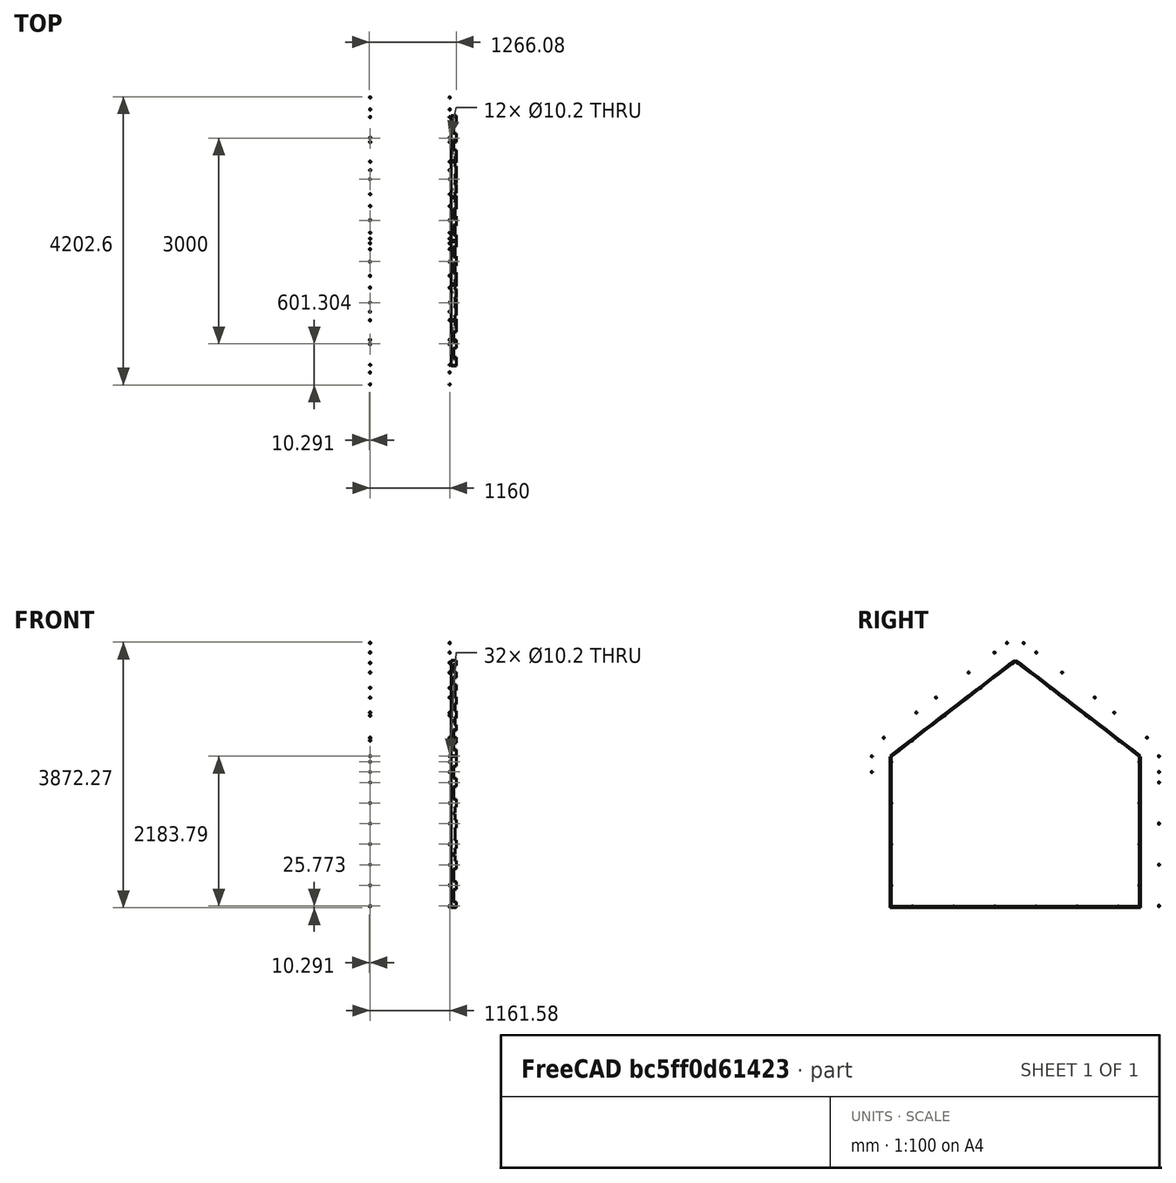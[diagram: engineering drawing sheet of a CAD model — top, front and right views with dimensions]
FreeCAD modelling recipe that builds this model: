
FCSTD DOCUMENT  (FreeCAD 0.17R11918 (Git))
Label: Unnamed1
License: CreativeCommons Attribution
LicenseURL: http://creativecommons.org/licenses/by/4.0/
objects: Part::FeaturePython×501, Part::Feature×150, Part::Part2DObjectPython×43, Part::Compound×19, Part::Cut×14, App::DocumentObjectGroupPython×13, App::DocumentObjectGroup×9, App::FeaturePython×1
note: 728 computed .brp shape members not serialized (recipe doc carries the construction recipe); baked Part::Feature solids carry a one-line shape summary decoded from their .brp

FEATURE [Part::Feature] Shape028  label="Bottom panel profile S"
  shape: bbox 1050 x 250 x 2e-07 mm, 0 faces, 0 solids (baked)
FEATURE [Part::Feature] Shape029  label="Bottom panel profile M"
  shape: bbox 1050 x 582 x 2e-07 mm, 0 faces, 0 solids (baked)
FEATURE [Part::Feature] Shape030  label="Bottom panel profile L"
  shape: bbox 1050 x 882 x 2e-07 mm, 0 faces, 0 solids (baked)
FEATURE [Part::Feature] Wire
  shape: bbox 250 x 1909 x 2e-07 mm, 0 faces, 0 solids (baked)
FEATURE [Part::Feature] Wire001
  shape: bbox 46 x 180 x 2e-07 mm, 0 faces, 0 solids (baked)
FEATURE [Part::Feature] Wire002
  shape: bbox 46 x 180 x 2e-07 mm, 0 faces, 0 solids (baked)
FEATURE [Part::Feature] Wire005
  shape: bbox 28 x 180 x 2e-07 mm, 0 faces, 0 solids (baked)
FEATURE [Part::Feature] Wire006
  shape: bbox 28 x 180 x 2e-07 mm, 0 faces, 0 solids (baked)
FEATURE [Part::Feature] Wire007
  shape: bbox 54 x 180 x 2e-07 mm, 0 faces, 0 solids (baked)
FEATURE [Part::Feature] Wire008
  shape: bbox 54 x 180 x 2e-07 mm, 0 faces, 0 solids (baked)
FEATURE [Part::Feature] Wire009 .. Wire012  x4 (patterned run collapsed; names and placements below)
  shape: bbox 28 x 180 x 2e-07 mm, 0 faces, 0 solids (baked)
FEATURE [Part::Feature] Wire021
  shape: bbox 2e-07 x 1341 x 707.1 mm, 0 faces, 0 solids (baked)
FEATURE [Part::Feature] Wire025
  shape: bbox 2e-07 x 28 x 72 mm, 0 faces, 0 solids (baked)
FEATURE [Part::Feature] Wire042
  shape: bbox 2e-07 x 813.7 x 1306 mm, 0 faces, 0 solids (baked)
FEATURE [Part::Feature] Wire043 .. Wire046  x4 (patterned run collapsed; names and placements below)
  shape: bbox 46 x 2e-07 x 180 mm, 0 faces, 0 solids (baked)
FEATURE [Part::Feature] Wire047
  shape: bbox 44 x 2e-07 x 180 mm, 0 faces, 0 solids (baked)
FEATURE [Part::Feature] Wire049
  shape: bbox 28 x 2e-07 x 180 mm, 0 faces, 0 solids (baked)
FEATURE [Part::Feature] Wire050
  shape: bbox 28 x 2e-07 x 180 mm, 0 faces, 0 solids (baked)
FEATURE [Part::Feature] Wire051
  shape: bbox 54 x 2e-07 x 180 mm, 0 faces, 0 solids (baked)
FEATURE [Part::Feature] Wire052
  shape: bbox 54 x 2e-07 x 180 mm, 0 faces, 0 solids (baked)
FEATURE [Part::Feature] Wire053 .. Wire056  x4 (patterned run collapsed; names and placements below)
  shape: bbox 46 x 2e-07 x 180 mm, 0 faces, 0 solids (baked)
FEATURE [Part::Feature] Wire057
  shape: bbox 1200 x 2e-07 x 2187 mm, 0 faces, 0 solids (baked)
FEATURE [Part::Feature] Wire058
  shape: bbox 54 x 180 x 2e-07 mm, 0 faces, 0 solids (baked)
FEATURE [Part::Feature] Wire059
  shape: bbox 54 x 180 x 2e-07 mm, 0 faces, 0 solids (baked)
FEATURE [Part::Feature] Wire060
  shape: bbox 54 x 180 x 2e-07 mm, 0 faces, 0 solids (baked)
FEATURE [Part::Feature] Wire061
  shape: bbox 90 x 23 x 2e-07 mm, 0 faces, 0 solids (baked)
FEATURE [Part::Feature] Wire062
  shape: bbox 54 x 180 x 2e-07 mm, 0 faces, 0 solids (baked)
FEATURE [Part::Feature] Wire063
  shape: bbox 46 x 180 x 2e-07 mm, 0 faces, 0 solids (baked)
FEATURE [Part::Feature] Wire064
  shape: bbox 46 x 180 x 2e-07 mm, 0 faces, 0 solids (baked)
FEATURE [Part::Feature] Wire065
  shape: bbox 71 x 180 x 2e-07 mm, 0 faces, 0 solids (baked)
FEATURE [Part::Feature] Wire066
  shape: bbox 90 x 23 x 2e-07 mm, 0 faces, 0 solids (baked)
FEATURE [Part::Feature] Wire067
  shape: bbox 71 x 180 x 2e-07 mm, 0 faces, 0 solids (baked)
FEATURE [Part::Feature] Wire068
  shape: bbox 1200 x 1384 x 2e-07 mm, 0 faces, 0 solids (baked)
FEATURE [Part::Compound] Compound005  label="floor panel profile small"
  Links = -> [Wire058,Wire059,Wire060,Wire068,Wire062,Wire061,Wire063,Wire064,Wire065,Wire066,Wire067]
FEATURE [Part::Feature] Wire069
  shape: bbox 71 x 180 x 2e-07 mm, 0 faces, 0 solids (baked)
FEATURE [Part::Feature] Wire070
  shape: bbox 90 x 23 x 2e-07 mm, 0 faces, 0 solids (baked)
FEATURE [Part::Feature] Wire071
  shape: bbox 71 x 180 x 2e-07 mm, 0 faces, 0 solids (baked)
FEATURE [Part::Feature] Wire072
  shape: bbox 46 x 180 x 2e-07 mm, 0 faces, 0 solids (baked)
FEATURE [Part::Feature] Wire073
  shape: bbox 46 x 180 x 2e-07 mm, 0 faces, 0 solids (baked)
FEATURE [Part::Feature] Wire074
  shape: bbox 54 x 180 x 2e-07 mm, 0 faces, 0 solids (baked)
FEATURE [Part::Feature] Wire075
  shape: bbox 90 x 23 x 2e-07 mm, 0 faces, 0 solids (baked)
FEATURE [Part::Feature] Wire076 .. Wire079  x4 (patterned run collapsed; names and placements below)
  shape: bbox 54 x 180 x 2e-07 mm, 0 faces, 0 solids (baked)
FEATURE [Part::Feature] Wire080
  shape: bbox 90 x 23 x 2e-07 mm, 0 faces, 0 solids (baked)
FEATURE [Part::Feature] Wire081
  shape: bbox 54 x 180 x 2e-07 mm, 0 faces, 0 solids (baked)
FEATURE [Part::Feature] Wire082 .. Wire085  x4 (patterned run collapsed; names and placements below)
  shape: bbox 28 x 180 x 2e-07 mm, 0 faces, 0 solids (baked)
FEATURE [Part::Feature] Wire086
  shape: bbox 1200 x 2284 x 2e-07 mm, 0 faces, 0 solids (baked)
FEATURE [Part::Compound] Compound006  label="floor panel profile large"
  Links = -> [Wire069,Wire084,Wire076,Wire077,Wire071,Wire080,Wire078,Wire075,Wire079,Wire081,Wire082,Wire083,Wire073,Wire072,Wire086,Wire074,Wire085,Wire070]
FEATURE [Part::FeaturePython] Panel028  label="Floor panel small 001"  # WARN: FeaturePython — macro-defined, semantics opaque (R4)
  Area = 1.59758e+06
  Base = -> Compound005
  Description = Floor panel
  FaceMaker = 0
  HorizontalArea = 0
  Length = 0
  MoveWithHost = false
  Normal = (0,0,-1)
  PerimeterLength = 0
  Role = 0
  Sheets = 1
  Tag = L61
  Thickness = 18
  VerticalArea = 0
  WaveDirection = 0
  WaveHeight = 0
  WaveLength = 0
  WaveType = 0
  Width = 0
FEATURE [Part::FeaturePython] Panel029  label="Floor panel large 001"  # WARN: FeaturePython — macro-defined, semantics opaque (R4)
  Area = 2.65298e+06
  Base = -> Compound006
  Description = Floor panel
  FaceMaker = 0
  HorizontalArea = 0
  Length = 0
  MoveWithHost = false
  Normal = (0,0,-1)
  PerimeterLength = 0
  Role = 0
  Sheets = 1
  Tag = L62
  Thickness = 18
  VerticalArea = 0
  WaveDirection = 0
  WaveHeight = 0
  WaveLength = 0
  WaveType = 0
  Width = 0
FEATURE [Part::Feature] Shape035
  shape: bbox 54 x 2e-07 x 180 mm, 0 faces, 0 solids (baked)
FEATURE [Part::Feature] Shape034017
  shape: bbox 28 x 180 x 2e-07 mm, 0 faces, 0 solids (baked)
FEATURE [Part::Feature] Shape034018
  shape: bbox 54 x 180 x 2e-07 mm, 0 faces, 0 solids (baked)
FEATURE [Part::Feature] Shape034019
  shape: bbox 46 x 180 x 2e-07 mm, 0 faces, 0 solids (baked)
FEATURE [Part::Feature] Shape034020
  shape: bbox 46 x 180 x 2e-07 mm, 0 faces, 0 solids (baked)
FEATURE [Part::Feature] Shape034021
  shape: bbox 54 x 180 x 2e-07 mm, 0 faces, 0 solids (baked)
FEATURE [Part::Feature] Shape034022
  shape: bbox 54 x 180 x 2e-07 mm, 0 faces, 0 solids (baked)
FEATURE [Part::Feature] Shape034023
  shape: bbox 54 x 180 x 2e-07 mm, 0 faces, 0 solids (baked)
FEATURE [Part::Feature] Shape034024 .. Shape034027  x4 (patterned run collapsed; names and placements below)
  shape: bbox 46 x 180 x 2e-07 mm, 0 faces, 0 solids (baked)
FEATURE [Part::Feature] Shape034028
  shape: bbox 28 x 180 x 2e-07 mm, 0 faces, 0 solids (baked)
FEATURE [Part::Feature] Shape034029
  shape: bbox 46 x 180 x 2e-07 mm, 0 faces, 0 solids (baked)
FEATURE [Part::Feature] Shape034030
  shape: bbox 46 x 180 x 2e-07 mm, 0 faces, 0 solids (baked)
FEATURE [Part::Feature] Shape034031
  shape: bbox 1200 x 2280 x 2e-07 mm, 0 faces, 0 solids (baked)
FEATURE [Part::Feature] Shape034032
  shape: bbox 39 x 28 x 2e-07 mm, 0 faces, 0 solids (baked)
FEATURE [Part::Feature] Shape034033
  shape: bbox 1200 x 268 x 2e-07 mm, 0 faces, 0 solids (baked)
FEATURE [Part::Feature] Shape034034
  shape: bbox 39 x 28 x 2e-07 mm, 0 faces, 0 solids (baked)
FEATURE [Part::Compound] Compound011  label="Spacer profile large"
  Links = -> [Shape034032,Shape034033,Shape034034]
FEATURE [Part::FeaturePython] Panel034  label="Spacer 001"  # WARN: FeaturePython — macro-defined, semantics opaque (R4)
  Area = 273615
  Base = -> Compound011
  Description = Spacer
  FaceMaker = 0
  HorizontalArea = 0
  Length = 0
  MoveWithHost = false
  Normal = (0,0,1)
  PerimeterLength = 0
  Placement = pos=(0,0,134) rot=(0,0,1;0rad)
  Role = 0
  Sheets = 1
  Tag = SPACER/F
  Thickness = 18
  VerticalArea = 0
  WaveDirection = 0
  WaveHeight = 0
  WaveLength = 0
  WaveType = 0
  Width = 0
FEATURE [Part::FeaturePython] Panel035  label="Spacer 002"  # WARN: FeaturePython — macro-defined, semantics opaque (R4)
  Area = 273615
  CloneOf = -> Panel034
  Description = Spacer
  FaceMaker = 0
  HorizontalArea = 0
  Length = 0
  MoveWithHost = false
  Normal = (0,0,0)
  PerimeterLength = 0
  Placement = pos=(0,-1659,-1807) rot=(-1,0,0;1.5708rad)
  Role = 0
  Sheets = 1
  Tag = SPACER/F
  Thickness = 18
  VerticalArea = 0
  WaveDirection = 0
  WaveHeight = 0
  WaveLength = 0
  WaveType = 0
  Width = 0
FEATURE [Part::FeaturePython] Panel036  label="Spacer 003"  # WARN: FeaturePython — macro-defined, semantics opaque (R4)
  Area = 273615
  CloneOf = -> Panel034
  Description = Spacer
  FaceMaker = 0
  HorizontalArea = 0
  Length = 0
  MoveWithHost = false
  Normal = (0,0,0)
  PerimeterLength = 0
  Placement = pos=(0,-1059,-1807) rot=(-1,0,0;1.5708rad)
  Role = 0
  Sheets = 1
  Tag = SPACER/F
  Thickness = 18
  VerticalArea = 0
  WaveDirection = 0
  WaveHeight = 0
  WaveLength = 0
  WaveType = 0
  Width = 0
FEATURE [Part::FeaturePython] Panel037  label="Spacer 004"  # WARN: FeaturePython — macro-defined, semantics opaque (R4)
  Area = 273615
  CloneOf = -> Panel034
  Description = Spacer
  FaceMaker = 0
  HorizontalArea = 0
  Length = 0
  MoveWithHost = false
  Normal = (0,0,0)
  PerimeterLength = 0
  Placement = pos=(0,-458.997,-1807) rot=(-1,0,0;1.5708rad)
  Role = 0
  Sheets = 1
  Tag = SPACER/F
  Thickness = 18
  VerticalArea = 0
  WaveDirection = 0
  WaveHeight = 0
  WaveLength = 0
  WaveType = 0
  Width = 0
FEATURE [Part::FeaturePython] Panel038  label="Spacer 005"  # WARN: FeaturePython — macro-defined, semantics opaque (R4)
  Area = 273615
  CloneOf = -> Panel034
  Description = Spacer
  FaceMaker = 0
  HorizontalArea = 0
  Length = 0
  MoveWithHost = false
  Normal = (0,0,0)
  PerimeterLength = 0
  Placement = pos=(0,440.996,-1807) rot=(-1,0,0;1.5708rad)
  Role = 0
  Sheets = 1
  Tag = SPACER/F
  Thickness = 18
  VerticalArea = 0
  WaveDirection = 0
  WaveHeight = 0
  WaveLength = 0
  WaveType = 0
  Width = 0
FEATURE [Part::FeaturePython] Panel039  label="Spacer 006"  # WARN: FeaturePython — macro-defined, semantics opaque (R4)
  Area = 273615
  CloneOf = -> Panel034
  Description = Spacer
  FaceMaker = 0
  HorizontalArea = 0
  Length = 0
  MoveWithHost = false
  Normal = (0,0,0)
  PerimeterLength = 0
  Placement = pos=(0,1041,-1807) rot=(-1,0,0;1.5708rad)
  Role = 0
  Sheets = 1
  Tag = SPACER/F
  Thickness = 18
  VerticalArea = 0
  WaveDirection = 0
  WaveHeight = 0
  WaveLength = 0
  WaveType = 0
  Width = 0
FEATURE [Part::FeaturePython] Panel040  label="Spacer 007"  # WARN: FeaturePython — macro-defined, semantics opaque (R4)
  Area = 273615
  CloneOf = -> Panel034
  Description = Spacer
  FaceMaker = 0
  HorizontalArea = 0
  Length = 0
  MoveWithHost = false
  Normal = (0,0,0)
  PerimeterLength = 0
  Placement = pos=(0,1641,-1807) rot=(-1,0,0;1.5708rad)
  Role = 0
  Sheets = 1
  Tag = SPACER/F
  Thickness = 18
  VerticalArea = 0
  WaveDirection = 0
  WaveHeight = 0
  WaveLength = 0
  WaveType = 0
  Width = 0
FEATURE [Part::FeaturePython] Panel041  label="Spacer 008"  # WARN: FeaturePython — macro-defined, semantics opaque (R4)
  Area = 273615
  CloneOf = -> Panel034
  Description = Spacer
  FaceMaker = 0
  HorizontalArea = 0
  Length = 0
  MoveWithHost = false
  Normal = (0,0,0)
  PerimeterLength = 0
  Placement = pos=(0,-2.785e-09,152) rot=(1,0,0;3.14159rad)
  Role = 0
  Sheets = 1
  Tag = SPACER/F
  Thickness = 18
  VerticalArea = 0
  WaveDirection = 0
  WaveHeight = 0
  WaveLength = 0
  WaveType = 0
  Width = 0
FEATURE [Part::Feature] Shape034035  label="Spacer profile small"
  shape: bbox 1200 x 268 x 2e-07 mm, 0 faces, 0 solids (baked)
FEATURE [Part::FeaturePython] Panel042  label="Spacer 009"  # WARN: FeaturePython — macro-defined, semantics opaque (R4)
  Area = 275459
  Base = -> Shape034035
  Description = Spacer
  FaceMaker = 0
  HorizontalArea = 0
  Length = 0
  MoveWithHost = false
  Normal = (0,0,1)
  PerimeterLength = 0
  Placement = pos=(0,0,2463.44) rot=(0,0,1;0rad)
  Role = 0
  Sheets = 1
  Tag = SPACER/R
  Thickness = 18
  VerticalArea = 0
  WaveDirection = 0
  WaveHeight = 0
  WaveLength = 0
  WaveType = 0
  Width = 0
FEATURE [Part::FeaturePython] Panel043  label="Spacer 010"  # WARN: FeaturePython — macro-defined, semantics opaque (R4)
  Area = 275459
  CloneOf = -> Panel042
  Description = Spacer
  FaceMaker = 0
  HorizontalArea = 0
  Length = 0
  MoveWithHost = false
  Normal = (0,0,0)
  PerimeterLength = 0
  Placement = pos=(-0.000976562,9.00024,6018.77) rot=(1,0,0;1.5708rad)
  Role = 0
  Sheets = 1
  Tag = SPACER/R
  Thickness = 18
  VerticalArea = 0
  WaveDirection = 0
  WaveHeight = 0
  WaveLength = 0
  WaveType = 0
  Width = 0
FEATURE [Part::FeaturePython] Panel044  label="Spacer 011"  # WARN: FeaturePython — macro-defined, semantics opaque (R4)
  Area = 275459
  CloneOf = -> Panel042
  Description = Spacer
  FaceMaker = 0
  HorizontalArea = 0
  Length = 0
  MoveWithHost = false
  Normal = (0,0,0)
  PerimeterLength = 0
  Placement = pos=(0,0,2481.44) rot=(1,0,0;3.14159rad)
  Role = 0
  Sheets = 1
  Tag = SPACER/R
  Thickness = 18
  VerticalArea = 0
  WaveDirection = 0
  WaveHeight = 0
  WaveLength = 0
  WaveType = 0
  Width = 0
FEATURE [Part::Feature] Wire091  label="Lock"
  shape: bbox 230 x 2e-07 x 120.4 mm, 0 faces, 0 solids (baked)
FEATURE [Part::FeaturePython] Panel045  label="Lock 001"  # WARN: FeaturePython — macro-defined, semantics opaque (R4)
  Area = 14950.6
  Base = -> Wire091
  Description = Lock
  FaceMaker = 0
  HorizontalArea = 0
  Length = 0
  MoveWithHost = false
  Normal = (0,-1,0)
  PerimeterLength = 0
  Role = 0
  Sheets = 1
  Tag = L43
  Thickness = 18
  VerticalArea = 0
  WaveDirection = 0
  WaveHeight = 0
  WaveLength = 0
  WaveType = 0
  Width = 0
FEATURE [Part::FeaturePython] Panel046  label="Lock 002"  # WARN: FeaturePython — macro-defined, semantics opaque (R4)
  Area = 14950.6
  CloneOf = -> Panel045
  Description = Lock
  FaceMaker = 0
  HorizontalArea = 0
  Length = 0
  MoveWithHost = false
  Normal = (0,0,0)
  PerimeterLength = 0
  Placement = pos=(1198.67,0,0) rot=(0,0,1;0rad)
  Role = 0
  Sheets = 1
  Tag = L43
  Thickness = 18
  VerticalArea = 0
  WaveDirection = 0
  WaveHeight = 0
  WaveLength = 0
  WaveType = 0
  Width = 0
FEATURE [Part::FeaturePython] Panel047  label="Lock 003"  # WARN: FeaturePython — macro-defined, semantics opaque (R4)
  Area = 14950.6
  CloneOf = -> Panel045
  Description = Lock
  FaceMaker = 0
  HorizontalArea = 0
  Length = 0
  MoveWithHost = false
  Normal = (0,0,0)
  PerimeterLength = 0
  Placement = pos=(1198.67,3899.99,0) rot=(0,0,1;0rad)
  Role = 0
  Sheets = 1
  Tag = L43
  Thickness = 18
  VerticalArea = 0
  WaveDirection = 0
  WaveHeight = 0
  WaveLength = 0
  WaveType = 0
  Width = 0
FEATURE [Part::FeaturePython] Panel048  label="Lock 004"  # WARN: FeaturePython — macro-defined, semantics opaque (R4)
  Area = 14950.6
  CloneOf = -> Panel045
  Description = Lock
  FaceMaker = 0
  HorizontalArea = 0
  Length = 0
  MoveWithHost = false
  Normal = (0,0,0)
  PerimeterLength = 0
  Placement = pos=(0,3899.99,0) rot=(0,0,1;0rad)
  Role = 0
  Sheets = 1
  Tag = L43
  Thickness = 18
  VerticalArea = 0
  WaveDirection = 0
  WaveHeight = 0
  WaveLength = 0
  WaveType = 0
  Width = 0
FEATURE [App::DocumentObjectGroupPython] VisGroup003  label="level4 spacers (3 originals)"  # scripted group (container) (typed FeaturePython)
  Group = -> [Panel034,Panel035,Panel036,Panel037,Panel038,Panel039,Panel040,Panel041,Panel042,Panel043,Panel044,Panel045,Panel046,Panel047,Panel048]
FEATURE [Part::Feature] Shape034040
  shape: bbox 2e-07 x 1409 x 733.2 mm, 0 faces, 0 solids (baked)
FEATURE [Part::Feature] Shape034046
  shape: bbox 2e-07 x 28 x 72 mm, 0 faces, 0 solids (baked)
FEATURE [Part::Feature] Shape034064
  shape: bbox 2e-07 x 72 x 28 mm, 0 faces, 0 solids (baked)
FEATURE [Part::Feature] Shape034067
  shape: bbox 2e-07 x 1573 x 1916 mm, 0 faces, 0 solids (baked)
FEATURE [Part::Feature] Shape034087
  shape: bbox 2e-07 x 28 x 72 mm, 0 faces, 0 solids (baked)
FEATURE [Part::Feature] Shape034095
  shape: bbox 2e-07 x 2415 x 286 mm, 0 faces, 0 solids (baked)
FEATURE [Part::Feature] Shape034102
  shape: bbox 2e-07 x 28 x 72 mm, 0 faces, 0 solids (baked)
FEATURE [Part::Feature] Shape034103
  shape: bbox 2e-07 x 28 x 72 mm, 0 faces, 0 solids (baked)
FEATURE [Part::Feature] Shape034104
  shape: bbox 2e-07 x 28 x 72 mm, 0 faces, 0 solids (baked)
FEATURE [Part::Feature] Shape034107
  shape: bbox 2e-07 x 28 x 72 mm, 0 faces, 0 solids (baked)
FEATURE [Part::Feature] Shape034120
  shape: bbox 2e-07 x 72 x 28 mm, 0 faces, 0 solids (baked)
FEATURE [Part::FeaturePython] Panel073  label="Bottom panel small 001"  # WARN: FeaturePython — macro-defined, semantics opaque (R4)
  Area = 262499
  Base = -> Shape028
  Description = Bottom panel
  FaceMaker = 0
  HorizontalArea = 0
  Length = 0
  MoveWithHost = false
  Normal = (0,0,1)
  PerimeterLength = 0
  Role = 0
  Sheets = 1
  Tag = L43
  Thickness = 18
  VerticalArea = 0
  WaveDirection = 0
  WaveHeight = 0
  WaveLength = 0
  WaveType = 0
  Width = 0
FEATURE [Part::FeaturePython] Panel074  label="Bottom panel medium 001"  # WARN: FeaturePython — macro-defined, semantics opaque (R4)
  Area = 611099
  Base = -> Shape029
  Description = Bottom panel
  FaceMaker = 0
  HorizontalArea = 0
  Length = 0
  MoveWithHost = false
  Normal = (0,0,1)
  PerimeterLength = 0
  Role = 0
  Sheets = 1
  Tag = FLOOR/M
  Thickness = 18
  VerticalArea = 0
  WaveDirection = 0
  WaveHeight = 0
  WaveLength = 0
  WaveType = 0
  Width = 0
FEATURE [Part::FeaturePython] Panel075  label="Bottom panel large 001"  # WARN: FeaturePython — macro-defined, semantics opaque (R4)
  Area = 926091
  Base = -> Shape030
  Description = Bottom panel
  FaceMaker = 0
  HorizontalArea = 0
  Length = 0
  MoveWithHost = false
  Normal = (0,0,1)
  PerimeterLength = 0
  Role = 0
  Sheets = 1
  Tag = L41
  Thickness = 18
  VerticalArea = 0
  WaveDirection = 0
  WaveHeight = 0
  WaveLength = 0
  WaveType = 0
  Width = 0
FEATURE [Part::Feature] Shape034126  label="Bottom lock profile"
  shape: bbox 1200 x 101 x 2e-07 mm, 0 faces, 0 solids (baked)
FEATURE [Part::FeaturePython] Panel076  label="Bottom lock 001"  # WARN: FeaturePython — macro-defined, semantics opaque (R4)
  Area = 118903
  Base = -> Shape034126
  Description = Bottom panel
  FaceMaker = 0
  HorizontalArea = 0
  Length = 0
  MoveWithHost = false
  Normal = (0,0,1)
  PerimeterLength = 0
  Role = 0
  Sheets = 1
  Tag = SKI/C
  Thickness = 18
  VerticalArea = 0
  WaveDirection = 0
  WaveHeight = 0
  WaveLength = 0
  WaveType = 0
  Width = 0
FEATURE [Part::Feature] Shape034127
  shape: bbox 46 x 2e-07 x 180 mm, 0 faces, 0 solids (baked)
FEATURE [Part::Feature] Shape034128
  shape: bbox 46 x 2e-07 x 180 mm, 0 faces, 0 solids (baked)
FEATURE [Part::Feature] Shape034129
  shape: bbox 54 x 2e-07 x 180 mm, 0 faces, 0 solids (baked)
FEATURE [Part::Feature] Shape034130
  shape: bbox 1200 x 2e-07 x 2107 mm, 0 faces, 0 solids (baked)
FEATURE [Part::Feature] Shape034131
  shape: bbox 54 x 2e-07 x 180 mm, 0 faces, 0 solids (baked)
FEATURE [Part::Feature] Shape034132
  shape: bbox 54 x 2e-07 x 180 mm, 0 faces, 0 solids (baked)
FEATURE [Part::Feature] Shape034133
  shape: bbox 46 x 2e-07 x 180 mm, 0 faces, 0 solids (baked)
FEATURE [Part::Feature] Shape034134
  shape: bbox 46 x 2e-07 x 180 mm, 0 faces, 0 solids (baked)
FEATURE [Part::Feature] Shape034135
  shape: bbox 71 x 2e-07 x 180 mm, 0 faces, 0 solids (baked)
FEATURE [Part::Feature] Shape034136
  shape: bbox 46 x 2e-07 x 180 mm, 0 faces, 0 solids (baked)
FEATURE [Part::Feature] Shape034137
  shape: bbox 28 x 2e-07 x 180 mm, 0 faces, 0 solids (baked)
FEATURE [Part::Feature] Shape034138
  shape: bbox 46 x 2e-07 x 180 mm, 0 faces, 0 solids (baked)
FEATURE [Part::Feature] Shape034139
  shape: bbox 54 x 2e-07 x 180 mm, 0 faces, 0 solids (baked)
FEATURE [Part::Feature] Shape034140
  shape: bbox 28 x 2e-07 x 180 mm, 0 faces, 0 solids (baked)
FEATURE [Part::Feature] Shape034141
  shape: bbox 71 x 2e-07 x 180 mm, 0 faces, 0 solids (baked)
FEATURE [Part::Feature] Shape034142
  shape: bbox 90 x 2e-07 x 23 mm, 0 faces, 0 solids (baked)
FEATURE [Part::Compound] Compound023  label="Outer side panel profile L"
  Links = -> [Shape034127,Shape034134,Shape034133,Shape034130,Shape034139,Shape034129,Shape034131,Shape034137,Shape034136,Shape034141,Shape034132,Shape034140,Shape034135,Shape034128,Shape034142,Shape034138]
FEATURE [Part::FeaturePython] Panel077  label="Outer side panel large 001"  # WARN: FeaturePython — macro-defined, semantics opaque (R4)
  Area = 2.40982e+06
  Base = -> Compound023
  Description = Outer side panel
  FaceMaker = 0
  HorizontalArea = 0
  Length = 0
  MoveWithHost = false
  Normal = (0,1,0)
  PerimeterLength = 0
  Placement = pos=(0,-2093,0) rot=(0,0,1;0rad)
  Role = 0
  Sheets = 1
  Tag = L45
  Thickness = 18
  VerticalArea = 0
  WaveDirection = 0
  WaveHeight = 0
  WaveLength = 0
  WaveType = 0
  Width = 0
FEATURE [Part::Feature] Shape034143
  shape: bbox 46 x 2e-07 x 180 mm, 0 faces, 0 solids (baked)
FEATURE [Part::Feature] Shape034144
  shape: bbox 90 x 2e-07 x 23 mm, 0 faces, 0 solids (baked)
FEATURE [Part::Feature] Shape034145
  shape: bbox 1200 x 2e-07 x 543.8 mm, 0 faces, 0 solids (baked)
FEATURE [Part::Feature] Shape034146
  shape: bbox 46 x 2e-07 x 180 mm, 0 faces, 0 solids (baked)
FEATURE [Part::Compound] Compound025  label="Outer side panel profile S"
  Links = -> [Shape034143,Shape034144,Shape034145,Shape034146]
FEATURE [Part::FeaturePython] Panel078  label="Outer side panel small 001"  # WARN: FeaturePython — macro-defined, semantics opaque (R4)
  Area = 598321
  Base = -> Compound025
  Description = Outer side panel
  FaceMaker = 0
  HorizontalArea = 0
  Length = 0
  MoveWithHost = false
  Normal = (0,1,0)
  PerimeterLength = 0
  Placement = pos=(0,-2093,0) rot=(0,0,1;0rad)
  Role = 0
  Sheets = 1
  Tag = L46
  Thickness = 18
  VerticalArea = 0
  WaveDirection = 0
  WaveHeight = 0
  WaveLength = 0
  WaveType = 0
  Width = 0
FEATURE [Part::Feature] Wire112
  shape: bbox 46 x 180 x 2e-07 mm, 0 faces, 0 solids (baked)
FEATURE [Part::Feature] Wire113
  shape: bbox 46 x 180 x 2e-07 mm, 0 faces, 0 solids (baked)
FEATURE [Part::Feature] Wire114
  shape: bbox 54 x 180 x 2e-07 mm, 0 faces, 0 solids (baked)
FEATURE [Part::Feature] Wire115
  shape: bbox 54 x 180 x 2e-07 mm, 0 faces, 0 solids (baked)
FEATURE [Part::Feature] Wire116
  shape: bbox 28 x 180 x 2e-07 mm, 0 faces, 0 solids (baked)
FEATURE [Part::Feature] Wire117
  shape: bbox 28 x 180 x 2e-07 mm, 0 faces, 0 solids (baked)
FEATURE [Part::Feature] Wire118
  shape: bbox 54 x 180 x 2e-07 mm, 0 faces, 0 solids (baked)
FEATURE [Part::Feature] Wire119
  shape: bbox 54 x 180 x 2e-07 mm, 0 faces, 0 solids (baked)
FEATURE [Part::Feature] Wire120 .. Wire123  x4 (patterned run collapsed; names and placements below)
  shape: bbox 46 x 180 x 2e-07 mm, 0 faces, 0 solids (baked)
FEATURE [Part::Feature] Wire124
  shape: bbox 1200 x 2104 x 2e-07 mm, 0 faces, 0 solids (baked)
FEATURE [Part::Compound] Compound026  label="Outer roof profile L"
  Links = -> [Wire112,Wire124,Wire119,Wire117,Wire113,Wire116,Wire118,Wire114,Wire121,Wire115,Wire120,Wire122,Wire123]
FEATURE [Part::FeaturePython] Panel079  label="Outer roof panel large 001"  # WARN: FeaturePython — macro-defined, semantics opaque (R4)
  Area = 2.42218e+06
  Base = -> Compound026
  Description = Roof panel
  FaceMaker = 0
  HorizontalArea = 0
  Length = 0
  MoveWithHost = false
  Normal = (0,0,1)
  PerimeterLength = 0
  Placement = pos=(1486.92,-421.605,3876.38) rot=(1,0,0;0.655696rad)
  Role = 0
  Sheets = 1
  Tag = L47
  Thickness = 18
  VerticalArea = 0
  WaveDirection = 0
  WaveHeight = 0
  WaveLength = 0
  WaveType = 0
  Width = 0
FEATURE [Part::Feature] Wire125
  shape: bbox 46 x 180 x 2e-07 mm, 0 faces, 0 solids (baked)
FEATURE [Part::Feature] Wire126
  shape: bbox 46 x 180 x 2e-07 mm, 0 faces, 0 solids (baked)
FEATURE [Part::Feature] Wire127
  shape: bbox 1200 x 578.4 x 2e-07 mm, 0 faces, 0 solids (baked)
FEATURE [Part::FeaturePython] Panel081  label="Bottom panel medium 002"  # WARN: FeaturePython — macro-defined, semantics opaque (R4)
  Area = 611099
  CloneOf = -> Panel074
  Description = Bottom panel
  FaceMaker = 0
  HorizontalArea = 0
  Length = 0
  MoveWithHost = false
  Normal = (0,0,0)
  PerimeterLength = 0
  Placement = pos=(0,600.001,0) rot=(0,0,1;0rad)
  Role = 0
  Sheets = 1
  Tag = FLOOR/M
  Thickness = 18
  VerticalArea = 0
  WaveDirection = 0
  WaveHeight = 0
  WaveLength = 0
  WaveType = 0
  Width = 0
FEATURE [Part::FeaturePython] Panel082  label="Bottom panel medium 003"  # WARN: FeaturePython — macro-defined, semantics opaque (R4)
  Area = 611099
  CloneOf = -> Panel074
  Description = Bottom panel
  FaceMaker = 0
  HorizontalArea = 0
  Length = 0
  MoveWithHost = false
  Normal = (0,0,0)
  PerimeterLength = 0
  Placement = pos=(0.00012207,2700,0) rot=(0,0,1;0rad)
  Role = 0
  Sheets = 1
  Tag = FLOOR/M
  Thickness = 18
  VerticalArea = 0
  WaveDirection = 0
  WaveHeight = 0
  WaveLength = 0
  WaveType = 0
  Width = 0
FEATURE [Part::FeaturePython] Panel083  label="Bottom panel medium 004"  # WARN: FeaturePython — macro-defined, semantics opaque (R4)
  Area = 611099
  CloneOf = -> Panel074
  Description = Bottom panel
  FaceMaker = 0
  HorizontalArea = 0
  Length = 0
  MoveWithHost = false
  Normal = (0,0,0)
  PerimeterLength = 0
  Placement = pos=(0.00012207,2100,0) rot=(0,0,1;0rad)
  Role = 0
  Sheets = 1
  Tag = FLOOR/M
  Thickness = 18
  VerticalArea = 0
  WaveDirection = 0
  WaveHeight = 0
  WaveLength = 0
  WaveType = 0
  Width = 0
FEATURE [Part::FeaturePython] Panel084  label="Bottom panel small 002"  # WARN: FeaturePython — macro-defined, semantics opaque (R4)
  Area = 262499
  CloneOf = -> Panel073
  Description = Bottom panel
  FaceMaker = 0
  HorizontalArea = 0
  Length = 0
  MoveWithHost = false
  Normal = (0,0,0)
  PerimeterLength = 0
  Placement = pos=(0,3567.99,0) rot=(0,0,1;0rad)
  Role = 0
  Sheets = 1
  Tag = L43
  Thickness = 18
  VerticalArea = 0
  WaveDirection = 0
  WaveHeight = 0
  WaveLength = 0
  WaveType = 0
  Width = 0
FEATURE [Part::FeaturePython] Panel085  label="Bottom lock 002"  # WARN: FeaturePython — macro-defined, semantics opaque (R4)
  Area = 118903
  CloneOf = -> Panel076
  Description = Bottom panel
  FaceMaker = 0
  HorizontalArea = 0
  Length = 0
  MoveWithHost = false
  Normal = (0,0,0)
  PerimeterLength = 0
  Placement = pos=(0,2.14578e-06,18.0002) rot=(1,0,0;3.14159rad)
  Role = 0
  Sheets = 1
  Tag = SKI/C
  Thickness = 18
  VerticalArea = 0
  WaveDirection = 0
  WaveHeight = 0
  WaveLength = 0
  WaveType = 0
  Width = 0
FEATURE [Part::FeaturePython] Panel086  label="Outer side panel small 002"  # WARN: FeaturePython — macro-defined, semantics opaque (R4)
  Area = 598321
  CloneOf = -> Panel078
  Description = Outer side panel
  FaceMaker = 0
  HorizontalArea = 0
  Length = 0
  MoveWithHost = false
  Normal = (0,0,0)
  PerimeterLength = 0
  Placement = pos=(0,2075,0) rot=(0,0,1;0rad)
  Role = 0
  Sheets = 1
  Tag = L46
  Thickness = 18
  VerticalArea = 0
  WaveDirection = 0
  WaveHeight = 0
  WaveLength = 0
  WaveType = 0
  Width = 0
FEATURE [Part::FeaturePython] Panel087  label="Outer side panel large 002"  # WARN: FeaturePython — macro-defined, semantics opaque (R4)
  Area = 2.40982e+06
  CloneOf = -> Panel077
  Description = Outer side panel
  FaceMaker = 0
  HorizontalArea = 0
  Length = 0
  MoveWithHost = false
  Normal = (0,0,0)
  PerimeterLength = 0
  Placement = pos=(0,2075,0) rot=(0,0,1;0rad)
  Role = 0
  Sheets = 1
  Tag = L45
  Thickness = 18
  VerticalArea = 0
  WaveDirection = 0
  WaveHeight = 0
  WaveLength = 0
  WaveType = 0
  Width = 0
FEATURE [Part::FeaturePython] Panel089  label="Outer roof panel large 002"  # WARN: FeaturePython — macro-defined, semantics opaque (R4)
  Area = 2.42218e+06
  CloneOf = -> Panel079
  Description = Roof panel
  FaceMaker = 0
  HorizontalArea = 0
  Length = 0
  MoveWithHost = false
  Normal = (0,0,0)
  PerimeterLength = 0
  Placement = pos=(1486.92,432.58,3890.65) rot=(1,0,0;2.4859rad)
  Role = 0
  Sheets = 1
  Tag = L47
  Thickness = 18
  VerticalArea = 0
  WaveDirection = 0
  WaveHeight = 0
  WaveLength = 0
  WaveType = 0
  Width = 0
FEATURE [Part::Feature] Shape034147
  shape: bbox 150 x 286 x 2e-07 mm, 0 faces, 0 solids (baked)
FEATURE [Part::FeaturePython] Panel090  label="Struct spacer 001"  # WARN: FeaturePython — macro-defined, semantics opaque (R4)
  Area = 30741.9
  Base = -> Shape034147
  FaceMaker = 0
  HorizontalArea = 0
  Length = 0
  MoveWithHost = false
  Normal = (0,0,1)
  PerimeterLength = 0
  Placement = pos=(0,0,1034) rot=(0,0,1;0rad)
  Role = 0
  Sheets = 1
  Tag = S/S
  Thickness = 18
  VerticalArea = 0
  WaveDirection = 0
  WaveHeight = 0
  WaveLength = 0
  WaveType = 0
  Width = 0
FEATURE [Part::FeaturePython] Panel091  label="Struct spacer 002"  # WARN: FeaturePython — macro-defined, semantics opaque (R4)
  Area = 30741.9
  CloneOf = -> Panel090
  Description = structure spacer
  FaceMaker = 0
  HorizontalArea = 0
  Length = 0
  MoveWithHost = false
  Normal = (0,0,0)
  PerimeterLength = 0
  Placement = pos=(0,-9.15552e-05,1634) rot=(0,0,1;0rad)
  Role = 0
  Sheets = 1
  Tag = S/S
  Thickness = 18
  VerticalArea = 0
  WaveDirection = 0
  WaveHeight = 0
  WaveLength = 0
  WaveType = 0
  Width = 0
FEATURE [Part::FeaturePython] Panel092  label="Struct spacer 003"  # WARN: FeaturePython — macro-defined, semantics opaque (R4)
  Area = 30741.9
  CloneOf = -> Panel090
  Description = structure spacer
  FaceMaker = 0
  HorizontalArea = 0
  Length = 0
  MoveWithHost = false
  Normal = (0,0,0)
  PerimeterLength = 0
  Placement = pos=(-2.969e-09,-3899.99,1634) rot=(0,0,1;0rad)
  Role = 0
  Sheets = 1
  Tag = S/S
  Thickness = 18
  VerticalArea = 0
  WaveDirection = 0
  WaveHeight = 0
  WaveLength = 0
  WaveType = 0
  Width = 0
FEATURE [Part::FeaturePython] Panel093  label="Struct spacer 004"  # WARN: FeaturePython — macro-defined, semantics opaque (R4)
  Area = 30741.9
  CloneOf = -> Panel090
  Description = structure spacer
  FaceMaker = 0
  HorizontalArea = 0
  Length = 0
  MoveWithHost = false
  Normal = (0,0,0)
  PerimeterLength = 0
  Placement = pos=(-2.969e-09,-3899.99,1034) rot=(0,0,1;0rad)
  Role = 0
  Sheets = 1
  Tag = S/S
  Thickness = 18
  VerticalArea = 0
  WaveDirection = 0
  WaveHeight = 0
  WaveLength = 0
  WaveType = 0
  Width = 0
FEATURE [Part::FeaturePython] Panel094  label="Struct spacer 005"  # WARN: FeaturePython — macro-defined, semantics opaque (R4)
  Area = 30741.9
  CloneOf = -> Panel090
  Description = structure spacer
  FaceMaker = 0
  HorizontalArea = 0
  Length = 0
  MoveWithHost = false
  Normal = (0,0,0)
  PerimeterLength = 0
  Placement = pos=(1200,0,1034) rot=(0,0,1;0rad)
  Role = 0
  Sheets = 1
  Tag = S/S
  Thickness = 18
  VerticalArea = 0
  WaveDirection = 0
  WaveHeight = 0
  WaveLength = 0
  WaveType = 0
  Width = 0
FEATURE [Part::FeaturePython] Panel095  label="Struct spacer 006"  # WARN: FeaturePython — macro-defined, semantics opaque (R4)
  Area = 30741.9
  CloneOf = -> Panel090
  Description = structure spacer
  FaceMaker = 0
  HorizontalArea = 0
  Length = 0
  MoveWithHost = false
  Normal = (0,0,0)
  PerimeterLength = 0
  Placement = pos=(1200,-9.15552e-05,1634) rot=(0,0,1;0rad)
  Role = 0
  Sheets = 1
  Tag = S/S
  Thickness = 18
  VerticalArea = 0
  WaveDirection = 0
  WaveHeight = 0
  WaveLength = 0
  WaveType = 0
  Width = 0
FEATURE [Part::FeaturePython] Panel096  label="Struct spacer 007"  # WARN: FeaturePython — macro-defined, semantics opaque (R4)
  Area = 30741.9
  CloneOf = -> Panel090
  Description = structure spacer
  FaceMaker = 0
  HorizontalArea = 0
  Length = 0
  MoveWithHost = false
  Normal = (0,0,0)
  PerimeterLength = 0
  Placement = pos=(1200,-3899.99,1634) rot=(0,0,1;0rad)
  Role = 0
  Sheets = 1
  Tag = S/S
  Thickness = 18
  VerticalArea = 0
  WaveDirection = 0
  WaveHeight = 0
  WaveLength = 0
  WaveType = 0
  Width = 0
FEATURE [Part::FeaturePython] Panel097  label="Struct spacer 008"  # WARN: FeaturePython — macro-defined, semantics opaque (R4)
  Area = 30741.9
  CloneOf = -> Panel090
  Description = structure spacer
  FaceMaker = 0
  HorizontalArea = 0
  Length = 0
  MoveWithHost = false
  Normal = (0,0,0)
  PerimeterLength = 0
  Placement = pos=(1200,-3899.99,1034) rot=(0,0,1;0rad)
  Role = 0
  Sheets = 1
  Tag = S/S
  Thickness = 18
  VerticalArea = 0
  WaveDirection = 0
  WaveHeight = 0
  WaveLength = 0
  WaveType = 0
  Width = 0
FEATURE [Part::FeaturePython] Panel098  label="Struct spacer 009"  # WARN: FeaturePython — macro-defined, semantics opaque (R4)
  Area = 30741.9
  CloneOf = -> Panel090
  Description = structure spacer
  FaceMaker = 0
  HorizontalArea = 0
  Length = 0
  MoveWithHost = false
  Normal = (0,0,0)
  PerimeterLength = 0
  Placement = pos=(-2.969e-09,758.998,-1807) rot=(1,0,0;1.5708rad)
  Role = 0
  Sheets = 1
  Tag = S/S
  Thickness = 18
  VerticalArea = 0
  WaveDirection = 0
  WaveHeight = 0
  WaveLength = 0
  WaveType = 0
  Width = 0
FEATURE [Part::FeaturePython] Panel099  label="Struct spacer 010"  # WARN: FeaturePython — macro-defined, semantics opaque (R4)
  Area = 30741.9
  CloneOf = -> Panel090
  Description = structure spacer
  FaceMaker = 0
  HorizontalArea = 0
  Length = 0
  MoveWithHost = false
  Normal = (0,0,0)
  PerimeterLength = 0
  Placement = pos=(-2.969e-09,-740.999,-1807) rot=(1,0,0;1.5708rad)
  Role = 0
  Sheets = 1
  Tag = S/S
  Thickness = 18
  VerticalArea = 0
  WaveDirection = 0
  WaveHeight = 0
  WaveLength = 0
  WaveType = 0
  Width = 0
FEATURE [Part::FeaturePython] Panel100  label="Struct spacer 011"  # WARN: FeaturePython — macro-defined, semantics opaque (R4)
  Area = 30741.9
  CloneOf = -> Panel090
  Description = structure spacer
  FaceMaker = 0
  HorizontalArea = 0
  Length = 0
  MoveWithHost = false
  Normal = (0,0,0)
  PerimeterLength = 0
  Placement = pos=(1200,-740.999,-1807) rot=(1,0,0;1.5708rad)
  Role = 0
  Sheets = 1
  Tag = S/S
  Thickness = 18
  VerticalArea = 0
  WaveDirection = 0
  WaveHeight = 0
  WaveLength = 0
  WaveType = 0
  Width = 0
FEATURE [Part::FeaturePython] Panel101  label="Struct spacer 012"  # WARN: FeaturePython — macro-defined, semantics opaque (R4)
  Area = 30741.9
  CloneOf = -> Panel090
  Description = structure spacer
  FaceMaker = 0
  HorizontalArea = 0
  Length = 0
  MoveWithHost = false
  Normal = (0,0,0)
  PerimeterLength = 0
  Placement = pos=(1200,758.998,-1807) rot=(1,0,0;1.5708rad)
  Role = 0
  Sheets = 1
  Tag = S/S
  Thickness = 18
  VerticalArea = 0
  WaveDirection = 0
  WaveHeight = 0
  WaveLength = 0
  WaveType = 0
  Width = 0
FEATURE [Part::FeaturePython] Panel102  label="Struct spacer 013"  # WARN: FeaturePython — macro-defined, semantics opaque (R4)
  Area = 30741.9
  CloneOf = -> Panel090
  Description = structure spacer
  FaceMaker = 0
  HorizontalArea = 0
  Length = 0
  MoveWithHost = false
  Normal = (0,0,0)
  PerimeterLength = 0
  Placement = pos=(-0.000122068,54.8344,1540.63) rot=(1,0,0;0.9151rad)
  Role = 0
  Sheets = 1
  Tag = S/S
  Thickness = 18
  VerticalArea = 0
  WaveDirection = 0
  WaveHeight = 0
  WaveLength = 0
  WaveType = 0
  Width = 0
FEATURE [Part::FeaturePython] Panel103  label="Struct spacer 014"  # WARN: FeaturePython — macro-defined, semantics opaque (R4)
  Area = 30741.9
  CloneOf = -> Panel090
  Description = structure spacer
  FaceMaker = 0
  HorizontalArea = 0
  Length = 0
  MoveWithHost = false
  Normal = (0,0,0)
  PerimeterLength = 0
  Placement = pos=(-6.10331e-05,-468.441,1943.15) rot=(1,0,0;0.9151rad)
  Role = 0
  Sheets = 1
  Tag = S/S
  Thickness = 18
  VerticalArea = 0
  WaveDirection = 0
  WaveHeight = 0
  WaveLength = 0
  WaveType = 0
  Width = 0
FEATURE [Part::FeaturePython] Panel104  label="Struct spacer 015"  # WARN: FeaturePython — macro-defined, semantics opaque (R4)
  Area = 30741.9
  CloneOf = -> Panel090
  Description = structure spacer
  FaceMaker = 0
  HorizontalArea = 0
  Length = 0
  MoveWithHost = false
  Normal = (0,0,0)
  PerimeterLength = 0
  Placement = pos=(1200,-468.441,1943.15) rot=(1,0,0;0.9151rad)
  Role = 0
  Sheets = 1
  Tag = S/S
  Thickness = 18
  VerticalArea = 0
  WaveDirection = 0
  WaveHeight = 0
  WaveLength = 0
  WaveType = 0
  Width = 0
FEATURE [Part::FeaturePython] Panel105  label="Struct spacer 016"  # WARN: FeaturePython — macro-defined, semantics opaque (R4)
  Area = 30741.9
  CloneOf = -> Panel090
  Description = structure spacer
  FaceMaker = 0
  HorizontalArea = 0
  Length = 0
  MoveWithHost = false
  Normal = (0,0,0)
  PerimeterLength = 0
  Placement = pos=(1200,54.8345,1540.63) rot=(1,0,0;0.9151rad)
  Role = 0
  Sheets = 1
  Tag = S/S
  Thickness = 18
  VerticalArea = 0
  WaveDirection = 0
  WaveHeight = 0
  WaveLength = 0
  WaveType = 0
  Width = 0
FEATURE [Part::FeaturePython] Panel106  label="Struct spacer 017"  # WARN: FeaturePython — macro-defined, semantics opaque (R4)
  Area = 30741.9
  CloneOf = -> Panel090
  Description = structure spacer
  FaceMaker = 0
  HorizontalArea = 0
  Length = 0
  MoveWithHost = false
  Normal = (0,0,0)
  PerimeterLength = 0
  Placement = pos=(-2.969e-09,482.706,1954.13) rot=(1,0,0;2.22649rad)
  Role = 0
  Sheets = 1
  Tag = S/S
  Thickness = 18
  VerticalArea = 0
  WaveDirection = 0
  WaveHeight = 0
  WaveLength = 0
  WaveType = 0
  Width = 0
FEATURE [Part::FeaturePython] Panel107  label="Struct spacer 018"  # WARN: FeaturePython — macro-defined, semantics opaque (R4)
  Area = 30741.9
  CloneOf = -> Panel090
  Description = structure spacer
  FaceMaker = 0
  HorizontalArea = 0
  Length = 0
  MoveWithHost = false
  Normal = (0,0,0)
  PerimeterLength = 0
  Placement = pos=(-2.969e-09,-40.5711,1551.61) rot=(1,0,0;2.22649rad)
  Role = 0
  Sheets = 1
  Tag = S/S
  Thickness = 18
  VerticalArea = 0
  WaveDirection = 0
  WaveHeight = 0
  WaveLength = 0
  WaveType = 0
  Width = 0
FEATURE [Part::FeaturePython] Panel108  label="Struct spacer 019"  # WARN: FeaturePython — macro-defined, semantics opaque (R4)
  Area = 30741.9
  CloneOf = -> Panel090
  Description = structure spacer
  FaceMaker = 0
  HorizontalArea = 0
  Length = 0
  MoveWithHost = false
  Normal = (0,0,0)
  PerimeterLength = 0
  Placement = pos=(1200,-40.5711,1551.61) rot=(1,0,0;2.22649rad)
  Role = 0
  Sheets = 1
  Tag = S/S
  Thickness = 18
  VerticalArea = 0
  WaveDirection = 0
  WaveHeight = 0
  WaveLength = 0
  WaveType = 0
  Width = 0
FEATURE [Part::FeaturePython] Panel109  label="Struct spacer 020"  # WARN: FeaturePython — macro-defined, semantics opaque (R4)
  Area = 30741.9
  CloneOf = -> Panel090
  Description = structure spacer
  FaceMaker = 0
  HorizontalArea = 0
  Length = 0
  MoveWithHost = false
  Normal = (0,0,0)
  PerimeterLength = 0
  Placement = pos=(1200,482.706,1954.13) rot=(1,0,0;2.22649rad)
  Role = 0
  Sheets = 1
  Tag = S/S
  Thickness = 18
  VerticalArea = 0
  WaveDirection = 0
  WaveHeight = 0
  WaveLength = 0
  WaveType = 0
  Width = 0
FEATURE [Part::Feature] Wire130
  shape: bbox 150 x 2e-07 x 638.6 mm, 0 faces, 0 solids (baked)
FEATURE [Part::FeaturePython] Panel111  label="Struct outer side small 001"  # WARN: FeaturePython — macro-defined, semantics opaque (R4)
  Area = 55305.8
  Base = -> Wire130
  Description = struct side
  FaceMaker = 0
  HorizontalArea = 0
  Length = 0
  MoveWithHost = false
  Normal = (0,1,0)
  PerimeterLength = 0
  Placement = pos=(0,-18,0) rot=(0,0,1;0rad)
  Role = 0
  Sheets = 1
  Tag = FRA-A/S4/EX
  Thickness = 18
  VerticalArea = 0
  WaveDirection = 0
  WaveHeight = 0
  WaveLength = 0
  WaveType = 0
  Width = 0
FEATURE [Part::Feature] Wire132
  shape: bbox 150 x 2e-07 x 519.9 mm, 0 faces, 0 solids (baked)
FEATURE [Part::FeaturePython] Panel113  label="Struct inner side small 001"  # WARN: FeaturePython — macro-defined, semantics opaque (R4)
  Area = 46044.4
  Base = -> Wire132
  Description = struct side
  FaceMaker = 0
  HorizontalArea = 0
  Length = 0
  MoveWithHost = false
  Normal = (0,1,0)
  PerimeterLength = 0
  Placement = pos=(0,-18,0) rot=(0,0,1;0rad)
  Role = 0
  Sheets = 1
  Tag = FRA-A/S4/IN
  Thickness = 18
  VerticalArea = 0
  WaveDirection = 0
  WaveHeight = 0
  WaveLength = 0
  WaveType = 0
  Width = 0
FEATURE [Part::Feature] Shape034150
  shape: bbox 150 x 668.7 x 2e-07 mm, 0 faces, 0 solids (baked)
FEATURE [Part::FeaturePython] Panel119  label="Struct outer roof small 001"  # WARN: FeaturePython — macro-defined, semantics opaque (R4)
  Area = 57654.4
  Base = -> Shape034150
  Description = struct roof
  FaceMaker = 0
  HorizontalArea = 0
  Length = 0
  MoveWithHost = false
  Normal = (0,0,1)
  PerimeterLength = 0
  Placement = pos=(0,112.069,4091.78) rot=(-1,0,0;0.655695rad)
  Role = 0
  Sheets = 1
  Tag = FRA-A/S6/EX
  Thickness = 18
  VerticalArea = 0
  WaveDirection = 0
  WaveHeight = 0
  WaveLength = 0
  WaveType = 0
  Width = 0
FEATURE [Part::FeaturePython] Panel122  label="Struct inner side small 002"  # WARN: FeaturePython — macro-defined, semantics opaque (R4)
  Area = 46044.4
  CloneOf = -> Panel113
  Description = struct side
  FaceMaker = 0
  HorizontalArea = 0
  Length = 0
  MoveWithHost = false
  Normal = (0,0,0)
  PerimeterLength = 0
  Placement = pos=(0,3649.99,0) rot=(0,0,1;0rad)
  Role = 0
  Sheets = 1
  Tag = FRA-A/S4/IN
  Thickness = 18
  VerticalArea = 0
  WaveDirection = 0
  WaveHeight = 0
  WaveLength = 0
  WaveType = 0
  Width = 0
FEATURE [Part::FeaturePython] Panel123  label="Struct inner side small 003"  # WARN: FeaturePython — macro-defined, semantics opaque (R4)
  Area = 46044.4
  CloneOf = -> Panel113
  Description = struct side
  FaceMaker = 0
  HorizontalArea = 0
  Length = 0
  MoveWithHost = false
  Normal = (0,0,0)
  PerimeterLength = 0
  Placement = pos=(-1200,-18,0) rot=(0,0,1;0rad)
  Role = 0
  Sheets = 1
  Tag = FRA-A/S4/IN
  Thickness = 18
  VerticalArea = 0
  WaveDirection = 0
  WaveHeight = 0
  WaveLength = 0
  WaveType = 0
  Width = 0
FEATURE [Part::FeaturePython] Panel125  label="Struct inner side small 004"  # WARN: FeaturePython — macro-defined, semantics opaque (R4)
  Area = 46044.4
  CloneOf = -> Panel113
  Description = struct side
  FaceMaker = 0
  HorizontalArea = 0
  Length = 0
  MoveWithHost = false
  Normal = (0,0,0)
  PerimeterLength = 0
  Placement = pos=(-1200,3649.99,0) rot=(0,0,1;0rad)
  Role = 0
  Sheets = 1
  Tag = FRA-A/S4/IN
  Thickness = 18
  VerticalArea = 0
  WaveDirection = 0
  WaveHeight = 0
  WaveLength = 0
  WaveType = 0
  Width = 0
FEATURE [Part::FeaturePython] Panel127  label="Struct outer side small 002"  # WARN: FeaturePython — macro-defined, semantics opaque (R4)
  Area = 55305.8
  CloneOf = -> Panel111
  Description = struct side
  FaceMaker = 0
  HorizontalArea = 0
  Length = 0
  MoveWithHost = false
  Normal = (0,0,0)
  PerimeterLength = 0
  Placement = pos=(0,4113.99,0) rot=(0,0,1;0rad)
  Role = 0
  Sheets = 1
  Tag = FRA-A/S4/EX
  Thickness = 18
  VerticalArea = 0
  WaveDirection = 0
  WaveHeight = 0
  WaveLength = 0
  WaveType = 0
  Width = 0
FEATURE [Part::FeaturePython] Panel129  label="Struct outer side small 003"  # WARN: FeaturePython — macro-defined, semantics opaque (R4)
  Area = 55305.8
  CloneOf = -> Panel111
  Description = struct side
  FaceMaker = 0
  HorizontalArea = 0
  Length = 0
  MoveWithHost = false
  Normal = (0,0,0)
  PerimeterLength = 0
  Placement = pos=(-1200,4113.99,0) rot=(0,0,1;0rad)
  Role = 0
  Sheets = 1
  Tag = FRA-A/S4/EX
  Thickness = 18
  VerticalArea = 0
  WaveDirection = 0
  WaveHeight = 0
  WaveLength = 0
  WaveType = 0
  Width = 0
FEATURE [Part::FeaturePython] Panel131  label="Struct outer side small 004"  # WARN: FeaturePython — macro-defined, semantics opaque (R4)
  Area = 55305.8
  CloneOf = -> Panel111
  Description = struct side
  FaceMaker = 0
  HorizontalArea = 0
  Length = 0
  MoveWithHost = false
  Normal = (0,0,0)
  PerimeterLength = 0
  Placement = pos=(-1200,-18,0) rot=(0,0,1;0rad)
  Role = 0
  Sheets = 1
  Tag = FRA-A/S4/EX
  Thickness = 18
  VerticalArea = 0
  WaveDirection = 0
  WaveHeight = 0
  WaveLength = 0
  WaveType = 0
  Width = 0
FEATURE [Part::FeaturePython] Panel139  label="Struct outer roof small 002"  # WARN: FeaturePython — macro-defined, semantics opaque (R4)
  Area = 57654.4
  CloneOf = -> Panel119
  Description = struct roof
  FaceMaker = 0
  HorizontalArea = 0
  Length = 0
  MoveWithHost = false
  Normal = (0,0,0)
  PerimeterLength = 0
  Placement = pos=(1200,-112.069,4091.78) rot=(0,-0.322006,0.946738;3.14159rad)
  Role = 0
  Sheets = 1
  Tag = FRA-A/S6/EX
  Thickness = 18
  VerticalArea = 0
  WaveDirection = 0
  WaveHeight = 0
  WaveLength = 0
  WaveType = 0
  Width = 0
FEATURE [Part::FeaturePython] Panel140  label="Struct outer roof small 003"  # WARN: FeaturePython — macro-defined, semantics opaque (R4)
  Area = 57654.4
  CloneOf = -> Panel119
  Description = struct roof
  FaceMaker = 0
  HorizontalArea = 0
  Length = 0
  MoveWithHost = false
  Normal = (0,0,0)
  PerimeterLength = 0
  Placement = pos=(4e-09,-112.069,4091.78) rot=(0,-0.322006,0.946738;3.14159rad)
  Role = 0
  Sheets = 1
  Tag = FRA-A/S6/EX
  Thickness = 18
  VerticalArea = 0
  WaveDirection = 0
  WaveHeight = 0
  WaveLength = 0
  WaveType = 0
  Width = 0
FEATURE [Part::FeaturePython] Panel141  label="Struct outer roof small 004"  # WARN: FeaturePython — macro-defined, semantics opaque (R4)
  Area = 57654.4
  CloneOf = -> Panel119
  Description = struct roof
  FaceMaker = 0
  HorizontalArea = 0
  Length = 0
  MoveWithHost = false
  Normal = (0,0,0)
  PerimeterLength = 0
  Placement = pos=(-1200,112.069,4091.78) rot=(-1,0,0;0.655695rad)
  Role = 0
  Sheets = 1
  Tag = FRA-A/S6/EX
  Thickness = 18
  VerticalArea = 0
  WaveDirection = 0
  WaveHeight = 0
  WaveLength = 0
  WaveType = 0
  Width = 0
FEATURE [Part::Feature] Wire142
  Placement = pos=(0,-299.999,0) rot=(0,0,1;0rad)
  shape: bbox 46 x 180 x 2e-07 mm, 0 faces, 0 solids (baked)
FEATURE [Part::Feature] Wire143
  Placement = pos=(0,-299.999,0) rot=(0,0,1;0rad)
  shape: bbox 46 x 180 x 2e-07 mm, 0 faces, 0 solids (baked)
FEATURE [Part::Compound] Compound  label="footing base"
  Links = -> [Wire,Wire008,Wire010,Wire002,Wire007,Wire011,Wire009,Wire006,Wire005,Wire012,Wire001,Wire142,Wire143]
FEATURE [Part::FeaturePython] Panel  label="Footing 001"  # WARN: FeaturePython — macro-defined, semantics opaque (R4)
  Area = 421692
  Base = -> Compound
  Description = Footing piece level7
  FaceMaker = 0
  HorizontalArea = 0
  Length = 0
  MoveWithHost = false
  Normal = (0,0,1)
  PerimeterLength = 0
  Role = 0
  Sheets = 1
  Tag = SKI/A
  Thickness = 18
  VerticalArea = 0
  WaveDirection = 0
  WaveHeight = 0
  WaveLength = 0
  WaveType = 0
  Width = 0
FEATURE [Part::FeaturePython] Panel001  label="Footing 002"  # WARN: FeaturePython — macro-defined, semantics opaque (R4)
  Area = 421692
  CloneOf = -> Panel
  Description = Footing piece level7
  FaceMaker = 0
  HorizontalArea = 0
  Length = 0
  MoveWithHost = false
  Normal = (0,0,0)
  PerimeterLength = 0
  Placement = pos=(1200,0,0) rot=(0,0,1;0rad)
  Role = 0
  Sheets = 1
  Tag = SKI/A
  Thickness = 18
  VerticalArea = 0
  WaveDirection = 0
  WaveHeight = 0
  WaveLength = 0
  WaveType = 0
  Width = 0
FEATURE [Part::FeaturePython] Panel002  label="Footing 003"  # WARN: FeaturePython — macro-defined, semantics opaque (R4)
  Area = 421692
  CloneOf = -> Panel
  Description = Footing piece level7
  FaceMaker = 0
  HorizontalArea = 0
  Length = 0
  MoveWithHost = false
  Normal = (0,0,0)
  PerimeterLength = 0
  Placement = pos=(-1200,0,0) rot=(0,0,1;3.14159rad)
  Role = 0
  Sheets = 1
  Tag = SKI/A
  Thickness = 18
  VerticalArea = 0
  WaveDirection = 0
  WaveHeight = 0
  WaveLength = 0
  WaveType = 0
  Width = 0
FEATURE [App::DocumentObjectGroupPython] VisGroup006  label="level7 footing (1 original)"  # scripted group (container) (typed FeaturePython)
  Group = -> [Panel,Panel002]
FEATURE [Part::FeaturePython] Panel003  label="Footing 004"  # WARN: FeaturePython — macro-defined, semantics opaque (R4)
  Area = 421692
  CloneOf = -> Panel
  Description = Footing piece level7
  FaceMaker = 0
  HorizontalArea = 0
  Length = 0
  MoveWithHost = false
  Normal = (0,0,0)
  PerimeterLength = 0
  Placement = pos=(0,0,0) rot=(0,0,1;3.14159rad)
  Role = 0
  Sheets = 1
  Tag = SKI/A
  Thickness = 18
  VerticalArea = 0
  WaveDirection = 0
  WaveHeight = 0
  WaveLength = 0
  WaveType = 0
  Width = 0
FEATURE [Part::Feature] Face002
  shape: bbox 90 x 2e-07 x 23 mm, 1 faces, 0 solids (baked)
FEATURE [Part::Feature] Face004
  shape: bbox 90 x 2e-07 x 23 mm, 1 faces, 0 solids (baked)
FEATURE [Part::Feature] Face005
  shape: bbox 71 x 2e-07 x 180 mm, 1 faces, 0 solids (baked)
FEATURE [Part::Part2DObjectPython] DWire001  # Draft 2D object (typed FeaturePython)
  ChamferSize = 0
  Closed = true
  End = (-573.005,-764,0)
  FilletRadius = 0
  Length = 516
  MakeFace = true
  Points = (20) [(-573.005,-736,0),(-563.005,-736,0),(-563.005,-741,0),(-543.005,-741,0),(-543.005,-670,0),(-548.005,-670,0),(-548.005,-660,0),(-520.005,-660,0),+12 more]
  Start = (-573.005,-736,0)
  Subdivisions = 0
FEATURE [Part::Part2DObjectPython] DWire002  # Draft 2D object (typed FeaturePython)
  ChamferSize = 0
  Closed = true
  End = (-561.005,-1270,0)
  FilletRadius = 0
  Length = 472.001
  MakeFace = true
  Points = (12) [(-566.005,-1270,0),(-566.005,-1260,0),(-520.005,-1260,0),(-520.005,-1270,0),(-525.005,-1270,0),(-525.005,-1430,0),(-520.005,-1430,0),+5 more]
  Start = (-566.005,-1270,0)
  Subdivisions = 0
FEATURE [Part::Part2DObjectPython] DWire003  # Draft 2D object (typed FeaturePython)
  ChamferSize = 0
  Closed = true
  End = (519.993,-1260,0)
  FilletRadius = 0
  Length = 471.997
  MakeFace = true
  Points = (12) [(565.992,-1260,0),(565.992,-1270,0),(560.993,-1270,0),(560.993,-1430,0),(565.992,-1430,0),(565.992,-1440,0),(519.993,-1440,0),(519.993,-1430,0),+4 more]
  Start = (565.992,-1260,0)
  Subdivisions = 0
FEATURE [Part::Part2DObjectPython] DWire004  # Draft 2D object (typed FeaturePython)
  ChamferSize = 0
  Closed = true
  End = (-30.0063,-1036,0)
  FilletRadius = 0
  Length = 235.998
  MakeFace = true
  Points = (12) [(-30.0063,-1041,0),(29.9937,-1041,0),(29.9937,-1036,0),(39.9937,-1036,0),(39.9937,-1049,0),(44.9932,-1049,0),(44.9932,-1059,0),(-45.0063,-1059,0),+4 more]
  Start = (-30.0063,-1041,0)
  Subdivisions = 0
FEATURE [Part::Part2DObjectPython] DWire005  # Draft 2D object (typed FeaturePython)
  ChamferSize = 0
  Closed = true
  End = (-561.005,-1730,0)
  FilletRadius = 0
  Length = 552.003
  MakeFace = true
  Points = (20) [(-561.005,-1570,0),(-566.005,-1570,0),(-566.005,-1560,0),(-520.005,-1560,0),(-520.005,-1570,0),(-525.005,-1570,0),(-525.005,-1641,0),+13 more]
  Start = (-561.005,-1570,0)
  Subdivisions = 0
FEATURE [Part::Part2DObjectPython] DWire006  # Draft 2D object (typed FeaturePython)
  ChamferSize = 0
  Closed = true
  End = (524.992,-1570,0)
  FilletRadius = 0
  Length = 551.998
  MakeFace = true
  Points = (20) [(519.993,-1570,0),(519.993,-1560,0),(565.992,-1560,0),(565.992,-1570,0),(560.993,-1570,0),(560.993,-1730,0),(565.992,-1730,0),(565.992,-1740,0),+12 more]
  Start = (519.993,-1570,0)
  Subdivisions = 0
FEATURE [Part::Part2DObjectPython] DWire007  # Draft 2D object (typed FeaturePython)
  ChamferSize = 0
  Closed = true
  End = (-40.0063,-1636,0)
  FilletRadius = 0
  Length = 235.998
  MakeFace = true
  Points = (12) [(-30.0063,-1636,0),(-30.0063,-1641,0),(29.9937,-1641,0),(29.9937,-1636,0),(39.9937,-1636,0),(39.9937,-1649,0),(44.9932,-1649,0),(44.9932,-1659,0),+4 more]
  Start = (-30.0063,-1636,0)
  Subdivisions = 0
FEATURE [Part::Part2DObjectPython] DWire008  # Draft 2D object (typed FeaturePython)
  ChamferSize = 0
  Closed = true
  End = (-520.005,-959.999,0)
  FilletRadius = 0
  Length = 516
  MakeFace = true
  Points = (20) [(-520.005,-969.999,0),(-525.005,-969.999,0),(-525.005,-1041,0),(-505.005,-1041,0),(-505.005,-1036,0),(-495.005,-1036,0),(-495.005,-1064,0),+13 more]
  Start = (-520.005,-969.999,0)
  Subdivisions = 0
FEATURE [Part::Part2DObjectPython] DWire009  # Draft 2D object (typed FeaturePython)
  ChamferSize = 0
  Closed = true
  End = (547.993,-959.999,0)
  FilletRadius = 0
  Length = 515.999
  MakeFace = true
  Points = (20) [(547.993,-969.999,0),(542.992,-969.999,0),(542.992,-1130,0),(547.993,-1130,0),(547.993,-1140,0),(519.993,-1140,0),(519.993,-1130,0),(524.992,-1130,0),+12 more]
  Start = (547.993,-969.999,0)
  Subdivisions = 0
FEATURE [Part::Part2DObjectPython] DWire010  # Draft 2D object (typed FeaturePython)
  ChamferSize = 0
  Closed = true
  End = (374.993,-2070,0)
  FilletRadius = 0
  Length = 6513.36
  MakeFace = true
  Points = (252) [(374.993,-2093,0),(524.992,-2093,0),(524.992,-1825,0),(599.993,-1825,0),(599.993,-441.25,0),(542.992,-441.25,0),(542.992,-530,0),(547.993,-530,0),+244 more]
  Start = (374.993,-2093,0)
  Subdivisions = 0
FEATURE [Part::Part2DObjectPython] DWire011  # Draft 2D object (typed FeaturePython)
  ChamferSize = 0
  Closed = true
  End = (519.993,-660,0)
  FilletRadius = 0
  Length = 516
  MakeFace = true
  Points = (20) [(547.993,-660,0),(547.993,-670,0),(542.992,-670,0),(542.992,-741,0),(562.992,-741,0),(562.992,-736,0),(572.992,-736,0),(572.992,-764,0),+12 more]
  Start = (547.993,-660,0)
  Subdivisions = 0
FEATURE [Part::Cut] Cut004
  Base = -> DWire010
  Tool = -> DWire001
FEATURE [Part::Cut] Cut005
  Base = -> Cut004
  Tool = -> DWire002
FEATURE [Part::Cut] Cut006
  Base = -> Cut005
  Tool = -> DWire003
FEATURE [Part::Cut] Cut007
  Base = -> Cut006
  Tool = -> DWire004
FEATURE [Part::Cut] Cut008
  Base = -> Cut007
  Tool = -> DWire005
FEATURE [Part::Cut] Cut009
  Base = -> Cut008
  Tool = -> DWire006
FEATURE [Part::Cut] Cut010
  Base = -> Cut009
  Tool = -> DWire007
FEATURE [Part::Cut] Cut011
  Base = -> Cut010
  Tool = -> DWire008
FEATURE [Part::Cut] Cut012
  Base = -> Cut011
  Tool = -> DWire009
FEATURE [Part::Cut] Cut013
  Base = -> Cut012
  Placement = pos=(0,0,285.999) rot=(0,0,1;0rad)
  Tool = -> DWire011
FEATURE [Part::FeaturePython] Panel147  label="Floor inner"  # WARN: FeaturePython — macro-defined, semantics opaque (R4)
  Area = 1.87065e+06
  Base = -> Cut013
  FaceMaker = 0
  HorizontalArea = 0
  Length = 0
  MoveWithHost = false
  Normal = (0,0,0)
  PerimeterLength = 0
  Placement = pos=(0,0,-18) rot=(0,0,1;0rad)
  Role = 0
  Sheets = 1
  Tag = W1
  Thickness = 18
  VerticalArea = 0
  WaveDirection = 0
  WaveHeight = 0
  WaveLength = 0
  WaveType = 0
  Width = 0
FEATURE [Part::FeaturePython] PanelView023  label="View of Struct spacer 005"  # WARN: FeaturePython — macro-defined, semantics opaque (R4)
  FontFile = <userpath>/.fonts/stick/1CamBam_Stick_2.ttf
  MakeFace = true
  Placement = pos=(900,0,0) rot=(0,0,1;0rad)
  Source = -> Panel094
  TagPosition = (0,0,0)
  TagRotation = 0
  TagSize = 10
  TagText = %tag%
FEATURE [Part::FeaturePython] PanelView024  label="View of Struct spacer 006"  # WARN: FeaturePython — macro-defined, semantics opaque (R4)
  FontFile = <userpath>/.fonts/stick/1CamBam_Stick_2.ttf
  MakeFace = true
  Placement = pos=(900,400,0) rot=(0,0,1;0rad)
  Source = -> Panel095
  TagPosition = (0,0,0)
  TagRotation = 0
  TagSize = 10
  TagText = %tag%
FEATURE [Part::FeaturePython] PanelView025  label="View of Struct spacer 007"  # WARN: FeaturePython — macro-defined, semantics opaque (R4)
  FontFile = <userpath>/.fonts/stick/1CamBam_Stick_2.ttf
  MakeFace = true
  Placement = pos=(900,800,0) rot=(0,0,1;0rad)
  Source = -> Panel096
  TagPosition = (0,0,0)
  TagRotation = 0
  TagSize = 10
  TagText = %tag%
FEATURE [Part::FeaturePython] PanelView026  label="View of Struct spacer 008"  # WARN: FeaturePython — macro-defined, semantics opaque (R4)
  FontFile = <userpath>/.fonts/stick/1CamBam_Stick_2.ttf
  MakeFace = true
  Placement = pos=(900,1200,0) rot=(0,0,1;0rad)
  Source = -> Panel097
  TagPosition = (0,0,0)
  TagRotation = 0
  TagSize = 10
  TagText = %tag%
FEATURE [Part::FeaturePython] PanelView027  label="View of Struct spacer 011"  # WARN: FeaturePython — macro-defined, semantics opaque (R4)
  FontFile = <userpath>/.fonts/stick/1CamBam_Stick_2.ttf
  MakeFace = true
  Placement = pos=(900,-400,0) rot=(0,0,1;0rad)
  Source = -> Panel100
  TagPosition = (0,0,0)
  TagRotation = 0
  TagSize = 10
  TagText = %tag%
FEATURE [Part::FeaturePython] PanelView028  label="View of Struct spacer 012"  # WARN: FeaturePython — macro-defined, semantics opaque (R4)
  FontFile = <userpath>/.fonts/stick/1CamBam_Stick_2.ttf
  MakeFace = true
  Placement = pos=(900,-800,0) rot=(0,0,1;0rad)
  Source = -> Panel101
  TagPosition = (0,0,0)
  TagRotation = 0
  TagSize = 10
  TagText = %tag%
FEATURE [Part::FeaturePython] PanelView029  label="View of Struct spacer 015"  # WARN: FeaturePython — macro-defined, semantics opaque (R4)
  FontFile = <userpath>/.fonts/stick/1CamBam_Stick_2.ttf
  MakeFace = true
  Placement = pos=(900,1600,0) rot=(0,0,1;0rad)
  Source = -> Panel104
  TagPosition = (0,0,0)
  TagRotation = 0
  TagSize = 10
  TagText = %tag%
FEATURE [Part::FeaturePython] PanelView030  label="View of Struct spacer 016"  # WARN: FeaturePython — macro-defined, semantics opaque (R4)
  FontFile = <userpath>/.fonts/stick/1CamBam_Stick_2.ttf
  MakeFace = true
  Placement = pos=(900,2000,0) rot=(0,0,1;0rad)
  Source = -> Panel105
  TagPosition = (0,0,0)
  TagRotation = 0
  TagSize = 10
  TagText = %tag%
FEATURE [Part::FeaturePython] PanelView031  label="View of Struct spacer 019"  # WARN: FeaturePython — macro-defined, semantics opaque (R4)
  FontFile = <userpath>/.fonts/stick/1CamBam_Stick_2.ttf
  MakeFace = true
  Placement = pos=(900,2400,0) rot=(0,0,1;0rad)
  Source = -> Panel108
  TagPosition = (0,0,0)
  TagRotation = 0
  TagSize = 10
  TagText = %tag%
FEATURE [Part::FeaturePython] PanelView032  label="View of Struct spacer 020"  # WARN: FeaturePython — macro-defined, semantics opaque (R4)
  FontFile = <userpath>/.fonts/stick/1CamBam_Stick_2.ttf
  MakeFace = true
  Placement = pos=(900,2800,0) rot=(0,0,1;0rad)
  Source = -> Panel109
  TagPosition = (0,0,0)
  TagRotation = 0
  TagSize = 10
  TagText = %tag%
FEATURE [Part::FeaturePython] PanelView034  label="View of Struct outer side small 001"  # WARN: FeaturePython — macro-defined, semantics opaque (R4)
  FontFile = <userpath>/.fonts/stick/1CamBam_Stick_2.ttf
  MakeFace = true
  Placement = pos=(3256.3,283.799,0) rot=(0,0,1;0rad)
  Source = -> Panel111
  TagPosition = (0,0,0)
  TagRotation = 90
  TagSize = 10
  TagText = %tag%
FEATURE [Part::FeaturePython] PanelView036  label="View of Struct inner side small 001"  # WARN: FeaturePython — macro-defined, semantics opaque (R4)
  FontFile = <userpath>/.fonts/stick/1CamBam_Stick_2.ttf
  MakeFace = true
  Placement = pos=(3260.36,1718.13,0) rot=(0,0,1;0rad)
  Source = -> Panel113
  TagPosition = (0,0,0)
  TagRotation = 90
  TagSize = 10
  TagText = %tag%
FEATURE [Part::FeaturePython] PanelView042  label="View of Struct outer roof small 001"  # WARN: FeaturePython — macro-defined, semantics opaque (R4)
  FontFile = <userpath>/.fonts/stick/1CamBam_Stick_2.ttf
  MakeFace = true
  Placement = pos=(-5000,200,0) rot=(0,0,1;0rad)
  Source = -> Panel119
  TagPosition = (0,0,0)
  TagRotation = 90
  TagSize = 10
  TagText = %tag%
FEATURE [Part::FeaturePython] PanelView045  label="View of Struct inner side small 002"  # WARN: FeaturePython — macro-defined, semantics opaque (R4)
  FontFile = <userpath>/.fonts/stick/1CamBam_Stick_2.ttf
  MakeFace = true
  Placement = pos=(3239.02,1096.79,0) rot=(0,0,1;0rad)
  Source = -> Panel122
  TagPosition = (0,0,0)
  TagRotation = 90
  TagSize = 10
  TagText = %tag%
FEATURE [Part::FeaturePython] PanelView046  label="View of Struct outer side small 002"  # WARN: FeaturePython — macro-defined, semantics opaque (R4)
  FontFile = <userpath>/.fonts/stick/1CamBam_Stick_2.ttf
  MakeFace = true
  Placement = pos=(0,800,0) rot=(0,0,1;0rad)
  Source = -> Panel127
  TagPosition = (0,0,0)
  TagRotation = 90
  TagSize = 10
  TagText = %tag%
FEATURE [Part::FeaturePython] PanelView049  label="View of Struct outer roof small 002"  # WARN: FeaturePython — macro-defined, semantics opaque (R4)
  FontFile = <userpath>/.fonts/stick/1CamBam_Stick_2.ttf
  MakeFace = true
  Source = -> Panel139
  TagPosition = (0,0,0)
  TagRotation = 90
  TagSize = 10
  TagText = %tag%
FEATURE [Part::FeaturePython] PanelView072  label="View of Struct spacer 002"  # WARN: FeaturePython — macro-defined, semantics opaque (R4)
  FontFile = <userpath>/.fonts/stick/1CamBam_Stick_2.ttf
  MakeFace = false
  Placement = pos=(0,399.837,11.4139) rot=(0,0,1;0rad)
  Source = -> Panel091
  TagPosition = (0,0,0)
  TagRotation = 0
  TagSize = 10
  TagText = %tag%
FEATURE [Part::FeaturePython] PanelView073  label="View of Struct spacer 001"  # WARN: FeaturePython — macro-defined, semantics opaque (R4)
  FontFile = <userpath>/.fonts/stick/1CamBam_Stick_2.ttf
  MakeFace = false
  Placement = pos=(0,799.674,22.8278) rot=(0,0,1;0rad)
  Source = -> Panel090
  TagPosition = (0,0,0)
  TagRotation = 0
  TagSize = 10
  TagText = %tag%
FEATURE [Part::FeaturePython] PanelView074  label="View of Struct spacer 003"  # WARN: FeaturePython — macro-defined, semantics opaque (R4)
  FontFile = <userpath>/.fonts/stick/1CamBam_Stick_2.ttf
  MakeFace = false
  Placement = pos=(0,-799.674,-22.8278) rot=(0,0,1;0rad)
  Source = -> Panel092
  TagPosition = (0,0,0)
  TagRotation = 0
  TagSize = 10
  TagText = %tag%
FEATURE [Part::FeaturePython] PanelView075  label="View of Struct spacer 004"  # WARN: FeaturePython — macro-defined, semantics opaque (R4)
  FontFile = <userpath>/.fonts/stick/1CamBam_Stick_2.ttf
  MakeFace = false
  Placement = pos=(0,-399.837,-11.4139) rot=(0,0,1;0rad)
  Source = -> Panel093
  TagPosition = (0,0,0)
  TagRotation = 0
  TagSize = 10
  TagText = %tag%
FEATURE [Part::FeaturePython] PanelView076  label="View of Struct spacer 009"  # WARN: FeaturePython — macro-defined, semantics opaque (R4)
  FontFile = <userpath>/.fonts/stick/1CamBam_Stick_2.ttf
  MakeFace = false
  Placement = pos=(-1000,-199.919,-5.70695) rot=(0,0,1;0rad)
  Source = -> Panel098
  TagPosition = (0,0,0)
  TagRotation = 0
  TagSize = 10
  TagText = %tag%
FEATURE [Part::FeaturePython] PanelView077  label="View of Struct spacer 010"  # WARN: FeaturePython — macro-defined, semantics opaque (R4)
  FontFile = <userpath>/.fonts/stick/1CamBam_Stick_2.ttf
  MakeFace = false
  Placement = pos=(-1000,-599.756,-17.1208) rot=(0,0,1;0rad)
  Source = -> Panel099
  TagPosition = (0,0,0)
  TagRotation = 0
  TagSize = 10
  TagText = %tag%
FEATURE [Part::FeaturePython] PanelView078  label="View of Struct spacer 013"  # WARN: FeaturePython — macro-defined, semantics opaque (R4)
  FontFile = <userpath>/.fonts/stick/1CamBam_Stick_2.ttf
  MakeFace = false
  Placement = pos=(-1000,-999.593,-28.5347) rot=(0,0,1;0rad)
  Source = -> Panel102
  TagPosition = (0,0,0)
  TagRotation = 0
  TagSize = 10
  TagText = %tag%
FEATURE [Part::FeaturePython] PanelView079  label="View of Struct spacer 014"  # WARN: FeaturePython — macro-defined, semantics opaque (R4)
  FontFile = <userpath>/.fonts/stick/1CamBam_Stick_2.ttf
  MakeFace = false
  Source = -> Panel103
  TagPosition = (0,0,0)
  TagRotation = 0
  TagSize = 10
  TagText = %tag%
FEATURE [Part::FeaturePython] PanelView080  label="View of Struct spacer 017"  # WARN: FeaturePython — macro-defined, semantics opaque (R4)
  FontFile = <userpath>/.fonts/stick/1CamBam_Stick_2.ttf
  MakeFace = false
  Placement = pos=(-1000,-1799.27,-51.3625) rot=(0,0,1;0rad)
  Source = -> Panel106
  TagPosition = (0,0,0)
  TagRotation = 0
  TagSize = 10
  TagText = %tag%
FEATURE [Part::FeaturePython] PanelView081  label="View of Struct spacer 018"  # WARN: FeaturePython — macro-defined, semantics opaque (R4)
  FontFile = <userpath>/.fonts/stick/1CamBam_Stick_2.ttf
  MakeFace = false
  Placement = pos=(-1000,-1399.43,-39.9486) rot=(0,0,1;0rad)
  Source = -> Panel107
  TagPosition = (0,0,0)
  TagRotation = 0
  TagSize = 10
  TagText = %tag%
FEATURE [Part::FeaturePython] PanelView082  label="View of Struct inner side small 003"  # WARN: FeaturePython — macro-defined, semantics opaque (R4)
  FontFile = <userpath>/.fonts/stick/1CamBam_Stick_2.ttf
  MakeFace = false
  Placement = pos=(-5100,-1099.55,-31.3971) rot=(0,0,1;0rad)
  Source = -> Panel123
  TagPosition = (0,0,0)
  TagRotation = 90
  TagSize = 10
  TagText = %tag%
FEATURE [Part::FeaturePython] PanelView084  label="View of Struct inner side small 004"  # WARN: FeaturePython — macro-defined, semantics opaque (R4)
  FontFile = <userpath>/.fonts/stick/1CamBam_Stick_2.ttf
  MakeFace = false
  Placement = pos=(-5300,-1299.47,-37.1057) rot=(0,0,1;0rad)
  Source = -> Panel125
  TagPosition = (0,0,0)
  TagRotation = 90
  TagSize = 10
  TagText = %tag%
FEATURE [Part::FeaturePython] PanelView086  label="View of Struct outer side small 003"  # WARN: FeaturePython — macro-defined, semantics opaque (R4)
  FontFile = <userpath>/.fonts/stick/1CamBam_Stick_2.ttf
  MakeFace = false
  Placement = pos=(-5600,-1499.39,-42.8142) rot=(0,0,1;0rad)
  Source = -> Panel129
  TagPosition = (0,0,0)
  TagRotation = 90
  TagSize = 10
  TagText = %tag%
FEATURE [Part::FeaturePython] PanelView088  label="View of Struct outer side small 004"  # WARN: FeaturePython — macro-defined, semantics opaque (R4)
  FontFile = <userpath>/.fonts/stick/1CamBam_Stick_2.ttf
  MakeFace = false
  Placement = pos=(-6000,-1399.43,-39.9599) rot=(0,0,1;0rad)
  Source = -> Panel131
  TagPosition = (0,0,0)
  TagRotation = 90
  TagSize = 10
  TagText = %tag%
FEATURE [Part::FeaturePython] PanelView094  label="View of Struct outer roof small 003"  # WARN: FeaturePython — macro-defined, semantics opaque (R4)
  FontFile = <userpath>/.fonts/stick/1CamBam_Stick_2.ttf
  MakeFace = false
  Placement = pos=(-6300,-1099.55,-31.3971) rot=(0,0,1;0rad)
  Source = -> Panel140
  TagPosition = (0,0,0)
  TagRotation = 90
  TagSize = 10
  TagText = %tag%
FEATURE [Part::FeaturePython] PanelView095  label="View of Struct outer roof small 004"  # WARN: FeaturePython — macro-defined, semantics opaque (R4)
  FontFile = <userpath>/.fonts/stick/1CamBam_Stick_2.ttf
  MakeFace = false
  Placement = pos=(-6700,-999.593,-28.5428) rot=(0,0,1;0rad)
  Source = -> Panel141
  TagPosition = (0,0,0)
  TagRotation = 90
  TagSize = 10
  TagText = %tag%
FEATURE [Part::FeaturePython] PanelView100  label="View of Spacer 001"  # WARN: FeaturePython — macro-defined, semantics opaque (R4)
  FontFile = <userpath>/.fonts/stick/1CamBam_Stick_2.ttf
  MakeFace = false
  Placement = pos=(-600,2998.78,85.6285) rot=(0,0,1;0rad)
  Source = -> Panel034
  TagPosition = (0,0,0)
  TagRotation = 0
  TagSize = 10
  TagText = %tag%
FEATURE [Part::FeaturePython] PanelView101  label="View of Spacer 002"  # WARN: FeaturePython — macro-defined, semantics opaque (R4)
  FontFile = <userpath>/.fonts/stick/1CamBam_Stick_2.ttf
  MakeFace = false
  Placement = pos=(2700,3398.61,97.0456) rot=(0,0,1;0rad)
  Source = -> Panel035
  TagPosition = (0,0,0)
  TagRotation = 0
  TagSize = 10
  TagText = %tag%
FEATURE [Part::FeaturePython] PanelView102  label="View of Spacer 003"  # WARN: FeaturePython — macro-defined, semantics opaque (R4)
  FontFile = <userpath>/.fonts/stick/1CamBam_Stick_2.ttf
  MakeFace = false
  Placement = pos=(-2000,3698.49,105.608) rot=(0,0,1;0rad)
  Source = -> Panel036
  TagPosition = (0,0,0)
  TagRotation = 0
  TagSize = 10
  TagText = %tag%
FEATURE [Part::FeaturePython] PanelView103  label="View of Spacer 004"  # WARN: FeaturePython — macro-defined, semantics opaque (R4)
  FontFile = <userpath>/.fonts/stick/1CamBam_Stick_2.ttf
  MakeFace = false
  Placement = pos=(6200,2998.78,85.6285) rot=(0,0,1;0rad)
  Source = -> Panel037
  TagPosition = (0,0,0)
  TagRotation = 0
  TagSize = 10
  TagText = %tag%
FEATURE [Part::FeaturePython] PanelView104  label="View of Spacer 005"  # WARN: FeaturePython — macro-defined, semantics opaque (R4)
  FontFile = <userpath>/.fonts/stick/1CamBam_Stick_2.ttf
  MakeFace = false
  Placement = pos=(6100,3498.57,99.8999) rot=(0,0,1;0rad)
  Source = -> Panel038
  TagPosition = (0,0,0)
  TagRotation = 0
  TagSize = 10
  TagText = %tag%
FEATURE [Part::FeaturePython] PanelView105  label="View of Spacer 006"  # WARN: FeaturePython — macro-defined, semantics opaque (R4)
  FontFile = <userpath>/.fonts/stick/1CamBam_Stick_2.ttf
  MakeFace = false
  Placement = pos=(4600,3698.49,105.608) rot=(0,0,1;0rad)
  Source = -> Panel039
  TagPosition = (0,0,0)
  TagRotation = 0
  TagSize = 10
  TagText = %tag%
FEATURE [Part::FeaturePython] PanelView106  label="View of Spacer 007"  # WARN: FeaturePython — macro-defined, semantics opaque (R4)
  FontFile = <userpath>/.fonts/stick/1CamBam_Stick_2.ttf
  MakeFace = false
  Placement = pos=(2800,3898.41,111.317) rot=(0,0,1;0rad)
  Source = -> Panel040
  TagPosition = (0,0,0)
  TagRotation = 0
  TagSize = 10
  TagText = %tag%
FEATURE [Part::FeaturePython] PanelView107  label="View of Spacer 008"  # WARN: FeaturePython — macro-defined, semantics opaque (R4)
  FontFile = <userpath>/.fonts/stick/1CamBam_Stick_2.ttf
  MakeFace = false
  Placement = pos=(1000,3998.37,114.171) rot=(0,0,1;0rad)
  Source = -> Panel041
  TagPosition = (0,0,0)
  TagRotation = 0
  TagSize = 10
  TagText = %tag%
FEATURE [Part::FeaturePython] PanelView108  label="View of Spacer 009"  # WARN: FeaturePython — macro-defined, semantics opaque (R4)
  FontFile = <userpath>/.fonts/stick/1CamBam_Stick_2.ttf
  MakeFace = false
  Placement = pos=(1100,3498.57,99.8999) rot=(0,0,1;0rad)
  Source = -> Panel042
  TagPosition = (0,0,0)
  TagRotation = 0
  TagSize = 10
  TagText = %tag%
FEATURE [Part::FeaturePython] PanelView109  label="View of Spacer 010"  # WARN: FeaturePython — macro-defined, semantics opaque (R4)
  FontFile = <userpath>/.fonts/stick/1CamBam_Stick_2.ttf
  MakeFace = false
  Placement = pos=(2700,2998.78,85.6285) rot=(0,0,1;0rad)
  Source = -> Panel043
  TagPosition = (0,0,0)
  TagRotation = 0
  TagSize = 10
  TagText = %tag%
FEATURE [Part::FeaturePython] PanelView110  label="View of Spacer 011"  # WARN: FeaturePython — macro-defined, semantics opaque (R4)
  FontFile = <userpath>/.fonts/stick/1CamBam_Stick_2.ttf
  MakeFace = false
  Placement = pos=(-500,3498.57,99.8999) rot=(0,0,1;0rad)
  Source = -> Panel044
  TagPosition = (0,0,0)
  TagRotation = 0
  TagSize = 10
  TagText = %tag%
FEATURE [Part::FeaturePython] PanelView111  label="View of Lock 001"  # WARN: FeaturePython — macro-defined, semantics opaque (R4)
  FontFile = <userpath>/.fonts/stick/1CamBam_Stick_2.ttf
  MakeFace = false
  Placement = pos=(0,1399.43,39.9486) rot=(0,0,1;0rad)
  Source = -> Panel045
  TagPosition = (-7.37363,35.333,1.00863)
  TagRotation = 0
  TagSize = 10
  TagText = %tag%
FEATURE [Part::FeaturePython] PanelView112  label="View of Lock 002"  # WARN: FeaturePython — macro-defined, semantics opaque (R4)
  FontFile = <userpath>/.fonts/stick/1CamBam_Stick_2.ttf
  MakeFace = false
  Placement = pos=(300,1399.43,39.9486) rot=(0,0,1;0rad)
  Source = -> Panel046
  TagPosition = (-12.8195,39.4302,1.12559)
  TagRotation = 0
  TagSize = 10
  TagText = %tag%
FEATURE [Part::FeaturePython] PanelView113  label="View of Lock 003"  # WARN: FeaturePython — macro-defined, semantics opaque (R4)
  FontFile = <userpath>/.fonts/stick/1CamBam_Stick_2.ttf
  MakeFace = false
  Placement = pos=(600,1399.43,39.9486) rot=(0,0,1;0rad)
  Source = -> Panel047
  TagPosition = (-16.6915,39.4434,1.12596)
  TagRotation = 0
  TagSize = 10
  TagText = %tag%
FEATURE [Part::FeaturePython] PanelView114  label="View of Lock 004"  # WARN: FeaturePython — macro-defined, semantics opaque (R4)
  FontFile = <userpath>/.fonts/stick/1CamBam_Stick_2.ttf
  MakeFace = false
  Placement = pos=(900,1399.43,39.9486) rot=(0,0,1;0rad)
  Source = -> Panel048
  TagPosition = (-14.4148,37.3303,1.06565)
  TagRotation = 0
  TagSize = 10
  TagText = %tag%
FEATURE [Part::FeaturePython] PanelView115  label="View of Bottom panel small 001"  # WARN: FeaturePython — macro-defined, semantics opaque (R4)
  FontFile = <userpath>/.fonts/stick/1CamBam_Stick_2.ttf
  MakeFace = false
  Placement = pos=(1100,2998.78,85.6285) rot=(0,0,1;0rad)
  Source = -> Panel073
  TagPosition = (0,0,0)
  TagRotation = 0
  TagSize = 10
  TagText = %tag%
FEATURE [Part::FeaturePython] PanelView116  label="View of Bottom lock 002"  # WARN: FeaturePython — macro-defined, semantics opaque (R4)
  FontFile = <userpath>/.fonts/stick/1CamBam_Stick_2.ttf
  MakeFace = false
  Placement = pos=(4500,2898.82,82.7742) rot=(0,0,1;0rad)
  Source = -> Panel085
  TagPosition = (0,0,0)
  TagRotation = 0
  TagSize = 10
  TagText = %tag%
FEATURE [Part::FeaturePython] PanelView117  label="View of Bottom panel small 002"  # WARN: FeaturePython — macro-defined, semantics opaque (R4)
  FontFile = <userpath>/.fonts/stick/1CamBam_Stick_2.ttf
  MakeFace = false
  Placement = pos=(-2100,3198.7,91.337) rot=(0,0,1;0rad)
  Source = -> Panel084
  TagPosition = (0,0,0)
  TagRotation = 0
  TagSize = 10
  TagText = %tag%
FEATURE [Part::FeaturePython] PanelView118  label="View of Bottom panel medium 001"  # WARN: FeaturePython — macro-defined, semantics opaque (R4)
  FontFile = <userpath>/.fonts/stick/1CamBam_Stick_2.ttf
  MakeFace = false
  Placement = pos=(1900,2199.1,62.7942) rot=(0,0,1;0rad)
  Source = -> Panel074
  TagPosition = (0,0,0)
  TagRotation = 0
  TagSize = 10
  TagText = %tag%
FEATURE [Part::FeaturePython] PanelView119  label="View of Bottom panel large 001"  # WARN: FeaturePython — macro-defined, semantics opaque (R4)
  FontFile = <userpath>/.fonts/stick/1CamBam_Stick_2.ttf
  MakeFace = false
  Placement = pos=(-2100,-2900,0) rot=(0,0,1;0rad)
  Source = -> Panel075
  TagPosition = (0,0,0)
  TagRotation = 0
  TagSize = 10
  TagText = %tag%
FEATURE [Part::FeaturePython] PanelView120  label="View of Bottom lock 001"  # WARN: FeaturePython — macro-defined, semantics opaque (R4)
  FontFile = <userpath>/.fonts/stick/1CamBam_Stick_2.ttf
  MakeFace = false
  Placement = pos=(4600,3298.66,94.1913) rot=(0,0,1;0rad)
  Source = -> Panel076
  TagPosition = (0,0,0)
  TagRotation = 0
  TagSize = 10
  TagText = %tag%
FEATURE [Part::FeaturePython] PanelView121  label="View of Outer roof panel large 001"  # WARN: FeaturePython — macro-defined, semantics opaque (R4)
  FontFile = <userpath>/.fonts/stick/1CamBam_Stick_2.ttf
  MakeFace = false
  Placement = pos=(6800,0,0) rot=(0,0,1;0rad)
  Source = -> Panel079
  TagPosition = (0,0,0)
  TagRotation = 0
  TagSize = 10
  TagText = %tag%
FEATURE [Part::FeaturePython] PanelView123  label="View of Bottom panel medium 002"  # WARN: FeaturePython — macro-defined, semantics opaque (R4)
  FontFile = <userpath>/.fonts/stick/1CamBam_Stick_2.ttf
  MakeFace = false
  Placement = pos=(3300,2299.06,65.6485) rot=(0,0,1;0rad)
  Source = -> Panel081
  TagPosition = (0,0,0)
  TagRotation = 0
  TagSize = 10
  TagText = %tag%
FEATURE [Part::FeaturePython] PanelView124  label="View of Bottom panel medium 003"  # WARN: FeaturePython — macro-defined, semantics opaque (R4)
  FontFile = <userpath>/.fonts/stick/1CamBam_Stick_2.ttf
  MakeFace = false
  Placement = pos=(-1000,2399.02,68.5028) rot=(0,0,1;0rad)
  Source = -> Panel082
  TagPosition = (0,0,0)
  TagRotation = 0
  TagSize = 10
  TagText = %tag%
FEATURE [Part::FeaturePython] PanelView125  label="View of Bottom panel medium 004"  # WARN: FeaturePython — macro-defined, semantics opaque (R4)
  FontFile = <userpath>/.fonts/stick/1CamBam_Stick_2.ttf
  MakeFace = false
  Placement = pos=(-2300,2498.98,71.357) rot=(0,0,1;0rad)
  Source = -> Panel083
  TagPosition = (0,0,0)
  TagRotation = 0
  TagSize = 10
  TagText = %tag%
FEATURE [Part::FeaturePython] PanelView126  label="View of Outer side panel small 002"  # WARN: FeaturePython — macro-defined, semantics opaque (R4)
  FontFile = <userpath>/.fonts/stick/1CamBam_Stick_2.ttf
  MakeFace = false
  Placement = pos=(6400,2299.06,65.6485) rot=(0,0,1;0rad)
  Source = -> Panel086
  TagPosition = (0,0,0)
  TagRotation = 0
  TagSize = 10
  TagText = %tag%
FEATURE [Part::FeaturePython] PanelView127  label="View of Outer side panel large 002"  # WARN: FeaturePython — macro-defined, semantics opaque (R4)
  FontFile = <userpath>/.fonts/stick/1CamBam_Stick_2.ttf
  MakeFace = false
  Placement = pos=(1600,-2400,0) rot=(0,0,1;0rad)
  Source = -> Panel087
  TagPosition = (0,0,0)
  TagRotation = 0
  TagSize = 10
  TagText = %tag%
FEATURE [Part::FeaturePython] PanelView129  label="View of Outer roof panel large 002"  # WARN: FeaturePython — macro-defined, semantics opaque (R4)
  FontFile = <userpath>/.fonts/stick/1CamBam_Stick_2.ttf
  MakeFace = false
  Placement = pos=(2900,-2400,0) rot=(0,0,1;0rad)
  Source = -> Panel089
  TagPosition = (0,0,0)
  TagRotation = 0
  TagSize = 10
  TagText = %tag%
FEATURE [Part::FeaturePython] PanelView130  label="View of Floor panel large 001"  # WARN: FeaturePython — macro-defined, semantics opaque (R4)
  FontFile = <userpath>/.fonts/stick/1CamBam_Stick_2.ttf
  MakeFace = false
  Placement = pos=(1600,0,0) rot=(0,0,1;0rad)
  Source = -> Panel029
  TagPosition = (0,0,0)
  TagRotation = 0
  TagSize = 10
  TagText = %tag%
FEATURE [Part::FeaturePython] PanelView134  label="View of Footing 001"  # WARN: FeaturePython — macro-defined, semantics opaque (R4)
  FontFile = <userpath>/.fonts/stick/1CamBam_Stick_2.ttf
  MakeFace = false
  Placement = pos=(9000,599.756,17.1257) rot=(0,0,1;0rad)
  Source = -> Panel
  TagPosition = (-0.246094,-60.2176,-17.1257)
  TagRotation = 0
  TagSize = 10
  TagText = %tag%
FEATURE [Part::FeaturePython] PanelView135  label="View of Footing 003"  # WARN: FeaturePython — macro-defined, semantics opaque (R4)
  FontFile = <userpath>/.fonts/stick/1CamBam_Stick_2.ttf
  MakeFace = false
  Placement = pos=(8600,599.756,17.1257) rot=(0,0,1;0rad)
  Source = -> Panel002
  TagPosition = (2.17969,-62.6873,-17.1257)
  TagRotation = 0
  TagSize = 10
  TagText = %tag%
FEATURE [Part::FeaturePython] PanelView136  label="View of Footing 002"  # WARN: FeaturePython — macro-defined, semantics opaque (R4)
  FontFile = <userpath>/.fonts/stick/1CamBam_Stick_2.ttf
  MakeFace = true
  Placement = pos=(6500,300,0) rot=(0,0,1;0rad)
  Source = -> Panel001
  TagPosition = (-2.34521,-68.1539,0)
  TagRotation = 0
  TagSize = 10
  TagText = %tag%
FEATURE [Part::FeaturePython] PanelView137  label="View of Footing 004"  # WARN: FeaturePython — macro-defined, semantics opaque (R4)
  FontFile = <userpath>/.fonts/stick/1CamBam_Stick_2.ttf
  MakeFace = true
  Placement = pos=(6100,300,0) rot=(0,0,1;0rad)
  Source = -> Panel003
  TagPosition = (1.76904,-65.6387,0)
  TagRotation = 0
  TagSize = 10
  TagText = %tag%
FEATURE [App::DocumentObjectGroupPython] VisGroup012  label="Endcap skis (0 original)"  # scripted group (container) (typed FeaturePython)
  Group = -> [Panel001,Panel003]
FEATURE [Part::FeaturePython] PanelView140  label="View of Floor inner"  # WARN: FeaturePython — macro-defined, semantics opaque (R4)
  FontFile = <userpath>/.fonts/stick/1CamBam_Stick_2.ttf
  MakeFace = false
  Placement = pos=(7500,-2400,0) rot=(0,0,1;0rad)
  Source = -> Panel147
  TagPosition = (0,0,0)
  TagRotation = 0
  TagSize = 10
  TagText = %tag%
FEATURE [Part::FeaturePython] PanelView143  label="View of Footing 005"  # WARN: FeaturePython — macro-defined, semantics opaque (R4)
  FontFile = <userpath>/.fonts/stick/1CamBam_Stick_2.ttf
  MakeFace = false
  Placement = pos=(-4000,0,0) rot=(0,0,1;0rad)
  Source = -> Panel
  TagPosition = (2.50415,-63.2896,0)
  TagRotation = 0
  TagSize = 10
  TagText = %tag%
FEATURE [Part::FeaturePython] PanelView144  label="View of Footing 006"  # WARN: FeaturePython — macro-defined, semantics opaque (R4)
  FontFile = <userpath>/.fonts/stick/1CamBam_Stick_2.ttf
  MakeFace = false
  Placement = pos=(-4300,0,0) rot=(0,0,1;0rad)
  Source = -> Panel002
  TagPosition = (-2.79248,-51.8572,0)
  TagRotation = 0
  TagSize = 10
  TagText = %tag%
FEATURE [Part::FeaturePython] PanelView145  label="View of Floor panel large 002"  # WARN: FeaturePython — macro-defined, semantics opaque (R4)
  FontFile = <userpath>/.fonts/stick/1CamBam_Stick_2.ttf
  MakeFace = false
  Placement = pos=(1700,-2600,0) rot=(0,0,1;0rad)
  Source = -> Panel029
  TagPosition = (0,0,0)
  TagRotation = 0
  TagSize = 10
  TagText = %tag%
FEATURE [Part::FeaturePython] PanelView149  label="View of Bottom panel small 003"  # WARN: FeaturePython — macro-defined, semantics opaque (R4)
  FontFile = <userpath>/.fonts/stick/1CamBam_Stick_2.ttf
  MakeFace = false
  Placement = pos=(300,-5700,0) rot=(0,0,1;0rad)
  Source = -> Panel073
  TagPosition = (0,0,0)
  TagRotation = 0
  TagSize = 10
  TagText = %tag%
FEATURE [Part::FeaturePython] PanelView150  label="View of Outer side panel large 003"  # WARN: FeaturePython — macro-defined, semantics opaque (R4)
  FontFile = <userpath>/.fonts/stick/1CamBam_Stick_2.ttf
  MakeFace = false
  Placement = pos=(6000,-2600,0) rot=(0,0,1;0rad)
  Source = -> Panel087
  TagPosition = (0,0,0)
  TagRotation = 0
  TagSize = 10
  TagText = %tag%
FEATURE [Part::FeaturePython] PanelView151  label="View of Outer side panel small 003"  # WARN: FeaturePython — macro-defined, semantics opaque (R4)
  FontFile = <userpath>/.fonts/stick/1CamBam_Stick_2.ttf
  MakeFace = false
  Placement = pos=(-5500,-5000,0) rot=(0,0,1;0rad)
  Source = -> Panel086
  TagPosition = (0,0,0)
  TagRotation = 0
  TagSize = 10
  TagText = %tag%
FEATURE [Part::FeaturePython] PanelView153  label="View of Bottom lock 003"  # WARN: FeaturePython — macro-defined, semantics opaque (R4)
  FontFile = <userpath>/.fonts/stick/1CamBam_Stick_2.ttf
  MakeFace = false
  Placement = pos=(5200,-5400,0) rot=(0,0,1;0rad)
  Source = -> Panel085
  TagPosition = (0,0,0)
  TagRotation = 0
  TagSize = 10
  TagText = %tag%
FEATURE [Part::FeaturePython] PanelView154  label="View of Bottom panel small 004"  # WARN: FeaturePython — macro-defined, semantics opaque (R4)
  FontFile = <userpath>/.fonts/stick/1CamBam_Stick_2.ttf
  MakeFace = false
  Placement = pos=(2000,-6000,0) rot=(0,0,1;0rad)
  Source = -> Panel084
  TagPosition = (0,0,0)
  TagRotation = 0
  TagSize = 10
  TagText = %tag%
FEATURE [Part::FeaturePython] PanelView155  label="View of Bottom panel medium 005"  # WARN: FeaturePython — macro-defined, semantics opaque (R4)
  FontFile = <userpath>/.fonts/stick/1CamBam_Stick_2.ttf
  MakeFace = false
  Placement = pos=(-4100,1900,0) rot=(0,0,1;0rad)
  Source = -> Panel083
  TagPosition = (0,0,0)
  TagRotation = 0
  TagSize = 10
  TagText = %tag%
FEATURE [Part::FeaturePython] PanelView156  label="View of Bottom panel medium 006"  # WARN: FeaturePython — macro-defined, semantics opaque (R4)
  FontFile = <userpath>/.fonts/stick/1CamBam_Stick_2.ttf
  MakeFace = false
  Placement = pos=(-5500,400,0) rot=(0,0,1;0rad)
  Source = -> Panel082
  TagPosition = (0,0,0)
  TagRotation = 0
  TagSize = 10
  TagText = %tag%
FEATURE [Part::FeaturePython] PanelView157  label="View of Bottom panel medium 007"  # WARN: FeaturePython — macro-defined, semantics opaque (R4)
  FontFile = <userpath>/.fonts/stick/1CamBam_Stick_2.ttf
  MakeFace = false
  Placement = pos=(-5700,1700,0) rot=(0,0,1;0rad)
  Source = -> Panel081
  TagPosition = (0,0,0)
  TagRotation = 0
  TagSize = 10
  TagText = %tag%
FEATURE [Part::FeaturePython] PanelView159  label="View of Outer roof panel large 003"  # WARN: FeaturePython — macro-defined, semantics opaque (R4)
  FontFile = <userpath>/.fonts/stick/1CamBam_Stick_2.ttf
  MakeFace = false
  Placement = pos=(3200,-2600,0) rot=(0,0,1;0rad)
  Source = -> Panel079
  TagPosition = (0,0,0)
  TagRotation = 0
  TagSize = 10
  TagText = %tag%
FEATURE [Part::FeaturePython] PanelView160  label="View of Bottom lock 004"  # WARN: FeaturePython — macro-defined, semantics opaque (R4)
  FontFile = <userpath>/.fonts/stick/1CamBam_Stick_2.ttf
  MakeFace = false
  Placement = pos=(6400,-4500,0) rot=(0,0,1;0rad)
  Source = -> Panel076
  TagPosition = (0,0,0)
  TagRotation = 0
  TagSize = 10
  TagText = %tag%
FEATURE [Part::FeaturePython] PanelView161  label="View of Bottom panel large 002"  # WARN: FeaturePython — macro-defined, semantics opaque (R4)
  FontFile = <userpath>/.fonts/stick/1CamBam_Stick_2.ttf
  MakeFace = false
  Placement = pos=(-2600,2000,0) rot=(0,0,1;0rad)
  Source = -> Panel075
  TagPosition = (0,0,0)
  TagRotation = 0
  TagSize = 10
  TagText = %tag%
FEATURE [Part::FeaturePython] PanelView162  label="View of Bottom panel medium 008"  # WARN: FeaturePython — macro-defined, semantics opaque (R4)
  FontFile = <userpath>/.fonts/stick/1CamBam_Stick_2.ttf
  MakeFace = false
  Placement = pos=(-5800,-400,0) rot=(0,0,1;0rad)
  Source = -> Panel074
  TagPosition = (0,0,0)
  TagRotation = 0
  TagSize = 10
  TagText = %tag%
FEATURE [Part::FeaturePython] PanelView163  label="View of Outer roof panel large 004"  # WARN: FeaturePython — macro-defined, semantics opaque (R4)
  FontFile = <userpath>/.fonts/stick/1CamBam_Stick_2.ttf
  MakeFace = false
  Placement = pos=(4500,-2600,0) rot=(0,0,1;0rad)
  Source = -> Panel089
  TagPosition = (0,0,0)
  TagRotation = 0
  TagSize = 10
  TagText = %tag%
FEATURE [Part::FeaturePython] PanelView164  label="View of Spacer 012"  # WARN: FeaturePython — macro-defined, semantics opaque (R4)
  FontFile = <userpath>/.fonts/stick/1CamBam_Stick_2.ttf
  MakeFace = false
  Placement = pos=(1600,-4500,0) rot=(0,0,1;0rad)
  Source = -> Panel034
  TagPosition = (0,0,0)
  TagRotation = 0
  TagSize = 10
  TagText = %tag%
FEATURE [Part::FeaturePython] PanelView165  label="View of Spacer 013"  # WARN: FeaturePython — macro-defined, semantics opaque (R4)
  FontFile = <userpath>/.fonts/stick/1CamBam_Stick_2.ttf
  MakeFace = false
  Placement = pos=(4700,-4600,0) rot=(0,0,1;0rad)
  Source = -> Panel041
  TagPosition = (0,0,0)
  TagRotation = 0
  TagSize = 10
  TagText = %tag%
FEATURE [Part::FeaturePython] PanelView166  label="View of Spacer 014"  # WARN: FeaturePython — macro-defined, semantics opaque (R4)
  FontFile = <userpath>/.fonts/stick/1CamBam_Stick_2.ttf
  MakeFace = false
  Placement = pos=(-2000,-4700,0) rot=(0,0,1;0rad)
  Source = -> Panel044
  TagPosition = (0,0,0)
  TagRotation = 0
  TagSize = 10
  TagText = %tag%
FEATURE [Part::FeaturePython] PanelView167  label="View of Lock 005"  # WARN: FeaturePython — macro-defined, semantics opaque (R4)
  FontFile = <userpath>/.fonts/stick/1CamBam_Stick_2.ttf
  MakeFace = false
  Placement = pos=(600,200,0) rot=(0,0,1;0rad)
  Source = -> Panel045
  TagPosition = (12.2148,36.3764,0)
  TagRotation = 0
  TagSize = 10
  TagText = %tag%
FEATURE [Part::FeaturePython] PanelView168  label="View of Spacer 015"  # WARN: FeaturePython — macro-defined, semantics opaque (R4)
  FontFile = <userpath>/.fonts/stick/1CamBam_Stick_2.ttf
  MakeFace = false
  Placement = pos=(3500,-5300,0) rot=(0,0,1;0rad)
  Source = -> Panel035
  TagPosition = (0,0,0)
  TagRotation = 0
  TagSize = 10
  TagText = %tag%
FEATURE [Part::FeaturePython] PanelView169  label="View of Lock 006"  # WARN: FeaturePython — macro-defined, semantics opaque (R4)
  FontFile = <userpath>/.fonts/stick/1CamBam_Stick_2.ttf
  MakeFace = false
  Placement = pos=(400,0,0) rot=(0,0,1;0rad)
  Source = -> Panel046
  TagPosition = (-19.1258,35.866,0)
  TagRotation = 0
  TagSize = 10
  TagText = %tag%
FEATURE [Part::FeaturePython] PanelView170  label="View of Spacer 016"  # WARN: FeaturePython — macro-defined, semantics opaque (R4)
  FontFile = <userpath>/.fonts/stick/1CamBam_Stick_2.ttf
  MakeFace = false
  Placement = pos=(6700,-5200,0) rot=(0,0,1;0rad)
  Source = -> Panel038
  TagPosition = (0,0,0)
  TagRotation = 0
  TagSize = 10
  TagText = %tag%
FEATURE [Part::FeaturePython] PanelView171  label="View of Spacer 017"  # WARN: FeaturePython — macro-defined, semantics opaque (R4)
  FontFile = <userpath>/.fonts/stick/1CamBam_Stick_2.ttf
  MakeFace = false
  Placement = pos=(1800,-5300,0) rot=(0,0,1;0rad)
  Source = -> Panel036
  TagPosition = (0,0,0)
  TagRotation = 0
  TagSize = 10
  TagText = %tag%
FEATURE [Part::FeaturePython] PanelView172  label="View of Spacer 018"  # WARN: FeaturePython — macro-defined, semantics opaque (R4)
  FontFile = <userpath>/.fonts/stick/1CamBam_Stick_2.ttf
  MakeFace = false
  Placement = pos=(-200,-4600,0) rot=(0,0,1;0rad)
  Source = -> Panel037
  TagPosition = (0,0,0)
  TagRotation = 0
  TagSize = 10
  TagText = %tag%
FEATURE [Part::FeaturePython] PanelView173  label="View of Spacer 019"  # WARN: FeaturePython — macro-defined, semantics opaque (R4)
  FontFile = <userpath>/.fonts/stick/1CamBam_Stick_2.ttf
  MakeFace = false
  Placement = pos=(3100,-4700,0) rot=(0,0,1;0rad)
  Source = -> Panel039
  TagPosition = (0,0,0)
  TagRotation = 0
  TagSize = 10
  TagText = %tag%
FEATURE [Part::FeaturePython] PanelView174  label="View of Spacer 020"  # WARN: FeaturePython — macro-defined, semantics opaque (R4)
  FontFile = <userpath>/.fonts/stick/1CamBam_Stick_2.ttf
  MakeFace = false
  Placement = pos=(300,-5200,0) rot=(0,0,1;0rad)
  Source = -> Panel040
  TagPosition = (0,0,0)
  TagRotation = 0
  TagSize = 10
  TagText = %tag%
FEATURE [Part::FeaturePython] PanelView175  label="View of Spacer 021"  # WARN: FeaturePython — macro-defined, semantics opaque (R4)
  FontFile = <userpath>/.fonts/stick/1CamBam_Stick_2.ttf
  MakeFace = false
  Placement = pos=(-1300,-5500,0) rot=(0,0,1;0rad)
  Source = -> Panel042
  TagPosition = (0,0,0)
  TagRotation = 0
  TagSize = 10
  TagText = %tag%
FEATURE [Part::FeaturePython] PanelView176  label="View of Spacer 022"  # WARN: FeaturePython — macro-defined, semantics opaque (R4)
  FontFile = <userpath>/.fonts/stick/1CamBam_Stick_2.ttf
  MakeFace = false
  Placement = pos=(-2700,-5800,0) rot=(0,0,1;0rad)
  Source = -> Panel043
  TagPosition = (0,0,0)
  TagRotation = 0
  TagSize = 10
  TagText = %tag%
FEATURE [Part::FeaturePython] PanelView177  label="View of Lock 007"  # WARN: FeaturePython — macro-defined, semantics opaque (R4)
  FontFile = <userpath>/.fonts/stick/1CamBam_Stick_2.ttf
  MakeFace = false
  Placement = pos=(100,-300,0) rot=(0,0,1;0rad)
  Source = -> Panel047
  TagPosition = (-4.78742,38.0147,0)
  TagRotation = 0
  TagSize = 10
  TagText = %tag%
FEATURE [Part::FeaturePython] PanelView178  label="View of Lock 008"  # WARN: FeaturePython — macro-defined, semantics opaque (R4)
  FontFile = <userpath>/.fonts/stick/1CamBam_Stick_2.ttf
  MakeFace = false
  Placement = pos=(-180.983,-529.946,0) rot=(0,0,1;0rad)
  Source = -> Panel048
  TagPosition = (4.34313,37.5561,0)
  TagRotation = 0
  TagSize = 10
  TagText = %tag%
FEATURE [Part::FeaturePython] PanelView179  label="View of Struct spacer 021"  # WARN: FeaturePython — macro-defined, semantics opaque (R4)
  FontFile = <userpath>/.fonts/stick/1CamBam_Stick_2.ttf
  MakeFace = false
  Placement = pos=(-300,0,0) rot=(0,0,1;0rad)
  Source = -> Panel091
  TagPosition = (0,0,0)
  TagRotation = 0
  TagSize = 10
  TagText = %tag%
FEATURE [Part::FeaturePython] PanelView180  label="View of Struct spacer 022"  # WARN: FeaturePython — macro-defined, semantics opaque (R4)
  FontFile = <userpath>/.fonts/stick/1CamBam_Stick_2.ttf
  MakeFace = false
  Placement = pos=(-300,400,0) rot=(0,0,1;0rad)
  Source = -> Panel093
  TagPosition = (0,0,0)
  TagRotation = 0
  TagSize = 10
  TagText = %tag%
FEATURE [Part::FeaturePython] PanelView182  label="View of Struct outer roof small 005"  # WARN: FeaturePython — macro-defined, semantics opaque (R4)
  FontFile = <userpath>/.fonts/stick/1CamBam_Stick_2.ttf
  MakeFace = false
  Placement = pos=(800,600,0) rot=(0,0,1;0rad)
  Source = -> Panel140
  TagPosition = (0,0,0)
  TagRotation = 90
  TagSize = 10
  TagText = %tag%
FEATURE [Part::FeaturePython] PanelView183  label="View of Struct outer roof small 006"  # WARN: FeaturePython — macro-defined, semantics opaque (R4)
  FontFile = <userpath>/.fonts/stick/1CamBam_Stick_2.ttf
  MakeFace = false
  Placement = pos=(800,-400,0) rot=(0,0,1;0rad)
  Source = -> Panel141
  TagPosition = (0,0,0)
  TagRotation = 90
  TagSize = 10
  TagText = %tag%
FEATURE [Part::FeaturePython] PanelView187  label="View of Struct spacer 023"  # WARN: FeaturePython — macro-defined, semantics opaque (R4)
  FontFile = <userpath>/.fonts/stick/1CamBam_Stick_2.ttf
  MakeFace = false
  Placement = pos=(0,800,0) rot=(0,0,1;0rad)
  Source = -> Panel102
  TagPosition = (0,0,0)
  TagRotation = 0
  TagSize = 10
  TagText = %tag%
FEATURE [Part::FeaturePython] PanelView188  label="View of Struct spacer 024"  # WARN: FeaturePython — macro-defined, semantics opaque (R4)
  FontFile = <userpath>/.fonts/stick/1CamBam_Stick_2.ttf
  MakeFace = false
  Placement = pos=(-300,1200,0) rot=(0,0,1;0rad)
  Source = -> Panel106
  TagPosition = (0,0,0)
  TagRotation = 0
  TagSize = 10
  TagText = %tag%
FEATURE [Part::FeaturePython] PanelView189  label="View of Struct inner side small 005"  # WARN: FeaturePython — macro-defined, semantics opaque (R4)
  FontFile = <userpath>/.fonts/stick/1CamBam_Stick_2.ttf
  MakeFace = false
  Placement = pos=(300,900,0) rot=(0,0,1;0rad)
  Source = -> Panel125
  TagPosition = (0,0,0)
  TagRotation = 90
  TagSize = 10
  TagText = %tag%
FEATURE [Part::FeaturePython] PanelView190  label="View of Struct spacer 025"  # WARN: FeaturePython — macro-defined, semantics opaque (R4)
  FontFile = <userpath>/.fonts/stick/1CamBam_Stick_2.ttf
  MakeFace = false
  Placement = pos=(-300,2000,0) rot=(0,0,1;0rad)
  Source = -> Panel103
  TagPosition = (0,0,0)
  TagRotation = 0
  TagSize = 10
  TagText = %tag%
FEATURE [Part::FeaturePython] PanelView192  label="View of Struct spacer 026"  # WARN: FeaturePython — macro-defined, semantics opaque (R4)
  FontFile = <userpath>/.fonts/stick/1CamBam_Stick_2.ttf
  MakeFace = false
  Placement = pos=(-300,800,0) rot=(0,0,1;0rad)
  Source = -> Panel090
  TagPosition = (0,0,0)
  TagRotation = 0
  TagSize = 10
  TagText = %tag%
FEATURE [Part::FeaturePython] PanelView193  label="View of Struct outer side small 005"  # WARN: FeaturePython — macro-defined, semantics opaque (R4)
  FontFile = <userpath>/.fonts/stick/1CamBam_Stick_2.ttf
  MakeFace = false
  Placement = pos=(600,700,0) rot=(0,0,1;0rad)
  Source = -> Panel129
  TagPosition = (0,0,0)
  TagRotation = 90
  TagSize = 10
  TagText = %tag%
FEATURE [Part::FeaturePython] PanelView198  label="View of Struct spacer 027"  # WARN: FeaturePython — macro-defined, semantics opaque (R4)
  FontFile = <userpath>/.fonts/stick/1CamBam_Stick_2.ttf
  MakeFace = false
  Placement = pos=(0,400,0) rot=(0,0,1;0rad)
  Source = -> Panel107
  TagPosition = (0,0,0)
  TagRotation = 0
  TagSize = 10
  TagText = %tag%
FEATURE [Part::FeaturePython] PanelView200  label="View of Struct inner side small 006"  # WARN: FeaturePython — macro-defined, semantics opaque (R4)
  FontFile = <userpath>/.fonts/stick/1CamBam_Stick_2.ttf
  MakeFace = false
  Placement = pos=(200,-800,0) rot=(0,0,1;0rad)
  Source = -> Panel123
  TagPosition = (0,0,0)
  TagRotation = 90
  TagSize = 10
  TagText = %tag%
FEATURE [Part::FeaturePython] PanelView201  label="View of Struct spacer 028"  # WARN: FeaturePython — macro-defined, semantics opaque (R4)
  FontFile = <userpath>/.fonts/stick/1CamBam_Stick_2.ttf
  MakeFace = false
  Placement = pos=(0,1200,0) rot=(0,0,1;0rad)
  Source = -> Panel098
  TagPosition = (0,0,0)
  TagRotation = 0
  TagSize = 10
  TagText = %tag%
FEATURE [Part::FeaturePython] PanelView202  label="View of Struct spacer 029"  # WARN: FeaturePython — macro-defined, semantics opaque (R4)
  FontFile = <userpath>/.fonts/stick/1CamBam_Stick_2.ttf
  MakeFace = false
  Source = -> Panel092
  TagPosition = (0,0,0)
  TagRotation = 0
  TagSize = 10
  TagText = %tag%
FEATURE [Part::FeaturePython] PanelView204  label="View of Struct spacer 030"  # WARN: FeaturePython — macro-defined, semantics opaque (R4)
  FontFile = <userpath>/.fonts/stick/1CamBam_Stick_2.ttf
  MakeFace = false
  Placement = pos=(-300,1600,0) rot=(0,0,1;0rad)
  Source = -> Panel099
  TagPosition = (0,0,0)
  TagRotation = 0
  TagSize = 10
  TagText = %tag%
FEATURE [Part::FeaturePython] PanelView206  label="View of Struct outer side small 006"  # WARN: FeaturePython — macro-defined, semantics opaque (R4)
  FontFile = <userpath>/.fonts/stick/1CamBam_Stick_2.ttf
  MakeFace = false
  Placement = pos=(500,-500,0) rot=(0,0,1;0rad)
  Source = -> Panel131
  TagPosition = (0,0,0)
  TagRotation = 90
  TagSize = 10
  TagText = %tag%
FEATURE [Part::Feature] Wire145  label="Base hole"
  shape: bbox 2e-07 x 72 x 24 mm, 0 faces, 0 solids (baked)
FEATURE [Part::Feature] Wire149
  shape: bbox 2e-07 x 30 x 135 mm, 0 faces, 0 solids (baked)
FEATURE [Part::FeaturePython] Clone  label="Wire154"  # Draft clone (typed FeaturePython)
  AttacherType = Attacher::AttachEngine3D
  Objects = -> [Wire145]
  Placement = pos=(0,299.999,-3.05176e-05) rot=(0,0,1;0rad)
  Scale = (1,1,1)
FEATURE [Part::FeaturePython] Clone001  label="Wire155"  # Draft clone (typed FeaturePython)
  AttacherType = Attacher::AttachEngine3D
  Objects = -> [Clone]
  Placement = pos=(0,-3000,285.999) rot=(1,0,0;3.14159rad)
  Scale = (1,1,1)
FEATURE [Part::FeaturePython] Clone002  label="Wire160"  # Draft clone (typed FeaturePython)
  AttacherType = Attacher::AttachEngine3D
  Objects = -> [Clone001]
  Placement = pos=(0,-3299.99,285.999) rot=(1,0,0;3.14159rad)
  Scale = (1,1,1)
FEATURE [Part::FeaturePython] Clone003  label="Wire157"  # Draft clone (typed FeaturePython)
  AttacherType = Attacher::AttachEngine3D
  Objects = -> [Wire145]
  Placement = pos=(0,-2093,-1207) rot=(-1,0,0;1.5708rad)
  Scale = (1,1,1)
FEATURE [Part::FeaturePython] Clone004  label="Wire158"  # Draft clone (typed FeaturePython)
  AttacherType = Attacher::AttachEngine3D
  Objects = -> [Clone002]
  Placement = pos=(0,-1807,2093) rot=(1,0,0;1.5708rad)
  Scale = (1,1,1)
FEATURE [Part::FeaturePython] Clone005  label="Wire161"  # Draft clone (typed FeaturePython)
  AttacherType = Attacher::AttachEngine3D
  Objects = -> [Clone003]
  Placement = pos=(0,-2093,-906.999) rot=(-1,0,0;1.5708rad)
  Scale = (1,1,1)
FEATURE [Part::FeaturePython] Clone006  label="Wire162"  # Draft clone (typed FeaturePython)
  AttacherType = Attacher::AttachEngine3D
  Objects = -> [Clone004]
  Placement = pos=(0,-1807,2393) rot=(1,0,0;1.5708rad)
  Scale = (1,1,1)
FEATURE [Part::FeaturePython] Clone007  label="Wire163"  # Draft clone (typed FeaturePython)
  AttacherType = Attacher::AttachEngine3D
  Objects = -> [Clone006]
  Placement = pos=(0,-1807,2693) rot=(1,0,0;1.5708rad)
  Scale = (1,1,1)
FEATURE [Part::FeaturePython] Clone008  label="Wire164"  # Draft clone (typed FeaturePython)
  AttacherType = Attacher::AttachEngine3D
  Objects = -> [Clone005]
  Placement = pos=(0,-2093,-607) rot=(-1,0,0;1.5708rad)
  Scale = (1,1,1)
FEATURE [Part::FeaturePython] Clone009  label="Wire165"  # Draft clone (typed FeaturePython)
  AttacherType = Attacher::AttachEngine3D
  Objects = -> [Clone008]
  Placement = pos=(0,-2093,-7.00085) rot=(-1,0,0;1.5708rad)
  Scale = (1,1,1)
FEATURE [Part::FeaturePython] Clone010  label="Wire166"  # Draft clone (typed FeaturePython)
  AttacherType = Attacher::AttachEngine3D
  Objects = -> [Clone007]
  Placement = pos=(0,-1807,3292.99) rot=(1,0,0;1.5708rad)
  Scale = (1,1,1)
FEATURE [Part::FeaturePython] Clone011  label="Wire167"  # Draft clone (typed FeaturePython)
  AttacherType = Attacher::AttachEngine3D
  Objects = -> [Clone006]
  Placement = pos=(0,-1807,2992.99) rot=(1,0,0;1.5708rad)
  Scale = (1,1,1)
FEATURE [Part::FeaturePython] Clone012  label="Wire168"  # Draft clone (typed FeaturePython)
  AttacherType = Attacher::AttachEngine3D
  Objects = -> [Clone005]
  Placement = pos=(0,-2093,-307) rot=(-1,0,0;1.5708rad)
  Scale = (1,1,1)
FEATURE [Part::FeaturePython] Clone013  label="Wire169"  # Draft clone (typed FeaturePython)
  AttacherType = Attacher::AttachEngine3D
  Objects = -> [Clone004]
  Placement = pos=(0,-1807,1793) rot=(1,0,0;1.5708rad)
  Scale = (1,1,1)
FEATURE [Part::Part2DObjectPython] DWire012  # Draft 2D object (typed FeaturePython)
  ChamferSize = 0
  Closed = true
  End = (0,-1938,1028.02)
  FilletRadius = 0
  Length = 163.924
  MakeFace = false
  Points = (16) [(0,-1930,1028.02),(0,-1930,1034),(0,-1930,1052),(0,-1930,1058),(0,-1938,1058),(0,-1938,1052),(0,-1962,1052),(0,-1962,1058),(0,-1970,1058),+7 more]
  Start = (0,-1930,1028.02)
  Subdivisions = 0
FEATURE [Part::Part2DObjectPython] Clone2D  label="DWire012 (2D)"  # Draft 2D object (typed FeaturePython)
  Objects = -> [DWire012]
  Placement = pos=(0,-0.000244141,599.999) rot=(0,0,1;0rad)
  Scale = (1,1,1)
FEATURE [Part::Feature] Wire150  label="Wire170"
  Placement = pos=(0,599.999,-3.05174e-05) rot=(0,0,1;0rad)
  shape: bbox 2e-07 x 72 x 24 mm, 0 faces, 0 solids (baked)
FEATURE [Part::FeaturePython] Clone014  label="Wire171"  # Draft clone (typed FeaturePython)
  AttacherType = Attacher::AttachEngine3D
  Objects = -> [Wire150]
  Placement = pos=(0,-2700,285.999) rot=(1,0,0;3.14159rad)
  Scale = (1,1,1)
FEATURE [Part::FeaturePython] Clone015  label="Wire172"  # Draft clone (typed FeaturePython)
  AttacherType = Attacher::AttachEngine3D
  Objects = -> [Clone014]
  Placement = pos=(0,-2400,285.999) rot=(1,0,0;3.14159rad)
  Scale = (1,1,1)
FEATURE [Part::FeaturePython] Clone016  label="Wire173"  # Draft clone (typed FeaturePython)
  AttacherType = Attacher::AttachEngine3D
  Objects = -> [Wire150]
  Placement = pos=(0,899.998,-4.38688e-05) rot=(0,0,1;0rad)
  Scale = (1,1,1)
FEATURE [Part::FeaturePython] Clone017  label="Wire174"  # Draft clone (typed FeaturePython)
  AttacherType = Attacher::AttachEngine3D
  Objects = -> [Wire150]
  Placement = pos=(0,1200,-4.38688e-05) rot=(0,0,1;0rad)
  Scale = (1,1,1)
FEATURE [Part::FeaturePython] Clone018  label="Wire175"  # Draft clone (typed FeaturePython)
  AttacherType = Attacher::AttachEngine3D
  Objects = -> [Clone014]
  Placement = pos=(0,-2100,285.999) rot=(1,0,0;3.14159rad)
  Scale = (1,1,1)
FEATURE [Part::FeaturePython] Clone019  label="Wire176"  # Draft clone (typed FeaturePython)
  AttacherType = Attacher::AttachEngine3D
  Objects = -> [Clone016]
  Placement = pos=(0,1500,-5.72203e-05) rot=(0,0,1;0rad)
  Scale = (1,1,1)
FEATURE [Part::FeaturePython] Clone020  label="Wire177"  # Draft clone (typed FeaturePython)
  AttacherType = Attacher::AttachEngine3D
  Objects = -> [Clone015]
  Placement = pos=(0,-1800,285.999) rot=(1,0,0;3.14159rad)
  Scale = (1,1,1)
FEATURE [Part::FeaturePython] Clone021  label="Wire178"  # Draft clone (typed FeaturePython)
  AttacherType = Attacher::AttachEngine3D
  Objects = -> [Wire150]
  Placement = pos=(0,1800,-4.38688e-05) rot=(0,0,1;0rad)
  Scale = (1,1,1)
FEATURE [Part::FeaturePython] Clone022  label="Wire179"  # Draft clone (typed FeaturePython)
  AttacherType = Attacher::AttachEngine3D
  Objects = -> [Clone014]
  Placement = pos=(0,-1500,285.999) rot=(1,0,0;3.14159rad)
  Scale = (1,1,1)
FEATURE [Part::FeaturePython] Clone023  label="Wire180"  # Draft clone (typed FeaturePython)
  AttacherType = Attacher::AttachEngine3D
  Objects = -> [Clone016]
  Placement = pos=(0,2100,-5.72203e-05) rot=(0,0,1;0rad)
  Scale = (1,1,1)
FEATURE [Part::FeaturePython] Clone024  label="Wire181"  # Draft clone (typed FeaturePython)
  AttacherType = Attacher::AttachEngine3D
  Objects = -> [Clone020]
  Placement = pos=(0,-600.001,285.999) rot=(1,0,0;3.14159rad)
  Scale = (1,1,1)
FEATURE [Part::FeaturePython] Clone025  label="Wire182"  # Draft clone (typed FeaturePython)
  AttacherType = Attacher::AttachEngine3D
  Objects = -> [Clone015]
  Placement = pos=(0,-1200,285.999) rot=(1,0,0;3.14159rad)
  Scale = (1,1,1)
FEATURE [Part::FeaturePython] Clone026  label="Wire183"  # Draft clone (typed FeaturePython)
  AttacherType = Attacher::AttachEngine3D
  Objects = -> [Clone019]
  Placement = pos=(0,2699.99,-7.05717e-05) rot=(0,0,1;0rad)
  Scale = (1,1,1)
FEATURE [Part::FeaturePython] Clone027  label="Wire184"  # Draft clone (typed FeaturePython)
  AttacherType = Attacher::AttachEngine3D
  Objects = -> [Clone017]
  Placement = pos=(0,2399.99,-5.72203e-05) rot=(0,0,1;0rad)
  Scale = (1,1,1)
FEATURE [Part::FeaturePython] Clone028  label="Wire185"  # Draft clone (typed FeaturePython)
  AttacherType = Attacher::AttachEngine3D
  Objects = -> [Clone018]
  Placement = pos=(0,-900,285.999) rot=(1,0,0;3.14159rad)
  Scale = (1,1,1)
FEATURE [Part::Part2DObjectPython] Clone2D001  label="DWire012 (2D)001"  # Draft 2D object (typed FeaturePython)
  Objects = -> [DWire012]
  Placement = pos=(0,292.998,2093) rot=(1,0,0;1.5708rad)
  Scale = (1,1,1)
FEATURE [Part::Part2DObjectPython] Clone2D002  label="DWire012 (2D)001 (2D)"  # Draft 2D object (typed FeaturePython)
  Objects = -> [Clone2D001]
  Placement = pos=(0,1793,2093) rot=(1,0,0;1.5708rad)
  Scale = (1,1,1)
FEATURE [Part::Compound] Compound019
  Links = -> [Shape034095,Shape034103,Shape034102,Shape034104,Shape034087,Wire150,Clone025,Clone014,Clone016,Clone020,Clone015,Clone019,Clone017,Clone018,Clone024,Clone022,Clone021,Clone023,Clone026,Clone027,Clone028,Clone2D002,Clone2D001]
FEATURE [Part::FeaturePython] Panel052  label="Side base 001"  # WARN: FeaturePython — macro-defined, semantics opaque (R4)
  Area = 604490
  Base = -> Compound019
  Description = Side piece of main structure - base
  FaceMaker = 0
  HorizontalArea = 0
  Length = 0
  MoveWithHost = false
  Normal = (1,0,0)
  PerimeterLength = 0
  Placement = pos=(656.998,0,0) rot=(0,0,1;0rad)
  Role = 0
  Sheets = 1
  Tag = FRA-A/F1
  Thickness = 18
  VerticalArea = 0
  WaveDirection = 0
  WaveHeight = 0
  WaveLength = 0
  WaveType = 0
  Width = 0
FEATURE [Part::FeaturePython] Panel057  label="Side base 002"  # WARN: FeaturePython — macro-defined, semantics opaque (R4)
  Area = 604490
  CloneOf = -> Panel052
  Description = Side piece of main structure - base
  FaceMaker = 0
  HorizontalArea = 0
  Length = 0
  MoveWithHost = false
  Normal = (0,0,0)
  PerimeterLength = 0
  Placement = pos=(524.997,0,0) rot=(0,0,1;0rad)
  Role = 0
  Sheets = 1
  Tag = FRA-A/F1
  Thickness = 18
  VerticalArea = 0
  WaveDirection = 0
  WaveHeight = 0
  WaveLength = 0
  WaveType = 0
  Width = 0
FEATURE [Part::FeaturePython] Panel063  label="Side base 003"  # WARN: FeaturePython — macro-defined, semantics opaque (R4)
  Area = 604490
  CloneOf = -> Panel052
  Description = Side piece of main structure - base
  FaceMaker = 0
  HorizontalArea = 0
  Length = 0
  MoveWithHost = false
  Normal = (0,0,0)
  PerimeterLength = 0
  Placement = pos=(-543.002,0,0) rot=(0,0,1;0rad)
  Role = 0
  Sheets = 1
  Tag = FRA-A/F1
  Thickness = 18
  VerticalArea = 0
  WaveDirection = 0
  WaveHeight = 0
  WaveLength = 0
  WaveType = 0
  Width = 0
FEATURE [Part::FeaturePython] Panel071  label="Side base 004"  # WARN: FeaturePython — macro-defined, semantics opaque (R4)
  Area = 604490
  CloneOf = -> Panel052
  Description = Side piece of main structure - base
  FaceMaker = 0
  HorizontalArea = 0
  Length = 0
  MoveWithHost = false
  Normal = (0,0,0)
  PerimeterLength = 0
  Placement = pos=(-675.002,0,0) rot=(0,0,1;0rad)
  Role = 0
  Sheets = 1
  Tag = FRA-A/F1
  Thickness = 18
  VerticalArea = 0
  WaveDirection = 0
  WaveHeight = 0
  WaveLength = 0
  WaveType = 0
  Width = 0
FEATURE [Part::FeaturePython] PanelView004  label="View of Side base 001"  # WARN: FeaturePython — macro-defined, semantics opaque (R4)
  FontFile = <userpath>/.fonts/stick/1CamBam_Stick_2.ttf
  MakeFace = true
  Placement = pos=(1300,600,0) rot=(0,0,1;0rad)
  Source = -> Panel052
  TagPosition = (0,0,0)
  TagRotation = 0
  TagSize = 10
  TagText = %tag%
FEATURE [Part::FeaturePython] PanelView009  label="View of Side base 002"  # WARN: FeaturePython — macro-defined, semantics opaque (R4)
  FontFile = <userpath>/.fonts/stick/1CamBam_Stick_2.ttf
  MakeFace = true
  Placement = pos=(1800,600,0) rot=(0,0,1;0rad)
  Source = -> Panel057
  TagPosition = (0,0,0)
  TagRotation = 0
  TagSize = 10
  TagText = %tag%
FEATURE [Part::FeaturePython] PanelView052  label="View of Side base 003"  # WARN: FeaturePython — macro-defined, semantics opaque (R4)
  FontFile = <userpath>/.fonts/stick/1CamBam_Stick_2.ttf
  MakeFace = false
  Placement = pos=(7800,99.9593,2.85428) rot=(0,0,1;0rad)
  Source = -> Panel063
  TagPosition = (0,0,0)
  TagRotation = 0
  TagSize = 10
  TagText = %tag%
FEATURE [Part::FeaturePython] PanelView060  label="View of Side base 004"  # WARN: FeaturePython — macro-defined, semantics opaque (R4)
  FontFile = <userpath>/.fonts/stick/1CamBam_Stick_2.ttf
  MakeFace = false
  Placement = pos=(8200,99.9593,2.85428) rot=(0,0,1;0rad)
  Source = -> Panel071
  TagPosition = (0,0,0)
  TagRotation = 0
  TagSize = 10
  TagText = %tag%
FEATURE [Part::FeaturePython] PanelView219  label="View of Side base 005"  # WARN: FeaturePython — macro-defined, semantics opaque (R4)
  FontFile = <userpath>/.fonts/stick/1CamBam_Stick_2.ttf
  MakeFace = false
  Placement = pos=(-1100,0,0) rot=(0,0,1;0rad)
  Source = -> Panel071
  TagPosition = (0,0,0)
  TagRotation = 0
  TagSize = 10
  TagText = %tag%
FEATURE [Part::FeaturePython] PanelView227  label="View of Side base 006"  # WARN: FeaturePython — macro-defined, semantics opaque (R4)
  FontFile = <userpath>/.fonts/stick/1CamBam_Stick_2.ttf
  MakeFace = false
  Placement = pos=(-700,0,0) rot=(0,0,1;0rad)
  Source = -> Panel063
  TagPosition = (0,0,0)
  TagRotation = 0
  TagSize = 10
  TagText = %tag%
FEATURE [Part::FeaturePython] Clone029  label="Wire186"  # Draft clone (typed FeaturePython)
  AttacherType = Attacher::AttachEngine3D
  Objects = -> [Wire145]
  Placement = pos=(0,2999.99,-3.05174e-05) rot=(0,0,1;0rad)
  Scale = (1,1,1)
FEATURE [Part::FeaturePython] Clone030  label="Wire187"  # Draft clone (typed FeaturePython)
  AttacherType = Attacher::AttachEngine3D
  Objects = -> [Clone029]
  Placement = pos=(0,-300.001,285.999) rot=(1,0,0;3.14159rad)
  Scale = (1,1,1)
FEATURE [Part::FeaturePython] Clone031  label="Wire188"  # Draft clone (typed FeaturePython)
  AttacherType = Attacher::AttachEngine3D
  Objects = -> [Clone030]
  Placement = pos=(0,-0.00152588,285.999) rot=(1,0,0;3.14159rad)
  Scale = (1,1,1)
FEATURE [Part::FeaturePython] Clone032  label="Wire189"  # Draft clone (typed FeaturePython)
  AttacherType = Attacher::AttachEngine3D
  Objects = -> [Clone029]
  Placement = pos=(0,3299.99,-3.05174e-05) rot=(0,0,1;0rad)
  Scale = (1,1,1)
FEATURE [Part::FeaturePython] Clone033  label="Wire190"  # Draft clone (typed FeaturePython)
  AttacherType = Attacher::AttachEngine3D
  Objects = -> [Clone031]
  Placement = pos=(0,2093,2093) rot=(1,0,0;1.5708rad)
  Scale = (1,1,1)
FEATURE [Part::FeaturePython] Clone034  label="Wire191"  # Draft clone (typed FeaturePython)
  AttacherType = Attacher::AttachEngine3D
  Objects = -> [Clone032]
  Placement = pos=(0,1807,-1207) rot=(-1,0,0;1.5708rad)
  Scale = (1,1,1)
FEATURE [Part::FeaturePython] Clone035  label="Wire192"  # Draft clone (typed FeaturePython)
  AttacherType = Attacher::AttachEngine3D
  Objects = -> [Clone034]
  Placement = pos=(0,1807,-1507) rot=(-1,0,0;1.5708rad)
  Scale = (1,1,1)
FEATURE [Part::FeaturePython] Clone036  label="Wire193"  # Draft clone (typed FeaturePython)
  AttacherType = Attacher::AttachEngine3D
  Objects = -> [Clone034]
  Placement = pos=(0,1807,-906.999) rot=(-1,0,0;1.5708rad)
  Scale = (1,1,1)
FEATURE [Part::FeaturePython] Clone037  label="Wire194"  # Draft clone (typed FeaturePython)
  AttacherType = Attacher::AttachEngine3D
  Objects = -> [Clone033]
  Placement = pos=(0,2092.99,2393) rot=(1,0,0;1.5708rad)
  Scale = (1,1,1)
FEATURE [Part::FeaturePython] Clone038  label="Wire195"  # Draft clone (typed FeaturePython)
  AttacherType = Attacher::AttachEngine3D
  Objects = -> [Clone036]
  Placement = pos=(0,1807,-607) rot=(-1,0,0;1.5708rad)
  Scale = (1,1,1)
FEATURE [Part::FeaturePython] Clone039  label="Wire196"  # Draft clone (typed FeaturePython)
  AttacherType = Attacher::AttachEngine3D
  Objects = -> [Clone037]
  Placement = pos=(0,2092.99,2693) rot=(1,0,0;1.5708rad)
  Scale = (1,1,1)
FEATURE [Part::FeaturePython] Clone040  label="Wire197"  # Draft clone (typed FeaturePython)
  AttacherType = Attacher::AttachEngine3D
  Objects = -> [Clone036]
  Placement = pos=(0,1807,-307) rot=(-1,0,0;1.5708rad)
  Scale = (1,1,1)
FEATURE [Part::FeaturePython] Clone041  label="Wire198"  # Draft clone (typed FeaturePython)
  AttacherType = Attacher::AttachEngine3D
  Objects = -> [Clone038]
  Placement = pos=(0,1807,-7.00079) rot=(-1,0,0;1.5708rad)
  Scale = (1,1,1)
FEATURE [Part::FeaturePython] Clone042  label="Wire199"  # Draft clone (typed FeaturePython)
  AttacherType = Attacher::AttachEngine3D
  Objects = -> [Clone037]
  Placement = pos=(0,2092.99,2992.99) rot=(1,0,0;1.5708rad)
  Scale = (1,1,1)
FEATURE [Part::FeaturePython] Clone043  label="Wire200"  # Draft clone (typed FeaturePython)
  AttacherType = Attacher::AttachEngine3D
  Objects = -> [Clone039]
  Placement = pos=(0,2092.99,3292.99) rot=(1,0,0;1.5708rad)
  Scale = (1,1,1)
FEATURE [Part::FeaturePython] Clone044  label="Wire201"  # Draft clone (typed FeaturePython)
  AttacherType = Attacher::AttachEngine3D
  Objects = -> [Wire149]
  Placement = pos=(0,3899.99,4.38e-10) rot=(0,0,1;0rad)
  Scale = (1,1,1)
FEATURE [Part::Part2DObjectPython] Clone2D003  label="DWire012 (2D)002"  # Draft 2D object (typed FeaturePython)
  Objects = -> [DWire012]
  Placement = pos=(0,3899.99,4.688e-09) rot=(0,0,1;0rad)
  Scale = (1,1,1)
FEATURE [Part::Part2DObjectPython] Clone2D004  label="DWire012 (2D)002 (2D)"  # Draft 2D object (typed FeaturePython)
  Objects = -> [Clone2D003]
  Placement = pos=(0,3899.99,599.999) rot=(0,0,1;0rad)
  Scale = (1,1,1)
FEATURE [Part::Feature] Wire151  label="Wire202"
  shape: bbox 2e-07 x 935.7 x 1835 mm, 0 faces, 0 solids (baked)
FEATURE [Part::Compound] Compound021
  Links = -> [Shape034107,Shape034120,Wire145,Clone003,Clone,Clone013,Clone002,Clone001,Clone004,Wire149,Clone006,Clone005,Clone011,Clone008,Clone007,Clone009,Clone010,Clone012,DWire012,Clone2D,Wire151]
FEATURE [Part::FeaturePython] Panel053  label="Side right corner 001"  # WARN: FeaturePython — macro-defined, semantics opaque (R4)
  Area = 617832
  Base = -> Compound021
  Description = Side piece of main structure - right corner
  FaceMaker = 0
  HorizontalArea = 0
  Length = 0
  MoveWithHost = false
  Normal = (1,0,0)
  PerimeterLength = 0
  Placement = pos=(656.998,0,0) rot=(0,0,1;0rad)
  Role = 0
  Sheets = 1
  Tag = FRA-A/F2
  Thickness = 18
  VerticalArea = 0
  WaveDirection = 0
  WaveHeight = 0
  WaveLength = 0
  WaveType = 0
  Width = 0
FEATURE [Part::FeaturePython] Panel056  label="Side right corner 002"  # WARN: FeaturePython — macro-defined, semantics opaque (R4)
  Area = 617832
  CloneOf = -> Panel053
  Description = Side piece of main structure - right corner
  FaceMaker = 0
  HorizontalArea = 0
  Length = 0
  MoveWithHost = false
  Normal = (0,0,0)
  PerimeterLength = 0
  Placement = pos=(524.997,0,0) rot=(0,0,1;0rad)
  Role = 0
  Sheets = 1
  Tag = FRA-A/F2
  Thickness = 18
  VerticalArea = 0
  WaveDirection = 0
  WaveHeight = 0
  WaveLength = 0
  WaveType = 0
  Width = 0
FEATURE [Part::FeaturePython] Panel064  label="Side right corner 003"  # WARN: FeaturePython — macro-defined, semantics opaque (R4)
  Area = 617832
  CloneOf = -> Panel053
  Description = Side piece of main structure - right corner
  FaceMaker = 0
  HorizontalArea = 0
  Length = 0
  MoveWithHost = false
  Normal = (0,0,0)
  PerimeterLength = 0
  Placement = pos=(-543.002,0,0) rot=(0,0,1;0rad)
  Role = 0
  Sheets = 1
  Tag = FRA-A/F2
  Thickness = 18
  VerticalArea = 0
  WaveDirection = 0
  WaveHeight = 0
  WaveLength = 0
  WaveType = 0
  Width = 0
FEATURE [Part::FeaturePython] Panel070  label="Side right corner 004"  # WARN: FeaturePython — macro-defined, semantics opaque (R4)
  Area = 617832
  CloneOf = -> Panel053
  Description = Side piece of main structure - right corner
  FaceMaker = 0
  HorizontalArea = 0
  Length = 0
  MoveWithHost = false
  Normal = (0,0,0)
  PerimeterLength = 0
  Placement = pos=(-675.002,0,0) rot=(0,0,1;0rad)
  Role = 0
  Sheets = 1
  Tag = FRA-A/F2
  Thickness = 18
  VerticalArea = 0
  WaveDirection = 0
  WaveHeight = 0
  WaveLength = 0
  WaveType = 0
  Width = 0
FEATURE [Part::FeaturePython] PanelView005  label="View of Side right corner 001"  # WARN: FeaturePython — macro-defined, semantics opaque (R4)
  FontFile = <userpath>/.fonts/stick/1CamBam_Stick_2.ttf
  MakeFace = true
  Placement = pos=(2200,-1200,0) rot=(0,0,1;0rad)
  Source = -> Panel053
  TagPosition = (62.8665,-333.481,0)
  TagRotation = 0
  TagSize = 10
  TagText = %tag%
FEATURE [Part::FeaturePython] PanelView008  label="View of Side right corner 002"  # WARN: FeaturePython — macro-defined, semantics opaque (R4)
  FontFile = <userpath>/.fonts/stick/1CamBam_Stick_2.ttf
  MakeFace = true
  Placement = pos=(2200,-2300,0) rot=(0,0,1;0rad)
  Source = -> Panel056
  TagPosition = (52.708,-341.481,0)
  TagRotation = 0
  TagSize = 10
  TagText = %tag%
FEATURE [Part::FeaturePython] PanelView053  label="View of Side right corner 003"  # WARN: FeaturePython — macro-defined, semantics opaque (R4)
  FontFile = <userpath>/.fonts/stick/1CamBam_Stick_2.ttf
  MakeFace = false
  Placement = pos=(-1800,500,0) rot=(0,0,1;0rad)
  Source = -> Panel064
  TagPosition = (170.088,-349.264,0)
  TagRotation = 0
  TagSize = 10
  TagText = %tag%
FEATURE [Part::FeaturePython] PanelView059  label="View of Side right corner 004"  # WARN: FeaturePython — macro-defined, semantics opaque (R4)
  FontFile = <userpath>/.fonts/stick/1CamBam_Stick_2.ttf
  MakeFace = false
  Placement = pos=(-3800,500,0) rot=(0,0,1;0rad)
  Source = -> Panel070
  TagPosition = (153.203,-347.877,0)
  TagRotation = 0
  TagSize = 10
  TagText = %tag%
FEATURE [Part::FeaturePython] PanelView220  label="View of Side right corner 005"  # WARN: FeaturePython — macro-defined, semantics opaque (R4)
  FontFile = <userpath>/.fonts/stick/1CamBam_Stick_2.ttf
  MakeFace = false
  Placement = pos=(-200,-3100,0) rot=(0,0,1;0rad)
  Source = -> Panel070
  TagPosition = (247.289,-356.411,0)
  TagRotation = 0
  TagSize = 10
  TagText = %tag%
FEATURE [Part::FeaturePython] PanelView226  label="View of Side right corner 006"  # WARN: FeaturePython — macro-defined, semantics opaque (R4)
  FontFile = <userpath>/.fonts/stick/1CamBam_Stick_2.ttf
  MakeFace = false
  Placement = pos=(0,-1900,0) rot=(0,0,1;0rad)
  Source = -> Panel064
  TagPosition = (144.982,-341.616,0)
  TagRotation = 0
  TagSize = 10
  TagText = %tag%
FEATURE [Part::Feature] Wire152  label="Wire203"
  shape: bbox 2e-07 x 1005 x 1835 mm, 0 faces, 0 solids (baked)
FEATURE [Part::Compound] Compound015
  Links = -> [Shape034064,Shape034046,Clone2D004,Clone031,Clone029,Clone033,Clone034,Clone032,Clone030,Clone035,Clone038,Clone036,Clone037,Clone040,Clone041,Clone043,Clone039,Clone042,Clone044,Clone2D003,Wire152]
FEATURE [Part::FeaturePython] Panel050  label="Side left corner 001"  # WARN: FeaturePython — macro-defined, semantics opaque (R4)
  Area = 630619
  Base = -> Compound015
  Description = Side piece of main structure - left corner
  FaceMaker = 0
  HorizontalArea = 0
  Length = 0
  MoveWithHost = false
  Normal = (1,0,0)
  PerimeterLength = 0
  Placement = pos=(656.998,0,0) rot=(0,0,1;0rad)
  Role = 0
  Sheets = 1
  Tag = FRA-A/F6
  Thickness = 18
  VerticalArea = 0
  WaveDirection = 0
  WaveHeight = 0
  WaveLength = 0
  WaveType = 0
  Width = 0
FEATURE [Part::FeaturePython] Panel059  label="Side left corner 002"  # WARN: FeaturePython — macro-defined, semantics opaque (R4)
  Area = 630619
  CloneOf = -> Panel050
  Description = Side piece of main structure - left corner
  FaceMaker = 0
  HorizontalArea = 0
  Length = 0
  MoveWithHost = false
  Normal = (0,0,0)
  PerimeterLength = 0
  Placement = pos=(524.997,0,0) rot=(0,0,1;0rad)
  Role = 0
  Sheets = 1
  Tag = FRA-A/F6
  Thickness = 18
  VerticalArea = 0
  WaveDirection = 0
  WaveHeight = 0
  WaveLength = 0
  WaveType = 0
  Width = 0
FEATURE [Part::FeaturePython] Panel066  label="Side left corner 003"  # WARN: FeaturePython — macro-defined, semantics opaque (R4)
  Area = 630619
  CloneOf = -> Panel050
  Description = Side piece of main structure - left corner
  FaceMaker = 0
  HorizontalArea = 0
  Length = 0
  MoveWithHost = false
  Normal = (0,0,0)
  PerimeterLength = 0
  Placement = pos=(-543.002,0,0) rot=(0,0,1;0rad)
  Role = 0
  Sheets = 1
  Tag = FRA-A/F6
  Thickness = 18
  VerticalArea = 0
  WaveDirection = 0
  WaveHeight = 0
  WaveLength = 0
  WaveType = 0
  Width = 0
FEATURE [Part::FeaturePython] Panel068  label="Side left corner 004"  # WARN: FeaturePython — macro-defined, semantics opaque (R4)
  Area = 630619
  CloneOf = -> Panel050
  Description = Side piece of main structure - left corner
  FaceMaker = 0
  HorizontalArea = 0
  Length = 0
  MoveWithHost = false
  Normal = (0,0,0)
  PerimeterLength = 0
  Placement = pos=(-675.002,0,0) rot=(0,0,1;0rad)
  Role = 0
  Sheets = 1
  Tag = FRA-A/F6
  Thickness = 18
  VerticalArea = 0
  WaveDirection = 0
  WaveHeight = 0
  WaveLength = 0
  WaveType = 0
  Width = 0
FEATURE [Part::FeaturePython] PanelView  label="View of Side left corner 002"  # WARN: FeaturePython — macro-defined, semantics opaque (R4)
  FontFile = <userpath>/.fonts/stick/1CamBam_Stick_2.ttf
  MakeFace = true
  Placement = pos=(-600,2000,0) rot=(0,0,1;0rad)
  Source = -> Panel059
  TagPosition = (-135.226,348.373,0)
  TagRotation = 0
  TagSize = 10
  TagText = %tag%
FEATURE [Part::FeaturePython] PanelView002  label="View of Side left corner 001"  # WARN: FeaturePython — macro-defined, semantics opaque (R4)
  FontFile = <userpath>/.fonts/stick/1CamBam_Stick_2.ttf
  MakeFace = true
  Placement = pos=(-600,3200,0) rot=(0,0,1;0rad)
  Source = -> Panel050
  TagPosition = (-135.692,342.33,0)
  TagRotation = 0
  TagSize = 10
  TagText = %tag%
FEATURE [Part::FeaturePython] PanelView055  label="View of Side left corner 003"  # WARN: FeaturePython — macro-defined, semantics opaque (R4)
  FontFile = <userpath>/.fonts/stick/1CamBam_Stick_2.ttf
  MakeFace = false
  Placement = pos=(-1700,1000,0) rot=(0,0,1;0rad)
  Source = -> Panel066
  TagPosition = (-250.312,340.327,0)
  TagRotation = 0
  TagSize = 10
  TagText = %tag%
FEATURE [Part::FeaturePython] PanelView057  label="View of Side left corner 004"  # WARN: FeaturePython — macro-defined, semantics opaque (R4)
  FontFile = <userpath>/.fonts/stick/1CamBam_Stick_2.ttf
  MakeFace = false
  Placement = pos=(-3600,1000,0) rot=(0,0,1;0rad)
  Source = -> Panel068
  TagPosition = (-146.268,347.174,0)
  TagRotation = 0
  TagSize = 10
  TagText = %tag%
FEATURE [Part::FeaturePython] PanelView222  label="View of Side left corner 005"  # WARN: FeaturePython — macro-defined, semantics opaque (R4)
  FontFile = <userpath>/.fonts/stick/1CamBam_Stick_2.ttf
  MakeFace = false
  Placement = pos=(-600,-3200,0) rot=(0,0,1;0rad)
  Source = -> Panel068
  TagPosition = (-300,400,0)
  TagRotation = 0
  TagSize = 10
  TagText = %tag%
FEATURE [Part::FeaturePython] PanelView224  label="View of Side left corner 006"  # WARN: FeaturePython — macro-defined, semantics opaque (R4)
  FontFile = <userpath>/.fonts/stick/1CamBam_Stick_2.ttf
  MakeFace = false
  Placement = pos=(-500,-2100,0) rot=(0,0,1;0rad)
  Source = -> Panel066
  TagPosition = (-157.768,338.946,0)
  TagRotation = 0
  TagSize = 10
  TagText = %tag%
FEATURE [Part::FeaturePython] Clone045  label="Wire204"  # Draft clone (typed FeaturePython)
  AttacherType = Attacher::AttachEngine3D
  Objects = -> [Wire145]
  Placement = pos=(0,1806.99,292.999) rot=(-1,0,0;1.5708rad)
  Scale = (1,1,1)
FEATURE [Part::FeaturePython] Clone046  label="Wire205"  # Draft clone (typed FeaturePython)
  AttacherType = Attacher::AttachEngine3D
  Objects = -> [Clone045]
  Placement = pos=(0,2092.99,3592.99) rot=(1,0,0;1.5708rad)
  Scale = (1,1,1)
FEATURE [Part::FeaturePython] Clone047  label="Wire206"  # Draft clone (typed FeaturePython)
  AttacherType = Attacher::AttachEngine3D
  Objects = -> [Clone046]
  Placement = pos=(0,2092.99,3892.99) rot=(1,0,0;1.5708rad)
  Scale = (1,1,1)
FEATURE [Part::FeaturePython] Clone048  label="Wire207"  # Draft clone (typed FeaturePython)
  AttacherType = Attacher::AttachEngine3D
  Objects = -> [Clone045]
  Placement = pos=(0,1807,592.999) rot=(-1,0,0;1.5708rad)
  Scale = (1,1,1)
FEATURE [Part::FeaturePython] Clone049  label="Wire208"  # Draft clone (typed FeaturePython)
  AttacherType = Attacher::AttachEngine3D
  Objects = -> [Clone047]
  Placement = pos=(0,491.557,3845.26) rot=(1,0,0;2.48591rad)
  Scale = (1,1,1)
FEATURE [Part::FeaturePython] Clone050  label="Wire209"  # Draft clone (typed FeaturePython)
  AttacherType = Attacher::AttachEngine3D
  Objects = -> [Clone049]
  Placement = pos=(0,2932.85,1606.55) rot=(-1,0,0;0.655692rad)
  Scale = (1,1,1)
FEATURE [Part::FeaturePython] Clone051  label="Wire210"  # Draft clone (typed FeaturePython)
  AttacherType = Attacher::AttachEngine3D
  Objects = -> [Clone050]
  Placement = pos=(0,2695.06,1789.46) rot=(-1,0,0;0.655692rad)
  Scale = (1,1,1)
FEATURE [Part::FeaturePython] Clone052  label="Wire211"  # Draft clone (typed FeaturePython)
  AttacherType = Attacher::AttachEngine3D
  Objects = -> [Clone049]
  Placement = pos=(0,253.77,4028.17) rot=(1,0,0;2.48591rad)
  Scale = (1,1,1)
FEATURE [Part::FeaturePython] Clone053  label="Wire212"  # Draft clone (typed FeaturePython)
  AttacherType = Attacher::AttachEngine3D
  Objects = -> [Clone049]
  Placement = pos=(0,15.9832,4211.09) rot=(1,0,0;2.48591rad)
  Scale = (1,1,1)
FEATURE [Part::FeaturePython] Clone054  label="Wire213"  # Draft clone (typed FeaturePython)
  AttacherType = Attacher::AttachEngine3D
  Objects = -> [Clone050]
  Placement = pos=(0,2457.28,1972.37) rot=(-1,0,0;0.655692rad)
  Scale = (1,1,1)
FEATURE [Part::FeaturePython] Clone055  label="Wire214"  # Draft clone (typed FeaturePython)
  AttacherType = Attacher::AttachEngine3D
  Objects = -> [Clone051]
  Placement = pos=(0,2195.71,2173.57) rot=(-1,0,0;0.655692rad)
  Scale = (1,1,1)
FEATURE [Part::FeaturePython] Clone056  label="Wire215"  # Draft clone (typed FeaturePython)
  AttacherType = Attacher::AttachEngine3D
  Objects = -> [Clone052]
  Placement = pos=(0,-245.583,4412.29) rot=(1,0,0;2.48591rad)
  Scale = (1,1,1)
FEATURE [Part::FeaturePython] Clone057  label="Wire216"  # Draft clone (typed FeaturePython)
  AttacherType = Attacher::AttachEngine3D
  Objects = -> [Clone055]
  Placement = pos=(0,1934.07,2374.83) rot=(-1,0,0;0.655692rad)
  Scale = (1,1,1)
FEATURE [Part::FeaturePython] Clone058  label="Wire217"  # Draft clone (typed FeaturePython)
  AttacherType = Attacher::AttachEngine3D
  Objects = -> [Clone056]
  Placement = pos=(0,-507.22,4613.55) rot=(1,0,0;2.48591rad)
  Scale = (1,1,1)
FEATURE [Part::Part2DObjectPython] Clone2D005  label="DWire012 (2D)003"  # Draft 2D object (typed FeaturePython)
  Objects = -> [DWire012]
  Placement = pos=(0,3252.28,4001.41) rot=(1,0,0;0.915099rad)
  Scale = (1,1,1)
FEATURE [Part::Part2DObjectPython] Clone2D006  label="DWire012 (2D)003 (2D)"  # Draft 2D object (typed FeaturePython)
  Objects = -> [Clone2D005]
  Placement = pos=(0,2729,4403.93) rot=(1,0,0;0.915099rad)
  Scale = (1,1,1)
FEATURE [Part::Compound] Compound017
  Links = -> [Shape034067,Clone045,Clone050,Clone046,Clone049,Clone047,Clone048,Clone051,Clone055,Clone053,Clone052,Clone056,Clone054,Clone057,Clone058,Clone2D006,Clone2D005]
FEATURE [Part::FeaturePython] Panel051  label="Side side 001"  # WARN: FeaturePython — macro-defined, semantics opaque (R4)
  Area = 638324
  Base = -> Compound017
  Description = Side piece of main structure - side angle
  FaceMaker = 0
  HorizontalArea = 0
  Length = 0
  MoveWithHost = false
  Normal = (1,0,0)
  PerimeterLength = 0
  Placement = pos=(656.998,0,0) rot=(0,0,1;0rad)
  Role = 0
  Sheets = 1
  Tag = FRA-A/F5
  Thickness = 18
  VerticalArea = 0
  WaveDirection = 0
  WaveHeight = 0
  WaveLength = 0
  WaveType = 0
  Width = 0
FEATURE [Part::FeaturePython] Panel054  label="Side side 002"  # WARN: FeaturePython — macro-defined, semantics opaque (R4)
  Area = 638324
  CloneOf = -> Panel051
  Description = Side piece of main structure - side angle
  FaceMaker = 0
  HorizontalArea = 0
  Length = 0
  MoveWithHost = false
  Normal = (0,0,0)
  PerimeterLength = 0
  Placement = pos=(674.998,0,0) rot=(0,0,1;3.14159rad)
  Role = 0
  Sheets = 1
  Tag = FRA-A/F5
  Thickness = 18
  VerticalArea = 0
  WaveDirection = 0
  WaveHeight = 0
  WaveLength = 0
  WaveType = 0
  Width = 0
FEATURE [Part::FeaturePython] Panel055  label="Side side 003"  # WARN: FeaturePython — macro-defined, semantics opaque (R4)
  Area = 638324
  CloneOf = -> Panel051
  Description = Side piece of main structure - side angle
  FaceMaker = 0
  HorizontalArea = 0
  Length = 0
  MoveWithHost = false
  Normal = (0,0,0)
  PerimeterLength = 0
  Placement = pos=(542.997,0,0) rot=(0,0,1;3.14159rad)
  Role = 0
  Sheets = 1
  Tag = FRA-A/F5
  Thickness = 18
  VerticalArea = 0
  WaveDirection = 0
  WaveHeight = 0
  WaveLength = 0
  WaveType = 0
  Width = 0
FEATURE [Part::FeaturePython] Panel058  label="Side side 004"  # WARN: FeaturePython — macro-defined, semantics opaque (R4)
  Area = 638324
  CloneOf = -> Panel051
  Description = Side piece of main structure - side angle
  FaceMaker = 0
  HorizontalArea = 0
  Length = 0
  MoveWithHost = false
  Normal = (0,0,0)
  PerimeterLength = 0
  Placement = pos=(524.997,0,0) rot=(0,0,1;0rad)
  Role = 0
  Sheets = 1
  Tag = FRA-A/F5
  Thickness = 18
  VerticalArea = 0
  WaveDirection = 0
  WaveHeight = 0
  WaveLength = 0
  WaveType = 0
  Width = 0
FEATURE [Part::FeaturePython] Panel061  label="Side side 005"  # WARN: FeaturePython — macro-defined, semantics opaque (R4)
  Area = 638324
  CloneOf = -> Panel051
  Description = Side piece of main structure - side angle
  FaceMaker = 0
  HorizontalArea = 0
  Length = 0
  MoveWithHost = false
  Normal = (0,0,0)
  PerimeterLength = 0
  Placement = pos=(-525.002,0,0) rot=(0,0,1;3.14159rad)
  Role = 0
  Sheets = 1
  Tag = FRA-A/F5
  Thickness = 18
  VerticalArea = 0
  WaveDirection = 0
  WaveHeight = 0
  WaveLength = 0
  WaveType = 0
  Width = 0
FEATURE [Part::FeaturePython] Panel062  label="Side side 006"  # WARN: FeaturePython — macro-defined, semantics opaque (R4)
  Area = 638324
  CloneOf = -> Panel051
  Description = Side piece of main structure - side angle
  FaceMaker = 0
  HorizontalArea = 0
  Length = 0
  MoveWithHost = false
  Normal = (0,0,0)
  PerimeterLength = 0
  Placement = pos=(-543.002,0,0) rot=(0,0,1;0rad)
  Role = 0
  Sheets = 1
  Tag = FRA-A/F5
  Thickness = 18
  VerticalArea = 0
  WaveDirection = 0
  WaveHeight = 0
  WaveLength = 0
  WaveType = 0
  Width = 0
FEATURE [Part::FeaturePython] Panel067  label="Side side 007"  # WARN: FeaturePython — macro-defined, semantics opaque (R4)
  Area = 638324
  CloneOf = -> Panel051
  Description = Side piece of main structure - side angle
  FaceMaker = 0
  HorizontalArea = 0
  Length = 0
  MoveWithHost = false
  Normal = (0,0,0)
  PerimeterLength = 0
  Placement = pos=(-657.002,0,0) rot=(0,0,1;3.14159rad)
  Role = 0
  Sheets = 1
  Tag = FRA-A/F5
  Thickness = 18
  VerticalArea = 0
  WaveDirection = 0
  WaveHeight = 0
  WaveLength = 0
  WaveType = 0
  Width = 0
FEATURE [Part::FeaturePython] Panel072  label="Side side 008"  # WARN: FeaturePython — macro-defined, semantics opaque (R4)
  Area = 638324
  CloneOf = -> Panel051
  Description = Side piece of main structure - side angle
  FaceMaker = 0
  HorizontalArea = 0
  Length = 0
  MoveWithHost = false
  Normal = (0,0,0)
  PerimeterLength = 0
  Placement = pos=(-675.002,0,0) rot=(0,0,1;0rad)
  Role = 0
  Sheets = 1
  Tag = FRA-A/F5
  Thickness = 18
  VerticalArea = 0
  WaveDirection = 0
  WaveHeight = 0
  WaveLength = 0
  WaveType = 0
  Width = 0
FEATURE [Part::FeaturePython] PanelView003  label="View of Side side 001"  # WARN: FeaturePython — macro-defined, semantics opaque (R4)
  FontFile = <userpath>/.fonts/stick/1CamBam_Stick_2.ttf
  MakeFace = true
  Placement = pos=(-2210.23,1444.6,0) rot=(0,0,1;0rad)
  Source = -> Panel051
  TagPosition = (-372.392,646.477,0)
  TagRotation = 0
  TagSize = 10
  TagText = %tag%
FEATURE [Part::FeaturePython] PanelView006  label="View of Side side 002"  # WARN: FeaturePython — macro-defined, semantics opaque (R4)
  FontFile = <userpath>/.fonts/stick/1CamBam_Stick_2.ttf
  MakeFace = true
  Placement = pos=(-2320.22,902.125,0) rot=(0,0,1;0rad)
  Source = -> Panel054
  TagPosition = (-354.054,640.212,0)
  TagRotation = 0
  TagSize = 10
  TagText = %tag%
FEATURE [Part::FeaturePython] PanelView007  label="View of Side side 003"  # WARN: FeaturePython — macro-defined, semantics opaque (R4)
  FontFile = <userpath>/.fonts/stick/1CamBam_Stick_2.ttf
  MakeFace = true
  Placement = pos=(-2431.12,309.001,0) rot=(0,0,1;0rad)
  Source = -> Panel055
  TagPosition = (-452.406,645.864,0)
  TagRotation = 0
  TagSize = 10
  TagText = %tag%
FEATURE [Part::FeaturePython] PanelView010  label="View of Side side 004"  # WARN: FeaturePython — macro-defined, semantics opaque (R4)
  FontFile = <userpath>/.fonts/stick/1CamBam_Stick_2.ttf
  MakeFace = true
  Placement = pos=(-2416.01,-460.472,0) rot=(0,0,1;0rad)
  Source = -> Panel058
  TagPosition = (-480.267,641.482,0)
  TagRotation = 0
  TagSize = 10
  TagText = %tag%
FEATURE [Part::FeaturePython] PanelView050  label="View of Side side 005"  # WARN: FeaturePython — macro-defined, semantics opaque (R4)
  FontFile = <userpath>/.fonts/stick/1CamBam_Stick_2.ttf
  MakeFace = false
  Placement = pos=(4900,-2400,0) rot=(0,0,1;0rad)
  Source = -> Panel061
  TagPosition = (-274.633,654.289,0)
  TagRotation = 0
  TagSize = 10
  TagText = %tag%
FEATURE [Part::FeaturePython] PanelView051  label="View of Side side 006"  # WARN: FeaturePython — macro-defined, semantics opaque (R4)
  FontFile = <userpath>/.fonts/stick/1CamBam_Stick_2.ttf
  MakeFace = false
  Placement = pos=(6381.54,-2269.86,0) rot=(0,0,1;0rad)
  Source = -> Panel062
  TagPosition = (-254.408,653.475,0)
  TagRotation = 0
  TagSize = 10
  TagText = %tag%
FEATURE [Part::FeaturePython] PanelView056  label="View of Side side 007"  # WARN: FeaturePython — macro-defined, semantics opaque (R4)
  FontFile = <userpath>/.fonts/stick/1CamBam_Stick_2.ttf
  MakeFace = false
  Placement = pos=(4613.13,-2873.6,0) rot=(0,0,1;0rad)
  Source = -> Panel067
  TagPosition = (-286.738,648.223,0)
  TagRotation = 0
  TagSize = 10
  TagText = %tag%
FEATURE [Part::FeaturePython] PanelView061  label="View of Side side 008"  # WARN: FeaturePython — macro-defined, semantics opaque (R4)
  FontFile = <userpath>/.fonts/stick/1CamBam_Stick_2.ttf
  MakeFace = false
  Placement = pos=(7598.86,-2103.6,0) rot=(0,0,1;0rad)
  Source = -> Panel072
  TagPosition = (-261.602,656.344,0)
  TagRotation = 0
  TagSize = 10
  TagText = %tag%
FEATURE [Part::FeaturePython] PanelView217  label="View of Side side 009"  # WARN: FeaturePython — macro-defined, semantics opaque (R4)
  FontFile = <userpath>/.fonts/stick/1CamBam_Stick_2.ttf
  MakeFace = false
  Placement = pos=(9300,-100,0) rot=(0,0,1;0rad)
  Source = -> Panel061
  TagPosition = (-384.293,651.581,0)
  TagRotation = 0
  TagSize = 10
  TagText = %tag%
FEATURE [Part::FeaturePython] PanelView218  label="View of Side side 010"  # WARN: FeaturePython — macro-defined, semantics opaque (R4)
  FontFile = <userpath>/.fonts/stick/1CamBam_Stick_2.ttf
  MakeFace = false
  Placement = pos=(9800,-4200,0) rot=(0,0,1;0rad)
  Source = -> Panel072
  TagPosition = (-439.334,648.056,0)
  TagRotation = 0
  TagSize = 10
  TagText = %tag%
FEATURE [Part::FeaturePython] PanelView223  label="View of Side side 011"  # WARN: FeaturePython — macro-defined, semantics opaque (R4)
  FontFile = <userpath>/.fonts/stick/1CamBam_Stick_2.ttf
  MakeFace = false
  Placement = pos=(9600,-1400,0) rot=(0,0,1;0rad)
  Source = -> Panel067
  TagPosition = (-331.307,638.55,0)
  TagRotation = 0
  TagSize = 10
  TagText = %tag%
FEATURE [Part::FeaturePython] PanelView228  label="View of Side side 012"  # WARN: FeaturePython — macro-defined, semantics opaque (R4)
  FontFile = <userpath>/.fonts/stick/1CamBam_Stick_2.ttf
  MakeFace = false
  Placement = pos=(9700,-2900,0) rot=(0,0,1;0rad)
  Source = -> Panel062
  TagPosition = (-371.845,650.561,0)
  TagRotation = 0
  TagSize = 10
  TagText = %tag%
FEATURE [Part::FeaturePython] Clone059  label="Wire218"  # Draft clone (typed FeaturePython)
  AttacherType = Attacher::AttachEngine3D
  Objects = -> [Wire145]
  Placement = pos=(0,919.442,4569.84) rot=(1,0,0;0.655695rad)
  Scale = (1,1,1)
FEATURE [Part::FeaturePython] Clone060  label="Wire219"  # Draft clone (typed FeaturePython)
  AttacherType = Attacher::AttachEngine3D
  Objects = -> [Clone059]
  Placement = pos=(0,-1870.59,2784.49) rot=(1,0,0;3.79729rad)
  Scale = (1,1,1)
FEATURE [Part::FeaturePython] Clone061  label="Wire220"  # Draft clone (typed FeaturePython)
  AttacherType = Attacher::AttachEngine3D
  Objects = -> [Clone060]
  Placement = pos=(0,-1632.8,2967.4) rot=(1,0,0;3.79729rad)
  Scale = (1,1,1)
FEATURE [Part::FeaturePython] Clone062  label="Wire221"  # Draft clone (typed FeaturePython)
  AttacherType = Attacher::AttachEngine3D
  Objects = -> [Clone059]
  Placement = pos=(0,1157.23,4752.76) rot=(1,0,0;0.655695rad)
  Scale = (1,1,1)
FEATURE [Part::FeaturePython] Clone063  label="Wire222"  # Draft clone (typed FeaturePython)
  AttacherType = Attacher::AttachEngine3D
  Objects = -> [Clone062]
  Placement = pos=(0,1458.43,2740.72) rot=(-1,0,0;0.655693rad)
  Scale = (1,1,1)
FEATURE [Part::FeaturePython] Clone064  label="Wire223"  # Draft clone (typed FeaturePython)
  AttacherType = Attacher::AttachEngine3D
  Objects = -> [Clone063]
  Placement = pos=(0,-982.852,4979.45) rot=(1,0,0;2.4859rad)
  Scale = (1,1,1)
FEATURE [Part::FeaturePython] Clone065  label="Wire224"  # Draft clone (typed FeaturePython)
  AttacherType = Attacher::AttachEngine3D
  Objects = -> [Clone063]
  Placement = pos=(0,1696.21,2557.8) rot=(-1,0,0;0.655693rad)
  Scale = (1,1,1)
FEATURE [Part::FeaturePython] Clone066  label="Wire225"  # Draft clone (typed FeaturePython)
  AttacherType = Attacher::AttachEngine3D
  Objects = -> [Clone064]
  Placement = pos=(0,-745.066,4796.53) rot=(1,0,0;2.4859rad)
  Scale = (1,1,1)
FEATURE [Part::Compound] Compound013
  Links = -> [Shape034040,Clone059,Clone064,Clone062,Clone060,Clone061,Clone066,Clone063,Clone065]
FEATURE [Part::FeaturePython] Panel049  label="Side top 001"  # WARN: FeaturePython — macro-defined, semantics opaque (R4)
  Area = 393515
  Base = -> Compound013
  Description = Side piece of main structure - top
  FaceMaker = 0
  HorizontalArea = 0
  Length = 0
  MoveWithHost = false
  Normal = (1,0,0)
  PerimeterLength = 0
  Placement = pos=(656.998,0,0) rot=(0,0,1;0rad)
  Role = 0
  Sheets = 1
  Tag = FRA-A/F4
  Thickness = 18
  VerticalArea = 0
  WaveDirection = 0
  WaveHeight = 0
  WaveLength = 0
  WaveType = 0
  Width = 0
FEATURE [Part::FeaturePython] Panel060  label="Side top 002"  # WARN: FeaturePython — macro-defined, semantics opaque (R4)
  Area = 393515
  CloneOf = -> Panel049
  Description = Side piece of main structure - top
  FaceMaker = 0
  HorizontalArea = 0
  Length = 0
  MoveWithHost = false
  Normal = (0,0,0)
  PerimeterLength = 0
  Placement = pos=(524.997,0,0) rot=(0,0,1;0rad)
  Role = 0
  Sheets = 1
  Tag = FRA-A/F4
  Thickness = 18
  VerticalArea = 0
  WaveDirection = 0
  WaveHeight = 0
  WaveLength = 0
  WaveType = 0
  Width = 0
FEATURE [Part::FeaturePython] Panel065  label="Side top 003"  # WARN: FeaturePython — macro-defined, semantics opaque (R4)
  Area = 393515
  CloneOf = -> Panel049
  Description = Side piece of main structure - top
  FaceMaker = 0
  HorizontalArea = 0
  Length = 0
  MoveWithHost = false
  Normal = (0,0,0)
  PerimeterLength = 0
  Placement = pos=(-543.002,0,0) rot=(0,0,1;0rad)
  Role = 0
  Sheets = 1
  Tag = FRA-A/F4
  Thickness = 18
  VerticalArea = 0
  WaveDirection = 0
  WaveHeight = 0
  WaveLength = 0
  WaveType = 0
  Width = 0
FEATURE [Part::FeaturePython] Panel069  label="Side top 004"  # WARN: FeaturePython — macro-defined, semantics opaque (R4)
  Area = 393515
  CloneOf = -> Panel049
  Description = Side piece of main structure - top
  FaceMaker = 0
  HorizontalArea = 0
  Length = 0
  MoveWithHost = false
  Normal = (0,0,0)
  PerimeterLength = 0
  Placement = pos=(-675.002,0,0) rot=(0,0,1;0rad)
  Role = 0
  Sheets = 1
  Tag = FRA-A/F4
  Thickness = 18
  VerticalArea = 0
  WaveDirection = 0
  WaveHeight = 0
  WaveLength = 0
  WaveType = 0
  Width = 0
FEATURE [App::DocumentObjectGroupPython] VisGroup  label="level1 sides (0 originals)"  # scripted group (container) (typed FeaturePython)
  Group = -> [Panel061,Panel062,Panel063,Panel064,Panel065,Panel066,Panel067,Panel068,Panel069,Panel070,Panel071,Panel072]
FEATURE [App::DocumentObjectGroupPython] VisGroup009  label="Endcap side panels (5 originals)"  # scripted group (container) (typed FeaturePython)
  Group = -> [Panel059,Panel058,Panel057,Panel056,Panel055,Panel060,Panel051,Panel050,Panel049,Panel054,Panel053,Panel052]
FEATURE [Part::FeaturePython] PanelView001  label="View of Side top 001"  # WARN: FeaturePython — macro-defined, semantics opaque (R4)
  FontFile = <userpath>/.fonts/stick/1CamBam_Stick_2.ttf
  MakeFace = true
  Placement = pos=(4400,900,0) rot=(0,0,1;0rad)
  Source = -> Panel049
  TagPosition = (187.332,1.40747,0)
  TagRotation = 0
  TagSize = 10
  TagText = %tag%
FEATURE [Part::FeaturePython] PanelView011  label="View of Side top 002"  # WARN: FeaturePython — macro-defined, semantics opaque (R4)
  FontFile = <userpath>/.fonts/stick/1CamBam_Stick_2.ttf
  MakeFace = true
  Placement = pos=(5400,800,0) rot=(0,0,1;0rad)
  Source = -> Panel060
  TagPosition = (153.597,67.7664,0)
  TagRotation = 0
  TagSize = 10
  TagText = %tag%
FEATURE [Part::FeaturePython] PanelView054  label="View of Side top 003"  # WARN: FeaturePython — macro-defined, semantics opaque (R4)
  FontFile = <userpath>/.fonts/stick/1CamBam_Stick_2.ttf
  MakeFace = false
  Placement = pos=(-3300,-1100,0) rot=(0,0,1;0rad)
  Source = -> Panel065
  TagPosition = (200,0,0)
  TagRotation = 0
  TagSize = 10
  TagText = %tag%
FEATURE [Part::FeaturePython] PanelView058  label="View of Side top 004"  # WARN: FeaturePython — macro-defined, semantics opaque (R4)
  FontFile = <userpath>/.fonts/stick/1CamBam_Stick_2.ttf
  MakeFace = false
  Placement = pos=(-4000,-1000,0) rot=(0,0,1;0rad)
  Source = -> Panel069
  TagPosition = (200,0,0)
  TagRotation = 0
  TagSize = 10
  TagText = %tag%
FEATURE [Part::FeaturePython] PanelView221  label="View of Side top 005"  # WARN: FeaturePython — macro-defined, semantics opaque (R4)
  FontFile = <userpath>/.fonts/stick/1CamBam_Stick_2.ttf
  MakeFace = false
  Placement = pos=(-1900,100,0) rot=(0,0,1;0rad)
  Source = -> Panel069
  TagPosition = (200,0,0)
  TagRotation = 0
  TagSize = 10
  TagText = %tag%
FEATURE [Part::FeaturePython] PanelView225  label="View of Side top 006"  # WARN: FeaturePython — macro-defined, semantics opaque (R4)
  FontFile = <userpath>/.fonts/stick/1CamBam_Stick_2.ttf
  MakeFace = false
  Placement = pos=(-1900,-1500,0) rot=(0,0,1;0rad)
  Source = -> Panel065
  TagPosition = (200,0,0)
  TagRotation = 0
  TagSize = 10
  TagText = %tag%
FEATURE [Part::FeaturePython] Clone067  label="Base hole001"  # Draft clone (typed FeaturePython)
  AttacherType = Attacher::AttachEngine3D
  Objects = -> [Wire145]
  Placement = pos=(656.999,2999.99,-3.05174e-05) rot=(0,0,1;0rad)
  Scale = (1,1,1)
FEATURE [Part::FeaturePython] Clone068  label="Base hole002"  # Draft clone (typed FeaturePython)
  AttacherType = Attacher::AttachEngine3D
  Objects = -> [Clone067]
  Placement = pos=(656.999,-300.001,285.999) rot=(1,0,0;3.14159rad)
  Scale = (1,1,1)
FEATURE [Part::FeaturePython] Clone069  label="Base hole003"  # Draft clone (typed FeaturePython)
  AttacherType = Attacher::AttachEngine3D
  Objects = -> [Clone068]
  Placement = pos=(656.999,-0.00170897,285.999) rot=(1,0,0;3.14159rad)
  Scale = (1,1,1)
FEATURE [Part::FeaturePython] Clone070  label="Base hole004"  # Draft clone (typed FeaturePython)
  AttacherType = Attacher::AttachEngine3D
  Objects = -> [Clone067]
  Placement = pos=(656.999,3299.99,-3.05174e-05) rot=(0,0,1;0rad)
  Scale = (1,1,1)
FEATURE [Part::FeaturePython] Clone071  label="Base hole005"  # Draft clone (typed FeaturePython)
  AttacherType = Attacher::AttachEngine3D
  Objects = -> [Clone070]
  Placement = pos=(656.999,2092.99,2093) rot=(1,0,0;1.5708rad)
  Scale = (1,1,1)
FEATURE [Part::FeaturePython] Clone072  label="Base hole006"  # Draft clone (typed FeaturePython)
  AttacherType = Attacher::AttachEngine3D
  Objects = -> [Clone069]
  Placement = pos=(656.999,1807,-1207) rot=(-1,0,0;1.5708rad)
  Scale = (1,1,1)
FEATURE [Part::FeaturePython] Clone073  label="Base hole007"  # Draft clone (typed FeaturePython)
  AttacherType = Attacher::AttachEngine3D
  Objects = -> [Clone072]
  Placement = pos=(656.999,1807,-906.999) rot=(-1,0,0;1.5708rad)
  Scale = (1,1,1)
FEATURE [Part::FeaturePython] Clone074  label="Base hole008"  # Draft clone (typed FeaturePython)
  AttacherType = Attacher::AttachEngine3D
  Objects = -> [Clone071]
  Placement = pos=(656.999,2092.99,2393) rot=(1,0,0;1.5708rad)
  Scale = (1,1,1)
FEATURE [Part::FeaturePython] Clone075  label="Base hole009"  # Draft clone (typed FeaturePython)
  AttacherType = Attacher::AttachEngine3D
  Objects = -> [Clone072]
  Placement = pos=(656.999,1807,-1507) rot=(-1,0,0;1.5708rad)
  Scale = (1,1,1)
FEATURE [Part::Part2DObjectPython] DWire013  # Draft 2D object (typed FeaturePython)
  ChamferSize = 0
  Closed = true
  End = (656.999,1959,152)
  FilletRadius = 0
  Length = 683.998
  MakeFace = false
  Points = (30) [(656.999,1959,292.999),(656.999,1965,292.999),(656.999,1965,300.999),(656.999,1959,300.999),(656.999,1940.99,300.999),(656.999,1934.99,300.999),+24 more]
  Start = (656.999,1959,292.999)
  Subdivisions = 0
FEATURE [Part::FeaturePython] Clone076  label="Base hole010"  # Draft clone (typed FeaturePython)
  AttacherType = Attacher::AttachEngine3D
  Objects = -> [Clone073]
  Placement = pos=(656.999,1807,292.999) rot=(-1,0,0;1.5708rad)
  Scale = (1,1,1)
FEATURE [Part::FeaturePython] Clone077  label="Base hole011"  # Draft clone (typed FeaturePython)
  AttacherType = Attacher::AttachEngine3D
  Objects = -> [Clone076]
  Placement = pos=(656.999,2092.99,3592.99) rot=(1,0,0;1.5708rad)
  Scale = (1,1,1)
FEATURE [Part::FeaturePython] Clone078  label="Base hole012"  # Draft clone (typed FeaturePython)
  AttacherType = Attacher::AttachEngine3D
  Objects = -> [Clone077]
  Placement = pos=(656.999,2092.99,3892.99) rot=(1,0,0;1.5708rad)
  Scale = (1,1,1)
FEATURE [Part::FeaturePython] Clone079  label="Base hole013"  # Draft clone (typed FeaturePython)
  AttacherType = Attacher::AttachEngine3D
  Objects = -> [Clone076]
  Placement = pos=(656.999,1807,592.998) rot=(-1,0,0;1.5708rad)
  Scale = (1,1,1)
FEATURE [Part::FeaturePython] Clone080  label="Base hole014"  # Draft clone (typed FeaturePython)
  AttacherType = Attacher::AttachEngine3D
  Objects = -> [Clone079]
  Placement = pos=(656.999,2932.85,1606.54) rot=(-1,0,0;0.655693rad)
  Scale = (1,1,1)
FEATURE [Part::FeaturePython] Clone081  label="Base hole015"  # Draft clone (typed FeaturePython)
  AttacherType = Attacher::AttachEngine3D
  Objects = -> [Clone078]
  Placement = pos=(656.999,491.567,3845.27) rot=(1,0,0;2.4859rad)
  Scale = (1,1,1)
FEATURE [Part::FeaturePython] Clone082  label="Base hole016"  # Draft clone (typed FeaturePython)
  AttacherType = Attacher::AttachEngine3D
  Objects = -> [Clone081]
  Placement = pos=(656.999,253.78,4028.18) rot=(1,0,0;2.4859rad)
  Scale = (1,1,1)
FEATURE [Part::FeaturePython] Clone083  label="Base hole017"  # Draft clone (typed FeaturePython)
  AttacherType = Attacher::AttachEngine3D
  Objects = -> [Clone080]
  Placement = pos=(656.999,2695.06,1789.46) rot=(-1,0,0;0.655693rad)
  Scale = (1,1,1)
FEATURE [Part::Compound] Compound003  label="side reinforcement profile"
  Links = -> [Wire042,Clone076,Clone078,Clone077,Clone081,Clone079,Clone080,Clone083,Clone082]
FEATURE [Part::FeaturePython] Panel005  label="Side reinforcement 001"  # WARN: FeaturePython — macro-defined, semantics opaque (R4)
  Area = 389032
  Base = -> Compound003
  Description = Side reinforcemetn piece
  FaceMaker = 0
  HorizontalArea = 0
  Length = 0
  MoveWithHost = false
  Normal = (1,0,0)
  PerimeterLength = 0
  Placement = pos=(-18,0,0) rot=(0,0,1;0rad)
  Role = 0
  Sheets = 1
  Tag = FRA-A/R3
  Thickness = 18
  VerticalArea = 0
  WaveDirection = 0
  WaveHeight = 0
  WaveLength = 0
  WaveType = 0
  Width = 0
FEATURE [Part::FeaturePython] Panel008  label="Side reinforcement 002"  # WARN: FeaturePython — macro-defined, semantics opaque (R4)
  Area = 389032
  CloneOf = -> Panel005
  Description = Side reinforcemetn piece
  FaceMaker = 0
  HorizontalArea = 0
  Length = 0
  MoveWithHost = false
  Normal = (0,0,0)
  PerimeterLength = 0
  Placement = pos=(18,0,0) rot=(0,0,1;3.14159rad)
  Role = 0
  Sheets = 1
  Tag = FRA-A/R3
  Thickness = 18
  VerticalArea = 0
  WaveDirection = 0
  WaveHeight = 0
  WaveLength = 0
  WaveType = 0
  Width = 0
FEATURE [Part::FeaturePython] Panel010  label="Side reinforcement 003"  # WARN: FeaturePython — macro-defined, semantics opaque (R4)
  Area = 389032
  CloneOf = -> Panel005
  Description = Side reinforcemetn piece
  FaceMaker = 0
  HorizontalArea = 0
  Length = 0
  MoveWithHost = false
  Normal = (0,0,0)
  PerimeterLength = 0
  Placement = pos=(1314,0,0) rot=(0,0,1;3.14159rad)
  Role = 0
  Sheets = 1
  Tag = FRA-A/R3
  Thickness = 18
  VerticalArea = 0
  WaveDirection = 0
  WaveHeight = 0
  WaveLength = 0
  WaveType = 0
  Width = 0
FEATURE [Part::FeaturePython] Panel011  label="Side reinforcement 004"  # WARN: FeaturePython — macro-defined, semantics opaque (R4)
  Area = 389032
  CloneOf = -> Panel005
  Description = Side reinforcemetn piece
  FaceMaker = 0
  HorizontalArea = 0
  Length = 0
  MoveWithHost = false
  Normal = (0,0,0)
  PerimeterLength = 0
  Placement = pos=(-1218,0,0) rot=(0,0,1;0rad)
  Role = 0
  Sheets = 1
  Tag = FRA-A/R3
  Thickness = 18
  VerticalArea = 0
  WaveDirection = 0
  WaveHeight = 0
  WaveLength = 0
  WaveType = 0
  Width = 0
FEATURE [Part::FeaturePython] Panel013  label="Side reinforcement 005"  # WARN: FeaturePython — macro-defined, semantics opaque (R4)
  Area = 389032
  CloneOf = -> Panel005
  Description = Side reinforcemetn piece
  FaceMaker = 0
  HorizontalArea = 0
  Length = 0
  MoveWithHost = false
  Normal = (0,0,0)
  PerimeterLength = 0
  Placement = pos=(1218,0,0) rot=(0,0,1;3.14159rad)
  Role = 0
  Sheets = 1
  Tag = FRA-A/R3
  Thickness = 18
  VerticalArea = 0
  WaveDirection = 0
  WaveHeight = 0
  WaveLength = 0
  WaveType = 0
  Width = 0
FEATURE [Part::FeaturePython] Panel015  label="Side reinforcement 006"  # WARN: FeaturePython — macro-defined, semantics opaque (R4)
  Area = 389032
  CloneOf = -> Panel005
  Description = Side reinforcemetn piece
  FaceMaker = 0
  HorizontalArea = 0
  Length = 0
  MoveWithHost = false
  Normal = (0,0,0)
  PerimeterLength = 0
  Placement = pos=(-114,0,0) rot=(0,0,1;0rad)
  Role = 0
  Sheets = 1
  Tag = FRA-A/R3
  Thickness = 18
  VerticalArea = 0
  WaveDirection = 0
  WaveHeight = 0
  WaveLength = 0
  WaveType = 0
  Width = 0
FEATURE [Part::FeaturePython] Panel018  label="Side reinforcement 007"  # WARN: FeaturePython — macro-defined, semantics opaque (R4)
  Area = 389032
  CloneOf = -> Panel005
  Description = Side reinforcemetn piece
  FaceMaker = 0
  HorizontalArea = 0
  Length = 0
  MoveWithHost = false
  Normal = (0,0,0)
  PerimeterLength = 0
  Placement = pos=(113.997,0,0) rot=(0,0,1;3.14159rad)
  Role = 0
  Sheets = 1
  Tag = FRA-A/R3
  Thickness = 18
  VerticalArea = 0
  WaveDirection = 0
  WaveHeight = 0
  WaveLength = 0
  WaveType = 0
  Width = 0
FEATURE [Part::FeaturePython] Panel024  label="Side reinforcement 009"  # WARN: FeaturePython — macro-defined, semantics opaque (R4)
  Area = 389032
  CloneOf = -> Panel005
  Description = Side reinforcemetn piece
  FaceMaker = 0
  HorizontalArea = 0
  Length = 0
  MoveWithHost = false
  Normal = (0,0,0)
  PerimeterLength = 0
  Placement = pos=(-1314,0,0) rot=(0,0,1;0rad)
  Role = 0
  Sheets = 1
  Tag = FRA-A/R3
  Thickness = 18
  VerticalArea = 0
  WaveDirection = 0
  WaveHeight = 0
  WaveLength = 0
  WaveType = 0
  Width = 0
FEATURE [Part::FeaturePython] PanelView012  label="View of Side reinforcement 006"  # WARN: FeaturePython — macro-defined, semantics opaque (R4)
  FontFile = <userpath>/.fonts/stick/1CamBam_Stick_2.ttf
  MakeFace = true
  Placement = pos=(200,-1600,0) rot=(0,0,1;0rad)
  Source = -> Panel015
  TagPosition = (-59.7954,253.962,0)
  TagRotation = 0
  TagSize = 10
  TagText = %tag%
FEATURE [Part::FeaturePython] PanelView014  label="View of Side reinforcement 001"  # WARN: FeaturePython — macro-defined, semantics opaque (R4)
  FontFile = <userpath>/.fonts/stick/1CamBam_Stick_2.ttf
  MakeFace = true
  Placement = pos=(200,-2200,0) rot=(0,0,1;0rad)
  Source = -> Panel005
  TagPosition = (-51.2402,257.491,0)
  TagRotation = 0
  TagSize = 10
  TagText = %tag%
FEATURE [Part::FeaturePython] PanelView017  label="View of Side reinforcement 003"  # WARN: FeaturePython — macro-defined, semantics opaque (R4)
  FontFile = <userpath>/.fonts/stick/1CamBam_Stick_2.ttf
  MakeFace = true
  Placement = pos=(0,-2900,0) rot=(0,0,1;0rad)
  Source = -> Panel010
  TagPosition = (-155.534,260.627,0)
  TagRotation = 0
  TagSize = 10
  TagText = %tag%
FEATURE [Part::FeaturePython] PanelView018  label="View of Side reinforcement 005"  # WARN: FeaturePython — macro-defined, semantics opaque (R4)
  FontFile = <userpath>/.fonts/stick/1CamBam_Stick_2.ttf
  MakeFace = true
  Placement = pos=(-1500,-2000,0) rot=(0,0,1;0rad)
  Source = -> Panel013
  TagPosition = (-162.721,257.188,0)
  TagRotation = 0
  TagSize = 10
  TagText = %tag%
FEATURE [Part::FeaturePython] PanelView063  label="View of Side reinforcement 002"  # WARN: FeaturePython — macro-defined, semantics opaque (R4)
  FontFile = <userpath>/.fonts/stick/1CamBam_Stick_2.ttf
  MakeFace = false
  Placement = pos=(-100,-1700,0) rot=(0,0,1;0rad)
  Source = -> Panel008
  TagPosition = (0,300,0)
  TagRotation = 0
  TagSize = 10
  TagText = %tag%
FEATURE [Part::FeaturePython] PanelView064  label="View of Side reinforcement 004"  # WARN: FeaturePython — macro-defined, semantics opaque (R4)
  FontFile = <userpath>/.fonts/stick/1CamBam_Stick_2.ttf
  MakeFace = false
  Placement = pos=(-100,-2500,0) rot=(0,0,1;0rad)
  Source = -> Panel011
  TagPosition = (0,300,0)
  TagRotation = 0
  TagSize = 10
  TagText = %tag%
FEATURE [Part::FeaturePython] PanelView066  label="View of Side reinforcement 007"  # WARN: FeaturePython — macro-defined, semantics opaque (R4)
  FontFile = <userpath>/.fonts/stick/1CamBam_Stick_2.ttf
  MakeFace = false
  Placement = pos=(-200,-3100,0) rot=(0,0,1;0rad)
  Source = -> Panel018
  TagPosition = (100,300,0)
  TagRotation = 0
  TagSize = 10
  TagText = %tag%
FEATURE [Part::FeaturePython] PanelView070  label="View of Side reinforcement 009"  # WARN: FeaturePython — macro-defined, semantics opaque (R4)
  FontFile = <userpath>/.fonts/stick/1CamBam_Stick_2.ttf
  MakeFace = false
  Placement = pos=(-400,-3700,0) rot=(0,0,1;0rad)
  Source = -> Panel024
  TagPosition = (100,300,0)
  TagRotation = 0
  TagSize = 10
  TagText = %tag%
FEATURE [Part::FeaturePython] PanelView208  label="View of Side reinforcement 010"  # WARN: FeaturePython — macro-defined, semantics opaque (R4)
  FontFile = <userpath>/.fonts/stick/1CamBam_Stick_2.ttf
  MakeFace = false
  Placement = pos=(-2900,-2900,0) rot=(0,0,1;0rad)
  Source = -> Panel011
  TagPosition = (-238.108,254.381,0)
  TagRotation = 0
  TagSize = 10
  TagText = %tag%
FEATURE [Part::FeaturePython] PanelView210  label="View of Side reinforcement 011"  # WARN: FeaturePython — macro-defined, semantics opaque (R4)
  FontFile = <userpath>/.fonts/stick/1CamBam_Stick_2.ttf
  MakeFace = false
  Placement = pos=(-3000,-3800,0) rot=(0,0,1;0rad)
  Source = -> Panel008
  TagPosition = (-256.311,242.741,0)
  TagRotation = 0
  TagSize = 10
  TagText = %tag%
FEATURE [Part::FeaturePython] PanelView211  label="View of Side reinforcement 012"  # WARN: FeaturePython — macro-defined, semantics opaque (R4)
  FontFile = <userpath>/.fonts/stick/1CamBam_Stick_2.ttf
  MakeFace = false
  Placement = pos=(4700,2200,0) rot=(0,0,1;0rad)
  Source = -> Panel018
  TagPosition = (-254.599,250.654,0)
  TagRotation = 0
  TagSize = 10
  TagText = %tag%
FEATURE [Part::FeaturePython] PanelView215  label="View of Side reinforcement 013"  # WARN: FeaturePython — macro-defined, semantics opaque (R4)
  FontFile = <userpath>/.fonts/stick/1CamBam_Stick_2.ttf
  MakeFace = false
  Placement = pos=(6200,2100,0) rot=(0,0,1;0rad)
  Source = -> Panel024
  TagPosition = (-256.383,244.448,0)
  TagRotation = 0
  TagSize = 10
  TagText = %tag%
FEATURE [Part::FeaturePython] Clone084  label="Base hole018"  # Draft clone (typed FeaturePython)
  AttacherType = Attacher::AttachEngine3D
  Objects = -> [Clone083]
  Placement = pos=(656.999,1696.21,2557.8) rot=(-1,0,0;0.655693rad)
  Scale = (1,1,1)
FEATURE [Part::FeaturePython] Clone085  label="Base hole019"  # Draft clone (typed FeaturePython)
  AttacherType = Attacher::AttachEngine3D
  Objects = -> [Clone082]
  Placement = pos=(656.999,-745.069,4796.53) rot=(1,0,0;2.4859rad)
  Scale = (1,1,1)
FEATURE [Part::FeaturePython] Clone086  label="Base hole020"  # Draft clone (typed FeaturePython)
  AttacherType = Attacher::AttachEngine3D
  Objects = -> [Clone085]
  Placement = pos=(656.999,-982.856,4979.44) rot=(1,0,0;2.4859rad)
  Scale = (1,1,1)
FEATURE [Part::FeaturePython] Clone087  label="Base hole021"  # Draft clone (typed FeaturePython)
  AttacherType = Attacher::AttachEngine3D
  Objects = -> [Clone084]
  Placement = pos=(656.999,1458.43,2740.72) rot=(-1,0,0;0.655693rad)
  Scale = (1,1,1)
FEATURE [Part::FeaturePython] Clone088  label="Base hole022"  # Draft clone (typed FeaturePython)
  AttacherType = Attacher::AttachEngine3D
  Objects = -> [Clone087]
  Placement = pos=(656.999,919.462,4569.82) rot=(1,0,0;0.655676rad)
  Scale = (1,1,1)
FEATURE [Part::FeaturePython] Clone089  label="Base hole023"  # Draft clone (typed FeaturePython)
  AttacherType = Attacher::AttachEngine3D
  Objects = -> [Clone086]
  Placement = pos=(656.999,-1870.61,2784.52) rot=(1,0,0;3.79727rad)
  Scale = (1,1,1)
FEATURE [Part::FeaturePython] Clone090  label="Base hole024"  # Draft clone (typed FeaturePython)
  AttacherType = Attacher::AttachEngine3D
  Objects = -> [Clone089]
  Placement = pos=(656.999,-1632.82,2967.43) rot=(1,0,0;3.79727rad)
  Scale = (1,1,1)
FEATURE [Part::FeaturePython] Clone091  label="Base hole025"  # Draft clone (typed FeaturePython)
  AttacherType = Attacher::AttachEngine3D
  Objects = -> [Clone088]
  Placement = pos=(656.999,1157.25,4752.73) rot=(1,0,0;0.655676rad)
  Scale = (1,1,1)
FEATURE [Part::Compound] Compound001  label="top reinforcement profile"
  Links = -> [Wire021,Clone084,Clone088,Clone085,Clone086,Clone087,Clone089,Clone090,Clone091]
FEATURE [Part::FeaturePython] Panel004  label="Top reinforcement 001"  # WARN: FeaturePython — macro-defined, semantics opaque (R4)
  Area = 388969
  Base = -> Compound001
  Description = Top reinforcement piece
  FaceMaker = 0
  HorizontalArea = 0
  Length = 0
  MoveWithHost = false
  Normal = (1,0,0)
  PerimeterLength = 0
  Placement = pos=(-18,0,0) rot=(0,0,1;0rad)
  Role = 0
  Sheets = 1
  Tag = FRA-A/R4
  Thickness = 18
  VerticalArea = 0
  WaveDirection = 0
  WaveHeight = 0
  WaveLength = 0
  WaveType = 0
  Width = 0
FEATURE [Part::FeaturePython] Panel014  label="Top reinforcement 002"  # WARN: FeaturePython — macro-defined, semantics opaque (R4)
  Area = 388969
  CloneOf = -> Panel004
  Description = Top reinforcement piece
  FaceMaker = 0
  HorizontalArea = 0
  Length = 0
  MoveWithHost = false
  Normal = (0,0,0)
  PerimeterLength = 0
  Placement = pos=(-114,0,0) rot=(0,0,1;0rad)
  Role = 0
  Sheets = 1
  Tag = FRA-A/R4
  Thickness = 18
  VerticalArea = 0
  WaveDirection = 0
  WaveHeight = 0
  WaveLength = 0
  WaveType = 0
  Width = 0
FEATURE [Part::FeaturePython] Panel022  label="Top reinforcement 003"  # WARN: FeaturePython — macro-defined, semantics opaque (R4)
  Area = 388969
  CloneOf = -> Panel004
  Description = Top reinforcement piece
  FaceMaker = 0
  HorizontalArea = 0
  Length = 0
  MoveWithHost = false
  Normal = (0,0,0)
  PerimeterLength = 0
  Placement = pos=(-1218,0,0) rot=(0,0,1;0rad)
  Role = 0
  Sheets = 1
  Tag = FRA-A/R4
  Thickness = 18
  VerticalArea = 0
  WaveDirection = 0
  WaveHeight = 0
  WaveLength = 0
  WaveType = 0
  Width = 0
FEATURE [Part::FeaturePython] Panel023  label="Top reinforcement 004"  # WARN: FeaturePython — macro-defined, semantics opaque (R4)
  Area = 388969
  CloneOf = -> Panel004
  Description = Top reinforcement piece
  FaceMaker = 0
  HorizontalArea = 0
  Length = 0
  MoveWithHost = false
  Normal = (0,0,0)
  PerimeterLength = 0
  Placement = pos=(-1314,0,0) rot=(0,0,1;0rad)
  Role = 0
  Sheets = 1
  Tag = FRA-A/R4
  Thickness = 18
  VerticalArea = 0
  WaveDirection = 0
  WaveHeight = 0
  WaveLength = 0
  WaveType = 0
  Width = 0
FEATURE [Part::FeaturePython] PanelView013  label="View of Top reinforcement 001"  # WARN: FeaturePython — macro-defined, semantics opaque (R4)
  FontFile = <userpath>/.fonts/stick/1CamBam_Stick_2.ttf
  MakeFace = true
  Placement = pos=(4000,-800,0) rot=(0,0,1;0rad)
  Source = -> Panel004
  TagPosition = (-200,0,0)
  TagRotation = 0
  TagSize = 10
  TagText = %tag%
FEATURE [Part::FeaturePython] PanelView019  label="View of Top reinforcement 002"  # WARN: FeaturePython — macro-defined, semantics opaque (R4)
  FontFile = <userpath>/.fonts/stick/1CamBam_Stick_2.ttf
  MakeFace = true
  Placement = pos=(4200,-2400,0) rot=(0,0,1;0rad)
  Source = -> Panel014
  TagPosition = (-200,0,0)
  TagRotation = 0
  TagSize = 10
  TagText = %tag%
FEATURE [Part::FeaturePython] PanelView068  label="View of Top reinforcement 003"  # WARN: FeaturePython — macro-defined, semantics opaque (R4)
  FontFile = <userpath>/.fonts/stick/1CamBam_Stick_2.ttf
  MakeFace = false
  Placement = pos=(-1600,-1100,0) rot=(0,0,1;0rad)
  Source = -> Panel022
  TagPosition = (-200,0,0)
  TagRotation = 0
  TagSize = 10
  TagText = %tag%
FEATURE [Part::FeaturePython] PanelView069  label="View of Top reinforcement 004"  # WARN: FeaturePython — macro-defined, semantics opaque (R4)
  FontFile = <userpath>/.fonts/stick/1CamBam_Stick_2.ttf
  MakeFace = false
  Placement = pos=(-2400,-1000,0) rot=(0,0,1;0rad)
  Source = -> Panel023
  TagPosition = (-200,0,0)
  TagRotation = 0
  TagSize = 10
  TagText = %tag%
FEATURE [Part::FeaturePython] PanelView213  label="View of Top reinforcement 005"  # WARN: FeaturePython — macro-defined, semantics opaque (R4)
  FontFile = <userpath>/.fonts/stick/1CamBam_Stick_2.ttf
  MakeFace = false
  Placement = pos=(-3300,200,0) rot=(0,0,1;0rad)
  Source = -> Panel022
  TagPosition = (-200,0,0)
  TagRotation = 0
  TagSize = 10
  TagText = %tag%
FEATURE [Part::FeaturePython] PanelView214  label="View of Top reinforcement 006"  # WARN: FeaturePython — macro-defined, semantics opaque (R4)
  FontFile = <userpath>/.fonts/stick/1CamBam_Stick_2.ttf
  MakeFace = false
  Placement = pos=(-3300,-1400,0) rot=(0,0,1;0rad)
  Source = -> Panel023
  TagPosition = (-200,0,0)
  TagRotation = 0
  TagSize = 10
  TagText = %tag%
FEATURE [Part::Feature] Wire153  label="Wire226"
  shape: bbox 2.001e-07 x 893 x 893 mm, 0 faces, 0 solids (baked)
FEATURE [Part::Compound] Compound002  label="base reinforcement profile"
  Links = -> [Wire025,Clone067,Clone070,Clone069,Clone068,Clone072,Clone071,Clone074,Clone073,Clone075,DWire013,Wire153]
FEATURE [Part::FeaturePython] Panel006  label="Base reinforcement 001"  # WARN: FeaturePython — macro-defined, semantics opaque (R4)
  Area = 382232
  Base = -> Compound002
  Description = Base reinforcement piece
  FaceMaker = 0
  HorizontalArea = 0
  Length = 0
  MoveWithHost = false
  Normal = (1,0,0)
  PerimeterLength = 0
  Placement = pos=(-18,0,0) rot=(0,0,1;0rad)
  Role = 0
  Sheets = 1
  Tag = FRA-A/R1
  Thickness = 18
  VerticalArea = 0
  WaveDirection = 0
  WaveHeight = 0
  WaveLength = 0
  WaveType = 0
  Width = 0
FEATURE [Part::FeaturePython] Panel007  label="Base reinforcement 002"  # WARN: FeaturePython — macro-defined, semantics opaque (R4)
  Area = 382232
  CloneOf = -> Panel006
  Description = Base reinforcement piece
  FaceMaker = 0
  HorizontalArea = 0
  Length = 0
  MoveWithHost = false
  Normal = (0,0,0)
  PerimeterLength = 0
  Placement = pos=(18,0,0) rot=(0,0,1;3.14159rad)
  Role = 0
  Sheets = 1
  Tag = FRA-A/R1
  Thickness = 18
  VerticalArea = 0
  WaveDirection = 0
  WaveHeight = 0
  WaveLength = 0
  WaveType = 0
  Width = 0
FEATURE [Part::FeaturePython] Panel009  label="Base reinforcement 003"  # WARN: FeaturePython — macro-defined, semantics opaque (R4)
  Area = 382232
  CloneOf = -> Panel006
  Description = Base reinforcement piece
  FaceMaker = 0
  HorizontalArea = 0
  Length = 0
  MoveWithHost = false
  Normal = (0,0,0)
  PerimeterLength = 0
  Placement = pos=(1314,0,0) rot=(0,0,1;3.14159rad)
  Role = 0
  Sheets = 1
  Tag = FRA-A/R1
  Thickness = 18
  VerticalArea = 0
  WaveDirection = 0
  WaveHeight = 0
  WaveLength = 0
  WaveType = 0
  Width = 0
FEATURE [Part::FeaturePython] Panel012  label="Base reinforcement 004"  # WARN: FeaturePython — macro-defined, semantics opaque (R4)
  Area = 382232
  CloneOf = -> Panel006
  Description = Base reinforcement piece
  FaceMaker = 0
  HorizontalArea = 0
  Length = 0
  MoveWithHost = false
  Normal = (0,0,0)
  PerimeterLength = 0
  Placement = pos=(-1218,0,0) rot=(0,0,1;0rad)
  Role = 0
  Sheets = 1
  Tag = FRA-A/R1
  Thickness = 18
  VerticalArea = 0
  WaveDirection = 0
  WaveHeight = 0
  WaveLength = 0
  WaveType = 0
  Width = 0
FEATURE [Part::FeaturePython] Panel016  label="Base reinforcement 005"  # WARN: FeaturePython — macro-defined, semantics opaque (R4)
  Area = 382232
  CloneOf = -> Panel006
  Description = Base reinforcement piece
  FaceMaker = 0
  HorizontalArea = 0
  Length = 0
  MoveWithHost = false
  Normal = (0,0,0)
  PerimeterLength = 0
  Placement = pos=(1218,0,0) rot=(0,0,1;3.14159rad)
  Role = 0
  Sheets = 1
  Tag = FRA-A/R1
  Thickness = 18
  VerticalArea = 0
  WaveDirection = 0
  WaveHeight = 0
  WaveLength = 0
  WaveType = 0
  Width = 0
FEATURE [Part::FeaturePython] Panel017  label="Base reinforcement 006"  # WARN: FeaturePython — macro-defined, semantics opaque (R4)
  Area = 382232
  CloneOf = -> Panel006
  Description = Base reinforcement piece
  FaceMaker = 0
  HorizontalArea = 0
  Length = 0
  MoveWithHost = false
  Normal = (0,0,0)
  PerimeterLength = 0
  Placement = pos=(-114,0,0) rot=(0,0,1;0rad)
  Role = 0
  Sheets = 1
  Tag = FRA-A/R1
  Thickness = 18
  VerticalArea = 0
  WaveDirection = 0
  WaveHeight = 0
  WaveLength = 0
  WaveType = 0
  Width = 0
FEATURE [Part::FeaturePython] Panel019  label="Base reinforcement 007"  # WARN: FeaturePython — macro-defined, semantics opaque (R4)
  Area = 382232
  CloneOf = -> Panel006
  Description = Base reinforcement piece
  FaceMaker = 0
  HorizontalArea = 0
  Length = 0
  MoveWithHost = false
  Normal = (0,0,0)
  PerimeterLength = 0
  Placement = pos=(113.997,0,0) rot=(0,0,1;3.14159rad)
  Role = 0
  Sheets = 1
  Tag = FRA-A/R1
  Thickness = 18
  VerticalArea = 0
  WaveDirection = 0
  WaveHeight = 0
  WaveLength = 0
  WaveType = 0
  Width = 0
FEATURE [Part::FeaturePython] Panel025  label="Base reinforcement 009"  # WARN: FeaturePython — macro-defined, semantics opaque (R4)
  Area = 382232
  CloneOf = -> Panel006
  Description = Base reinforcement piece
  FaceMaker = 0
  HorizontalArea = 0
  Length = 0
  MoveWithHost = false
  Normal = (0,0,0)
  PerimeterLength = 0
  Placement = pos=(-1314,0,0) rot=(0,0,1;0rad)
  Role = 0
  Sheets = 1
  Tag = FRA-A/R1
  Thickness = 18
  VerticalArea = 0
  WaveDirection = 0
  WaveHeight = 0
  WaveLength = 0
  WaveType = 0
  Width = 0
FEATURE [App::DocumentObjectGroupPython] VisGroup001  label="level2 reinforcement (0 originals)"  # scripted group (container) (typed FeaturePython)
  Group = -> [Panel007,Panel008,Panel011,Panel012,Panel018,Panel019,Panel022,Panel023,Panel024,Panel025]
FEATURE [App::DocumentObjectGroupPython] VisGroup010  label="Endcap reinforcements (3 originals)"  # scripted group (container) (typed FeaturePython)
  Group = -> [Panel015,Panel014,Panel017,Panel016,Panel013,Panel005,Panel004,Panel006,Panel009,Panel010]
FEATURE [Part::FeaturePython] PanelView015  label="View of Base reinforcement 001"  # WARN: FeaturePython — macro-defined, semantics opaque (R4)
  FontFile = <userpath>/.fonts/stick/1CamBam_Stick_2.ttf
  MakeFace = true
  Placement = pos=(5300,-600,0) rot=(0,0,1;0rad)
  Source = -> Panel006
  TagPosition = (100,300,0)
  TagRotation = 0
  TagSize = 10
  TagText = %tag%
FEATURE [Part::FeaturePython] PanelView016  label="View of Base reinforcement 003"  # WARN: FeaturePython — macro-defined, semantics opaque (R4)
  FontFile = <userpath>/.fonts/stick/1CamBam_Stick_2.ttf
  MakeFace = true
  Placement = pos=(5500,-1800,0) rot=(0,0,1;0rad)
  Source = -> Panel009
  TagPosition = (100,300,0)
  TagRotation = 0
  TagSize = 10
  TagText = %tag%
FEATURE [Part::FeaturePython] PanelView020  label="View of Base reinforcement 005"  # WARN: FeaturePython — macro-defined, semantics opaque (R4)
  FontFile = <userpath>/.fonts/stick/1CamBam_Stick_2.ttf
  MakeFace = true
  Placement = pos=(5500,-3100,0) rot=(0,0,1;0rad)
  Source = -> Panel016
  TagPosition = (100,300,0)
  TagRotation = 0
  TagSize = 10
  TagText = %tag%
FEATURE [Part::FeaturePython] PanelView021  label="View of Base reinforcement 006"  # WARN: FeaturePython — macro-defined, semantics opaque (R4)
  FontFile = <userpath>/.fonts/stick/1CamBam_Stick_2.ttf
  MakeFace = true
  Placement = pos=(4200,-3900,0) rot=(0,0,1;0rad)
  Source = -> Panel017
  TagPosition = (100,300,0)
  TagRotation = 0
  TagSize = 10
  TagText = %tag%
FEATURE [Part::FeaturePython] PanelView062  label="View of Base reinforcement 002"  # WARN: FeaturePython — macro-defined, semantics opaque (R4)
  FontFile = <userpath>/.fonts/stick/1CamBam_Stick_2.ttf
  MakeFace = false
  Placement = pos=(-3300,-2800,0) rot=(0,0,1;0rad)
  Source = -> Panel007
  TagPosition = (100,300.079,-19.8339)
  TagRotation = 0
  TagSize = 10
  TagText = %tag%
FEATURE [Part::FeaturePython] PanelView065  label="View of Base reinforcement 004"  # WARN: FeaturePython — macro-defined, semantics opaque (R4)
  FontFile = <userpath>/.fonts/stick/1CamBam_Stick_2.ttf
  MakeFace = false
  Placement = pos=(-4400,-2700,0) rot=(0,0,1;0rad)
  Source = -> Panel012
  TagPosition = (100,300.075,-19.0405)
  TagRotation = 0
  TagSize = 10
  TagText = %tag%
FEATURE [Part::FeaturePython] PanelView067  label="View of Base reinforcement 007"  # WARN: FeaturePython — macro-defined, semantics opaque (R4)
  FontFile = <userpath>/.fonts/stick/1CamBam_Stick_2.ttf
  MakeFace = false
  Placement = pos=(-3300,-3800,0) rot=(0,0,1;0rad)
  Source = -> Panel019
  TagPosition = (100,301.426,-99.8999)
  TagRotation = 0
  TagSize = 10
  TagText = %tag%
FEATURE [Part::FeaturePython] PanelView071  label="View of Base reinforcement 009"  # WARN: FeaturePython — macro-defined, semantics opaque (R4)
  FontFile = <userpath>/.fonts/stick/1CamBam_Stick_2.ttf
  MakeFace = false
  Placement = pos=(-4500,-3799.88,-30.1475) rot=(0,0,1;0rad)
  Source = -> Panel025
  TagPosition = (100,299.991,2.38006)
  TagRotation = 0
  TagSize = 10
  TagText = %tag%
FEATURE [Part::FeaturePython] PanelView207  label="View of Base reinforcement 010"  # WARN: FeaturePython — macro-defined, semantics opaque (R4)
  FontFile = <userpath>/.fonts/stick/1CamBam_Stick_2.ttf
  MakeFace = false
  Placement = pos=(-1000,2100,0) rot=(0,0,1;0rad)
  Source = -> Panel007
  TagPosition = (100,300,0)
  TagRotation = 0
  TagSize = 10
  TagText = %tag%
FEATURE [Part::FeaturePython] PanelView209  label="View of Base reinforcement 011"  # WARN: FeaturePython — macro-defined, semantics opaque (R4)
  FontFile = <userpath>/.fonts/stick/1CamBam_Stick_2.ttf
  MakeFace = false
  Placement = pos=(400,2200,0) rot=(0,0,1;0rad)
  Source = -> Panel012
  TagPosition = (100,300,0)
  TagRotation = 0
  TagSize = 10
  TagText = %tag%
FEATURE [Part::FeaturePython] PanelView212  label="View of Base reinforcement 012"  # WARN: FeaturePython — macro-defined, semantics opaque (R4)
  FontFile = <userpath>/.fonts/stick/1CamBam_Stick_2.ttf
  MakeFace = false
  Placement = pos=(1600,2300,0) rot=(0,0,1;0rad)
  Source = -> Panel019
  TagPosition = (100,300,0)
  TagRotation = 0
  TagSize = 10
  TagText = %tag%
FEATURE [Part::FeaturePython] PanelView216  label="View of Base reinforcement 013"  # WARN: FeaturePython — macro-defined, semantics opaque (R4)
  FontFile = <userpath>/.fonts/stick/1CamBam_Stick_2.ttf
  MakeFace = false
  Placement = pos=(2900,2500,0) rot=(0,0,1;0rad)
  Source = -> Panel025
  TagPosition = (100,300,0)
  TagRotation = 0
  TagSize = 10
  TagText = %tag%
FEATURE [Part::Part2DObjectPython] DWire  # Draft 2D object (typed FeaturePython)
  ChamferSize = 0
  Closed = true
  End = (-514.997,-2093,2409)
  FilletRadius = 0
  Length = 4574.99
  MakeFace = true
  Points = (74) [(-514.997,-2093,2404),(-385.001,-2093,2404),(-385.001,-2093,2409),(-374.999,-2093,2409),(-374.999,-2093,2386),(-224.999,-2093,2386),+68 more]
  Start = (-514.997,-2093,2404)
  Subdivisions = 0
FEATURE [Part::Cut] Cut
  Base = -> DWire
  Tool = -> Face002
FEATURE [Part::FeaturePython] Panel148  label="Top exterior"  # WARN: FeaturePython — macro-defined, semantics opaque (R4)
  Area = 278507
  Base = -> Cut
  FaceMaker = 0
  HorizontalArea = 0
  Length = 0
  MoveWithHost = false
  Normal = (0,1,0)
  PerimeterLength = 0
  Role = 0
  Sheets = 1
  Tag = W5
  Thickness = 18
  VerticalArea = 0
  WaveDirection = 0
  WaveHeight = 0
  WaveLength = 0
  WaveType = 0
  Width = 0
FEATURE [Part::FeaturePython] PanelView139  label="View of Top exterior"  # WARN: FeaturePython — macro-defined, semantics opaque (R4)
  FontFile = <userpath>/.fonts/stick/1CamBam_Stick_2.ttf
  MakeFace = false
  Placement = pos=(-3800,-5000,0) rot=(0,0,1;0rad)
  Source = -> Panel148
  TagPosition = (-4.57812,-214.335,0)
  TagRotation = 0
  TagSize = 10
  TagText = %tag%
FEATURE [Part::Part2DObjectPython] DWire014  # Draft 2D object (typed FeaturePython)
  ChamferSize = 0
  Closed = true
  End = (-524.999,-2093,1733)
  FilletRadius = 0
  Length = 11761.9
  MakeFace = true
  Points = (186) [(-524.999,-2093,1853),(-565.999,-2093,1853),(-565.999,-2093,1863),(-561,-2093,1863),(-561,-2093,2023),(-565.999,-2093,2023),(-565.999,-2093,2033),+179 more]
  Start = (-524.999,-2093,1853)
  Subdivisions = 0
FEATURE [Part::Cut] Cut001
  Base = -> DWire014
  Tool = -> Face004
FEATURE [Part::Cut] Cut002
  Base = -> Cut001
  Tool = -> Face005
FEATURE [Part::Part2DObjectPython] DWire015  # Draft 2D object (typed FeaturePython)
  ChamferSize = 0
  Closed = true
  End = (234.998,-2075,2386)
  FilletRadius = 0
  Length = 3008
  MakeFace = true
  Points = (52) [(234.998,-2070,2386),(224.997,-2070,2386),(224.997,-2093,2386),(74.9976,-2093,2386),(74.9976,-2070,2386),(65.0005,-2070,2386),(65.0005,-2075,2386),+45 more]
  Start = (234.998,-2070,2386)
  Subdivisions = 0
FEATURE [Part::FeaturePython] Panel146  label="Top inner"  # WARN: FeaturePython — macro-defined, semantics opaque (R4)
  Area = 283499
  Base = -> DWire015
  FaceMaker = 0
  HorizontalArea = 0
  Length = 0
  MoveWithHost = false
  Normal = (0,0,1)
  PerimeterLength = 0
  Role = 0
  Sheets = 1
  Tag = W4
  Thickness = 18
  VerticalArea = 0
  WaveDirection = 0
  WaveHeight = 0
  WaveLength = 0
  WaveType = 0
  Width = 0
FEATURE [Part::FeaturePython] PanelView138  label="View of Top inner"  # WARN: FeaturePython — macro-defined, semantics opaque (R4)
  FontFile = <userpath>/.fonts/stick/1CamBam_Stick_2.ttf
  MakeFace = false
  Placement = pos=(-5700,-2800,0) rot=(0,0,1;0rad)
  Source = -> Panel146
  TagPosition = (0,0,0)
  TagRotation = 0
  TagSize = 10
  TagText = %tag%
FEATURE [Part::Part2DObjectPython] DWire016  # Draft 2D object (typed FeaturePython)
  ChamferSize = 0
  Closed = true
  End = (514.997,-1807,2404)
  FilletRadius = 0
  Length = 12597.1
  MakeFace = true
  Points = (182) [(384.997,-1807,2404),(384.997,-1807,2409),(375,-1807,2409),(375,-1807,2386),(224.997,-1807,2386),(224.997,-1807,2409),(215,-1807,2409),+175 more]
  Start = (384.997,-1807,2404)
  Subdivisions = 0
FEATURE [Part::FeaturePython] Panel150  label="Wall inner"  # WARN: FeaturePython — macro-defined, semantics opaque (R4)
  Area = 332389
  Base = -> DWire016
  FaceMaker = 0
  HorizontalArea = 0
  Length = 0
  MoveWithHost = false
  Normal = (0,-1,0)
  PerimeterLength = 0
  Role = 0
  Sheets = 1
  Tag = W3
  Thickness = 18
  VerticalArea = 0
  WaveDirection = 0
  WaveHeight = 0
  WaveLength = 0
  WaveType = 0
  Width = 0
FEATURE [Part::FeaturePython] PanelView142  label="View of Wall inner"  # WARN: FeaturePython — macro-defined, semantics opaque (R4)
  FontFile = <userpath>/.fonts/stick/1CamBam_Stick_2.ttf
  MakeFace = false
  Placement = pos=(3100,100,0) rot=(0,0,1;0rad)
  Source = -> Panel150
  TagPosition = (-16.1069,1046.48,0)
  TagRotation = 0
  TagSize = 10
  TagText = %tag%
FEATURE [Part::FeaturePython] Clone092  label="Face007"  # Draft clone (typed FeaturePython)
  AttacherType = Attacher::AttachEngine3D
  Objects = -> [Face005]
  Placement = pos=(-0.000976558,0,286) rot=(0,1,0;3.14159rad)
  Scale = (1,1,1)
FEATURE [Part::Cut] Cut003
  Base = -> Cut002
  Tool = -> Clone092
FEATURE [Part::FeaturePython] Panel149  label="Bottom exterior"  # WARN: FeaturePython — macro-defined, semantics opaque (R4)
  Area = 504563
  Base = -> Cut003
  FaceMaker = 0
  HorizontalArea = 0
  Length = 0
  MoveWithHost = false
  Normal = (0,1,0)
  PerimeterLength = 0
  Role = 0
  Sheets = 1
  Tag = W2
  Thickness = 18
  VerticalArea = 0
  WaveDirection = 0
  WaveHeight = 0
  WaveLength = 0
  WaveType = 0
  Width = 0
FEATURE [App::DocumentObjectGroupPython] VisGroup007  label="level 8 window (5 originals)"  # scripted group (container) (typed FeaturePython)
  Group = -> [Panel146,Panel147,Panel148,Panel149,Panel150]
FEATURE [App::DocumentObjectGroup] Group006  label="Window - 5 peças ( + 86da Base)"
  Group = -> [VisGroup007]
FEATURE [Part::FeaturePython] PanelView141  label="View of Bottom exterior"  # WARN: FeaturePython — macro-defined, semantics opaque (R4)
  FontFile = <userpath>/.fonts/stick/1CamBam_Stick_2.ttf
  MakeFace = false
  Placement = pos=(1700,0,0) rot=(0,0,1;0rad)
  Source = -> Panel149
  TagPosition = (-3.5343,856.594,0)
  TagRotation = 0
  TagSize = 10
  TagText = %tag%
FEATURE [Part::Feature] Wire156  label="Wire227"
  shape: bbox 150 x 2.019e-07 x 1918 mm, 0 faces, 0 solids (baked)
FEATURE [Part::FeaturePython] Panel110  label="Struct outer side large 001"  # WARN: FeaturePython — macro-defined, semantics opaque (R4)
  Area = 197098
  Base = -> Wire156
  Description = struct side
  FaceMaker = 0
  HorizontalArea = 0
  Length = 0
  MoveWithHost = false
  Normal = (0,1,0)
  PerimeterLength = 0
  Placement = pos=(0,-18,0) rot=(0,0,1;0rad)
  Role = 0
  Sheets = 1
  Tag = FRA-A/S4/EX
  Thickness = 18
  VerticalArea = 0
  WaveDirection = 0
  WaveHeight = 0
  WaveLength = 0
  WaveType = 0
  Width = 0
FEATURE [Part::FeaturePython] Panel128  label="Struct outer side large 002"  # WARN: FeaturePython — macro-defined, semantics opaque (R4)
  Area = 197098
  CloneOf = -> Panel110
  Description = struct side
  FaceMaker = 0
  HorizontalArea = 0
  Length = 0
  MoveWithHost = false
  Normal = (0,0,0)
  PerimeterLength = 0
  Placement = pos=(0,4113.99,0) rot=(0,0,1;0rad)
  Role = 0
  Sheets = 1
  Tag = FRA-A/S4/EX
  Thickness = 18
  VerticalArea = 0
  WaveDirection = 0
  WaveHeight = 0
  WaveLength = 0
  WaveType = 0
  Width = 0
FEATURE [Part::FeaturePython] Panel130  label="Struct outer side large 003"  # WARN: FeaturePython — macro-defined, semantics opaque (R4)
  Area = 197098
  CloneOf = -> Panel110
  Description = struct side
  FaceMaker = 0
  HorizontalArea = 0
  Length = 0
  MoveWithHost = false
  Normal = (0,0,0)
  PerimeterLength = 0
  Placement = pos=(-1200,4113.99,0) rot=(0,0,1;0rad)
  Role = 0
  Sheets = 1
  Tag = FRA-A/S4/EX
  Thickness = 18
  VerticalArea = 0
  WaveDirection = 0
  WaveHeight = 0
  WaveLength = 0
  WaveType = 0
  Width = 0
FEATURE [Part::FeaturePython] Panel132  label="Struct outer side large 004"  # WARN: FeaturePython — macro-defined, semantics opaque (R4)
  Area = 197098
  CloneOf = -> Panel110
  Description = struct side
  FaceMaker = 0
  HorizontalArea = 0
  Length = 0
  MoveWithHost = false
  Normal = (0,0,0)
  PerimeterLength = 0
  Placement = pos=(-1200,-18,0) rot=(0,0,1;0rad)
  Role = 0
  Sheets = 1
  Tag = FRA-A/S4/EX
  Thickness = 18
  VerticalArea = 0
  WaveDirection = 0
  WaveHeight = 0
  WaveLength = 0
  WaveType = 0
  Width = 0
FEATURE [Part::FeaturePython] PanelView033  label="View of Struct outer side large 001"  # WARN: FeaturePython — macro-defined, semantics opaque (R4)
  FontFile = <userpath>/.fonts/stick/1CamBam_Stick_2.ttf
  MakeFace = true
  Placement = pos=(-600,0,0) rot=(0,0,1;0rad)
  Source = -> Panel110
  TagPosition = (0,0,0)
  TagRotation = 90
  TagSize = 10
  TagText = %tag%
FEATURE [Part::FeaturePython] PanelView047  label="View of Struct outer side large 002"  # WARN: FeaturePython — macro-defined, semantics opaque (R4)
  FontFile = <userpath>/.fonts/stick/1CamBam_Stick_2.ttf
  MakeFace = true
  Placement = pos=(-4300,0,0) rot=(0,0,1;0rad)
  Source = -> Panel128
  TagPosition = (0,0,0)
  TagRotation = 90
  TagSize = 10
  TagText = %tag%
FEATURE [Part::FeaturePython] PanelView087  label="View of Struct outer side large 003"  # WARN: FeaturePython — macro-defined, semantics opaque (R4)
  FontFile = <userpath>/.fonts/stick/1CamBam_Stick_2.ttf
  MakeFace = false
  Placement = pos=(-600,99.9593,2.85428) rot=(0,0,1;0rad)
  Source = -> Panel130
  TagPosition = (0,0,0)
  TagRotation = 90
  TagSize = 10
  TagText = %tag%
FEATURE [Part::FeaturePython] PanelView089  label="View of Struct outer side large 004"  # WARN: FeaturePython — macro-defined, semantics opaque (R4)
  FontFile = <userpath>/.fonts/stick/1CamBam_Stick_2.ttf
  MakeFace = false
  Placement = pos=(-5500,599.756,17.1257) rot=(0,0,1;0rad)
  Source = -> Panel132
  TagPosition = (0,0,0)
  TagRotation = 90
  TagSize = 10
  TagText = %tag%
FEATURE [Part::FeaturePython] PanelView181  label="View of Struct outer side large 005"  # WARN: FeaturePython — macro-defined, semantics opaque (R4)
  FontFile = <userpath>/.fonts/stick/1CamBam_Stick_2.ttf
  MakeFace = false
  Placement = pos=(13200,-100,0) rot=(0,0,1;0rad)
  Source = -> Panel132
  TagPosition = (0,0,0)
  TagRotation = 90
  TagSize = 10
  TagText = %tag%
FEATURE [Part::FeaturePython] PanelView194  label="View of Struct outer side large 006"  # WARN: FeaturePython — macro-defined, semantics opaque (R4)
  FontFile = <userpath>/.fonts/stick/1CamBam_Stick_2.ttf
  MakeFace = false
  Placement = pos=(13500,-200,0) rot=(0,0,1;0rad)
  Source = -> Panel130
  TagPosition = (0,0,0)
  TagRotation = 90
  TagSize = 10
  TagText = %tag%
FEATURE [Part::Feature] Wire159  label="Wire230"
  shape: bbox 150 x 2.031e-07 x 1931 mm, 0 faces, 0 solids (baked)
FEATURE [Part::FeaturePython] Panel112  label="struct inner side large 001"  # WARN: FeaturePython — macro-defined, semantics opaque (R4)
  Area = 194049
  Base = -> Wire159
  Description = struct side
  FaceMaker = 0
  HorizontalArea = 0
  Length = 0
  MoveWithHost = false
  Normal = (0,1,0)
  PerimeterLength = 0
  Placement = pos=(0,-18,0) rot=(0,0,1;0rad)
  Role = 0
  Sheets = 1
  Tag = FRA-A/S3/IN
  Thickness = 18
  VerticalArea = 0
  WaveDirection = 0
  WaveHeight = 0
  WaveLength = 0
  WaveType = 0
  Width = 0
FEATURE [Part::FeaturePython] Panel121  label="struct inner side large 002"  # WARN: FeaturePython — macro-defined, semantics opaque (R4)
  Area = 194049
  CloneOf = -> Panel112
  Description = struct side
  FaceMaker = 0
  HorizontalArea = 0
  Length = 0
  MoveWithHost = false
  Normal = (0,0,0)
  PerimeterLength = 0
  Placement = pos=(0,3649.99,0) rot=(0,0,1;0rad)
  Role = 0
  Sheets = 1
  Tag = FRA-A/S3/IN
  Thickness = 18
  VerticalArea = 0
  WaveDirection = 0
  WaveHeight = 0
  WaveLength = 0
  WaveType = 0
  Width = 0
FEATURE [Part::FeaturePython] Panel124  label="struct inner side large 003"  # WARN: FeaturePython — macro-defined, semantics opaque (R4)
  Area = 194049
  CloneOf = -> Panel112
  Description = struct side
  FaceMaker = 0
  HorizontalArea = 0
  Length = 0
  MoveWithHost = false
  Normal = (0,0,0)
  PerimeterLength = 0
  Placement = pos=(-1200,-18,0) rot=(0,0,1;0rad)
  Role = 0
  Sheets = 1
  Tag = FRA-A/S3/IN
  Thickness = 18
  VerticalArea = 0
  WaveDirection = 0
  WaveHeight = 0
  WaveLength = 0
  WaveType = 0
  Width = 0
FEATURE [Part::FeaturePython] Panel126  label="struct inner side large 004"  # WARN: FeaturePython — macro-defined, semantics opaque (R4)
  Area = 194049
  CloneOf = -> Panel112
  Description = struct side
  FaceMaker = 0
  HorizontalArea = 0
  Length = 0
  MoveWithHost = false
  Normal = (0,0,0)
  PerimeterLength = 0
  Placement = pos=(-1200,3649.99,0) rot=(0,0,1;0rad)
  Role = 0
  Sheets = 1
  Tag = FRA-A/S3/IN
  Thickness = 18
  VerticalArea = 0
  WaveDirection = 0
  WaveHeight = 0
  WaveLength = 0
  WaveType = 0
  Width = 0
FEATURE [Part::FeaturePython] PanelView035  label="View of struct inner side large 001"  # WARN: FeaturePython — macro-defined, semantics opaque (R4)
  FontFile = <userpath>/.fonts/stick/1CamBam_Stick_2.ttf
  MakeFace = true
  Placement = pos=(300,0,0) rot=(0,0,1;0rad)
  Source = -> Panel112
  TagPosition = (0,0,0)
  TagRotation = 90
  TagSize = 10
  TagText = %tag%
FEATURE [Part::FeaturePython] PanelView044  label="View of struct inner side large 002"  # WARN: FeaturePython — macro-defined, semantics opaque (R4)
  FontFile = <userpath>/.fonts/stick/1CamBam_Stick_2.ttf
  MakeFace = true
  Placement = pos=(600,0,0) rot=(0,0,1;0rad)
  Source = -> Panel121
  TagPosition = (0,0,0)
  TagRotation = 90
  TagSize = 10
  TagText = %tag%
FEATURE [Part::FeaturePython] PanelView083  label="View of struct inner side large 003"  # WARN: FeaturePython — macro-defined, semantics opaque (R4)
  FontFile = <userpath>/.fonts/stick/1CamBam_Stick_2.ttf
  MakeFace = false
  Placement = pos=(-6700,799.674,22.8343) rot=(0,0,1;0rad)
  Source = -> Panel124
  TagPosition = (0,0,0)
  TagRotation = 90
  TagSize = 10
  TagText = %tag%
FEATURE [Part::FeaturePython] PanelView085  label="View of struct inner side large 004"  # WARN: FeaturePython — macro-defined, semantics opaque (R4)
  FontFile = <userpath>/.fonts/stick/1CamBam_Stick_2.ttf
  MakeFace = false
  Placement = pos=(-7500,899.633,25.6885) rot=(0,0,1;0rad)
  Source = -> Panel126
  TagPosition = (0,0,0)
  TagRotation = 90
  TagSize = 10
  TagText = %tag%
FEATURE [Part::FeaturePython] PanelView184  label="View of struct inner side large 005"  # WARN: FeaturePython — macro-defined, semantics opaque (R4)
  FontFile = <userpath>/.fonts/stick/1CamBam_Stick_2.ttf
  MakeFace = false
  Placement = pos=(12400,0,0) rot=(0,0,1;0rad)
  Source = -> Panel126
  TagPosition = (0,0,0)
  TagRotation = 90
  TagSize = 10
  TagText = %tag%
FEATURE [Part::FeaturePython] PanelView199  label="View of struct inner side large 006"  # WARN: FeaturePython — macro-defined, semantics opaque (R4)
  FontFile = <userpath>/.fonts/stick/1CamBam_Stick_2.ttf
  MakeFace = false
  Placement = pos=(12800,-300,0) rot=(0,0,1;0rad)
  Source = -> Panel124
  TagPosition = (0,0,0)
  TagRotation = 90
  TagSize = 10
  TagText = %tag%
FEATURE [Part::Part2DObjectPython] DWire017  # Draft 2D object (typed FeaturePython)
  ChamferSize = 0
  Closed = true
  End = (560.999,1200,18)
  FilletRadius = 0
  Length = 5994.22
  MakeFace = false
  Points = (216) [(542.999,1200,18),(542.999,1090,18),(547.999,1090,18),(547.999,1080,18),(527.999,1080,18),(524.999,1077,18),(524.999,1023,18),(527.999,1020,18),+208 more]
  Start = (542.999,1200,18)
  Subdivisions = 0
FEATURE [Part::FeaturePython] Panel116  label="Struct outer bottom large 001"  # WARN: FeaturePython — macro-defined, semantics opaque (R4)
  Area = 252164
  Base = -> DWire017
  Description = struct bottom
  FaceMaker = 0
  HorizontalArea = 0
  Length = 0
  MoveWithHost = false
  Normal = (0,0,1)
  PerimeterLength = 0
  Role = 0
  Sheets = 1
  Tag = FRA/S1/EX
  Thickness = 18
  VerticalArea = 0
  WaveDirection = 0
  WaveHeight = 0
  WaveLength = 0
  WaveType = 0
  Width = 0
FEATURE [Part::FeaturePython] Panel135  label="Struct outer bottom large 002"  # WARN: FeaturePython — macro-defined, semantics opaque (R4)
  Area = 252164
  CloneOf = -> Panel116
  Description = struct bottom
  FaceMaker = 0
  HorizontalArea = 0
  Length = 0
  MoveWithHost = false
  Normal = (0,0,0)
  PerimeterLength = 0
  Placement = pos=(-1200,0,0) rot=(0,0,1;0rad)
  Role = 0
  Sheets = 1
  Tag = FRA/S1/EX
  Thickness = 18
  VerticalArea = 0
  WaveDirection = 0
  WaveHeight = 0
  WaveLength = 0
  WaveType = 0
  Width = 0
FEATURE [Part::FeaturePython] PanelView039  label="View of Struct outer bottom large 001"  # WARN: FeaturePython — macro-defined, semantics opaque (R4)
  FontFile = <userpath>/.fonts/stick/1CamBam_Stick_2.ttf
  MakeFace = true
  Placement = pos=(2600,700,0) rot=(0,0,1;0rad)
  Source = -> Panel116
  TagPosition = (0,0,0)
  TagRotation = 90
  TagSize = 10
  TagText = %tag%
FEATURE [Part::FeaturePython] PanelView092  label="View of Struct outer bottom large 002"  # WARN: FeaturePython — macro-defined, semantics opaque (R4)
  FontFile = <userpath>/.fonts/stick/1CamBam_Stick_2.ttf
  MakeFace = false
  Placement = pos=(800,-99.9593,-2.85428) rot=(0,0,1;0rad)
  Source = -> Panel135
  TagPosition = (0,0,0)
  TagRotation = 90
  TagSize = 10
  TagText = %tag%
FEATURE [Part::FeaturePython] PanelView196  label="View of Struct outer bottom large 003"  # WARN: FeaturePython — macro-defined, semantics opaque (R4)
  FontFile = <userpath>/.fonts/stick/1CamBam_Stick_2.ttf
  MakeFace = false
  Placement = pos=(11700,-200,0) rot=(0,0,1;0rad)
  Source = -> Panel135
  TagPosition = (0,0,0)
  TagRotation = 90
  TagSize = 10
  TagText = %tag%
FEATURE [Part::Part2DObjectPython] DWire018  # Draft 2D object (typed FeaturePython)
  ChamferSize = 0
  Closed = true
  End = (634.001,1200,249.999)
  FilletRadius = 0
  Length = 5316.25
  MakeFace = false
  Points = (196) [(639.001,1200,249.999),(656.999,1200,249.999),(656.999,1090,249.999),(651.999,1090,249.999),(651.999,1080,249.999),(671.999,1080,249.999),+190 more]
  Start = (639.001,1200,249.999)
  Subdivisions = 0
FEATURE [Part::FeaturePython] Panel115  label="Struct inner bottom large 001"  # WARN: FeaturePython — macro-defined, semantics opaque (R4)
  Area = 217075
  Base = -> DWire018
  Description = struct bottom
  FaceMaker = 0
  HorizontalArea = 0
  Length = 0
  MoveWithHost = false
  Normal = (0,0,1)
  PerimeterLength = 0
  Role = 0
  Sheets = 1
  Tag = FRA/S1/IN
  Thickness = 18
  VerticalArea = 0
  WaveDirection = 0
  WaveHeight = 0
  WaveLength = 0
  WaveType = 0
  Width = 0
FEATURE [Part::FeaturePython] Panel134  label="Struct inner bottom large 002"  # WARN: FeaturePython — macro-defined, semantics opaque (R4)
  Area = 217075
  CloneOf = -> Panel115
  Description = struct bottom
  FaceMaker = 0
  HorizontalArea = 0
  Length = 0
  MoveWithHost = false
  Normal = (0,0,0)
  PerimeterLength = 0
  Placement = pos=(-1200,0,0) rot=(0,0,1;0rad)
  Role = 0
  Sheets = 1
  Tag = FRA/S1/IN
  Thickness = 18
  VerticalArea = 0
  WaveDirection = 0
  WaveHeight = 0
  WaveLength = 0
  WaveType = 0
  Width = 0
FEATURE [Part::FeaturePython] PanelView038  label="View of Struct inner bottom large 001"  # WARN: FeaturePython — macro-defined, semantics opaque (R4)
  FontFile = <userpath>/.fonts/stick/1CamBam_Stick_2.ttf
  MakeFace = true
  Placement = pos=(-300,0,0) rot=(0,0,1;0rad)
  Source = -> Panel115
  TagPosition = (0,0,0)
  TagRotation = 90
  TagSize = 10
  TagText = %tag%
FEATURE [Part::FeaturePython] PanelView091  label="View of Struct inner bottom large 002"  # WARN: FeaturePython — macro-defined, semantics opaque (R4)
  FontFile = <userpath>/.fonts/stick/1CamBam_Stick_2.ttf
  MakeFace = false
  Placement = pos=(251.8,-42.2764,0) rot=(0,0,1;0rad)
  Source = -> Panel134
  TagPosition = (0,0,0)
  TagRotation = 90
  TagSize = 10
  TagText = %tag%
FEATURE [Part::FeaturePython] PanelView203  label="View of Struct inner bottom large 003"  # WARN: FeaturePython — macro-defined, semantics opaque (R4)
  FontFile = <userpath>/.fonts/stick/1CamBam_Stick_2.ttf
  MakeFace = false
  Placement = pos=(12100,-100,0) rot=(0,0,1;0rad)
  Source = -> Panel134
  TagPosition = (0,0,0)
  TagRotation = 90
  TagSize = 10
  TagText = %tag%
FEATURE [Part::Part2DObjectPython] DWire019  # Draft 2D object (typed FeaturePython)
  ChamferSize = 0
  Closed = true
  End = (634.001,-1200,249.999)
  FilletRadius = 0
  Length = 4610.28
  MakeFace = false
  Points = (174) [(634.001,-1210,249.999),(639.001,-1210,249.999),(638.999,-1310,249.999),(633.999,-1310,249.999),(633.999,-1320,249.999),(671.999,-1320,249.999),+168 more]
  Start = (634.001,-1210,249.999)
  Subdivisions = 0
FEATURE [Part::FeaturePython] Panel114  label="Struct inner bottom small 001"  # WARN: FeaturePython — macro-defined, semantics opaque (R4)
  Area = 179635
  Base = -> DWire019
  Description = struct bottom
  FaceMaker = 0
  HorizontalArea = 0
  Length = 0
  MoveWithHost = false
  Normal = (0,0,1)
  PerimeterLength = 0
  Role = 0
  Sheets = 1
  Tag = FRA-A/S2/IN
  Thickness = 18
  VerticalArea = 0
  WaveDirection = 0
  WaveHeight = 0
  WaveLength = 0
  WaveType = 0
  Width = 0
FEATURE [Part::FeaturePython] Panel133  label="Struct inner bottom small 002"  # WARN: FeaturePython — macro-defined, semantics opaque (R4)
  Area = 179635
  CloneOf = -> Panel114
  Description = struct bottom
  FaceMaker = 0
  HorizontalArea = 0
  Length = 0
  MoveWithHost = false
  Normal = (0,0,0)
  PerimeterLength = 0
  Placement = pos=(-1200,0,0) rot=(0,0,1;0rad)
  Role = 0
  Sheets = 1
  Tag = FRA-A/S2/IN
  Thickness = 18
  VerticalArea = 0
  WaveDirection = 0
  WaveHeight = 0
  WaveLength = 0
  WaveType = 0
  Width = 0
FEATURE [Part::FeaturePython] PanelView037  label="View of Struct inner bottom small 001"  # WARN: FeaturePython — macro-defined, semantics opaque (R4)
  FontFile = <userpath>/.fonts/stick/1CamBam_Stick_2.ttf
  MakeFace = true
  Placement = pos=(-3900,100,0) rot=(0,0,1;0rad)
  Source = -> Panel114
  TagPosition = (0,0,0)
  TagRotation = 90
  TagSize = 10
  TagText = %tag%
FEATURE [Part::FeaturePython] PanelView090  label="View of Struct inner bottom small 002"  # WARN: FeaturePython — macro-defined, semantics opaque (R4)
  FontFile = <userpath>/.fonts/stick/1CamBam_Stick_2.ttf
  MakeFace = false
  Placement = pos=(-7100,799.674,22.8343) rot=(0,0,1;0rad)
  Source = -> Panel133
  TagPosition = (0,0,0)
  TagRotation = 90
  TagSize = 10
  TagText = %tag%
FEATURE [Part::FeaturePython] PanelView186  label="View of Struct inner bottom small 003"  # WARN: FeaturePython — macro-defined, semantics opaque (R4)
  FontFile = <userpath>/.fonts/stick/1CamBam_Stick_2.ttf
  MakeFace = false
  Placement = pos=(11200,-2400,0) rot=(0,0,1;0rad)
  Source = -> Panel133
  TagPosition = (0,0,0)
  TagRotation = 90
  TagSize = 10
  TagText = %tag%
FEATURE [Part::Part2DObjectPython] DWire020  # Draft 2D object (typed FeaturePython)
  ChamferSize = 0
  Closed = true
  End = (639.001,-1210,18)
  FilletRadius = 0
  Length = 3878.31
  MakeFace = false
  Points = (156) [(638.999,-1310,18),(633.999,-1310,18),(633.999,-1320,18),(671.999,-1320,18),(674.999,-1323,18),(674.999,-1377,18),(671.999,-1380,18),+149 more]
  Start = (638.999,-1310,18)
  Subdivisions = 0
FEATURE [Part::FeaturePython] Panel120  label="Struct outer bottom small 001"  # WARN: FeaturePython — macro-defined, semantics opaque (R4)
  Area = 142440
  Base = -> DWire020
  Description = struct bottom
  FaceMaker = 0
  HorizontalArea = 0
  Length = 0
  MoveWithHost = false
  Normal = (0,0,1)
  PerimeterLength = 0
  Role = 0
  Sheets = 1
  Tag = FRA-A/S2/EX
  Thickness = 18
  VerticalArea = 0
  WaveDirection = 0
  WaveHeight = 0
  WaveLength = 0
  WaveType = 0
  Width = 0
FEATURE [Part::FeaturePython] Panel136  label="Struct outer bottom small 002"  # WARN: FeaturePython — macro-defined, semantics opaque (R4)
  Area = 142440
  CloneOf = -> Panel120
  Description = struct bottom
  FaceMaker = 0
  HorizontalArea = 0
  Length = 0
  MoveWithHost = false
  Normal = (0,0,0)
  PerimeterLength = 0
  Placement = pos=(-1200,0,0) rot=(0,0,1;0rad)
  Role = 0
  Sheets = 1
  Tag = FRA-A/S2/EX
  Thickness = 18
  VerticalArea = 0
  WaveDirection = 0
  WaveHeight = 0
  WaveLength = 0
  WaveType = 0
  Width = 0
FEATURE [Part::FeaturePython] PanelView043  label="View of Struct outer bottom small 001"  # WARN: FeaturePython — macro-defined, semantics opaque (R4)
  FontFile = <userpath>/.fonts/stick/1CamBam_Stick_2.ttf
  MakeFace = true
  Placement = pos=(-5300,300,0) rot=(0,0,1;0rad)
  Source = -> Panel120
  TagPosition = (0,0,0)
  TagRotation = 90
  TagSize = 10
  TagText = %tag%
FEATURE [Part::FeaturePython] PanelView093  label="View of Struct outer bottom small 002"  # WARN: FeaturePython — macro-defined, semantics opaque (R4)
  FontFile = <userpath>/.fonts/stick/1CamBam_Stick_2.ttf
  MakeFace = false
  Placement = pos=(-5900,799.674,22.8343) rot=(0,0,1;0rad)
  Source = -> Panel136
  TagPosition = (0,0,0)
  TagRotation = 90
  TagSize = 10
  TagText = %tag%
FEATURE [Part::FeaturePython] PanelView197  label="View of Struct outer bottom small 003"  # WARN: FeaturePython — macro-defined, semantics opaque (R4)
  FontFile = <userpath>/.fonts/stick/1CamBam_Stick_2.ttf
  MakeFace = false
  Placement = pos=(11600,-2200,0) rot=(0,0,1;0rad)
  Source = -> Panel136
  TagPosition = (0,0,0)
  TagRotation = 90
  TagSize = 10
  TagText = %tag%
FEATURE [Part::Part2DObjectPython] DWire021  # Draft 2D object (typed FeaturePython)
  ChamferSize = 0
  Closed = true
  End = (560.999,170.112,0)
  FilletRadius = 0
  Length = 6300.44
  MakeFace = false
  Points = (196) [(560.999,70.1138,0),(565.999,70.1138,0),(565.999,60.113,0),(527.999,60.113,0),(524.999,57.1133,0),(524.999,3.11371,0),(527.999,0.114148,0),+189 more]
  Start = (560.999,70.1138,0)
  Subdivisions = 0
FEATURE [Part::FeaturePython] Panel117  label="Struct inner roof 001"  # WARN: FeaturePython — macro-defined, semantics opaque (R4)
  Area = 229641
  Base = -> DWire021
  Description = struct roof
  FaceMaker = 0
  HorizontalArea = 0
  Length = 0
  MoveWithHost = false
  Normal = (0,0,1)
  PerimeterLength = 0
  Placement = pos=(0,375.491,3596.45) rot=(-1,0,0;0.655696rad)
  Role = 0
  Sheets = 1
  Tag = FRA-A/S5/IN
  Thickness = 18
  VerticalArea = 0
  WaveDirection = 0
  WaveHeight = 0
  WaveLength = 0
  WaveType = 0
  Width = 0
FEATURE [Part::FeaturePython] Panel138  label="Struct inner roof 002"  # WARN: FeaturePython — macro-defined, semantics opaque (R4)
  Area = 229641
  CloneOf = -> Panel117
  Description = struct roof
  FaceMaker = 0
  HorizontalArea = 0
  Length = 0
  MoveWithHost = false
  Normal = (0,0,0)
  PerimeterLength = 0
  Placement = pos=(1200,-375.491,3596.45) rot=(0,-0.322006,0.946738;3.14159rad)
  Role = 0
  Sheets = 1
  Tag = FRA-A/S5/IN
  Thickness = 18
  VerticalArea = 0
  WaveDirection = 0
  WaveHeight = 0
  WaveLength = 0
  WaveType = 0
  Width = 0
FEATURE [Part::FeaturePython] Panel142  label="Struct inner roof 003"  # WARN: FeaturePython — macro-defined, semantics opaque (R4)
  Area = 229641
  CloneOf = -> Panel117
  Description = struct roof
  FaceMaker = 0
  HorizontalArea = 0
  Length = 0
  MoveWithHost = false
  Normal = (0,0,0)
  PerimeterLength = 0
  Placement = pos=(4e-09,-375.491,3596.45) rot=(0,-0.322006,0.946738;3.14159rad)
  Role = 0
  Sheets = 1
  Tag = FRA-A/S5/IN
  Thickness = 18
  VerticalArea = 0
  WaveDirection = 0
  WaveHeight = 0
  WaveLength = 0
  WaveType = 0
  Width = 0
FEATURE [Part::FeaturePython] Panel143  label="Struct inner roof 004"  # WARN: FeaturePython — macro-defined, semantics opaque (R4)
  Area = 229641
  CloneOf = -> Panel117
  Description = struct roof
  FaceMaker = 0
  HorizontalArea = 0
  Length = 0
  MoveWithHost = false
  Normal = (0,0,0)
  PerimeterLength = 0
  Placement = pos=(-1200,375.491,3596.45) rot=(-1,0,0;0.655696rad)
  Role = 0
  Sheets = 1
  Tag = FRA-A/S5/IN
  Thickness = 18
  VerticalArea = 0
  WaveDirection = 0
  WaveHeight = 0
  WaveLength = 0
  WaveType = 0
  Width = 0
FEATURE [Part::FeaturePython] PanelView022  label="View of Struct inner roof 002"  # WARN: FeaturePython — macro-defined, semantics opaque (R4)
  FontFile = <userpath>/.fonts/stick/1CamBam_Stick_2.ttf
  MakeFace = true
  Placement = pos=(2300,700,0) rot=(0,0,1;0rad)
  Source = -> Panel138
  TagPosition = (0,0,0)
  TagRotation = 90
  TagSize = 10
  TagText = %tag%
FEATURE [Part::FeaturePython] PanelView040  label="View of Struct inner roof 001"  # WARN: FeaturePython — macro-defined, semantics opaque (R4)
  FontFile = <userpath>/.fonts/stick/1CamBam_Stick_2.ttf
  MakeFace = true
  Placement = pos=(2900,700,0) rot=(0,0,1;0rad)
  Source = -> Panel117
  TagPosition = (0,0,0)
  TagRotation = 90
  TagSize = 10
  TagText = %tag%
FEATURE [Part::FeaturePython] PanelView096  label="View of Struct inner roof 003"  # WARN: FeaturePython — macro-defined, semantics opaque (R4)
  FontFile = <userpath>/.fonts/stick/1CamBam_Stick_2.ttf
  MakeFace = false
  Placement = pos=(500,-99.9593,-2.85428) rot=(0,0,1;0rad)
  Source = -> Panel142
  TagPosition = (0,0,0)
  TagRotation = 90
  TagSize = 10
  TagText = %tag%
FEATURE [Part::FeaturePython] PanelView097  label="View of Struct inner roof 004"  # WARN: FeaturePython — macro-defined, semantics opaque (R4)
  FontFile = <userpath>/.fonts/stick/1CamBam_Stick_2.ttf
  MakeFace = false
  Placement = pos=(-300,0,0) rot=(0,0,1;0rad)
  Source = -> Panel143
  TagPosition = (0,0,0)
  TagRotation = 90
  TagSize = 10
  TagText = %tag%
FEATURE [Part::FeaturePython] PanelView185  label="View of Struct inner roof 005"  # WARN: FeaturePython — macro-defined, semantics opaque (R4)
  FontFile = <userpath>/.fonts/stick/1CamBam_Stick_2.ttf
  MakeFace = false
  Placement = pos=(11000,-200,0) rot=(0,0,1;0rad)
  Source = -> Panel142
  TagPosition = (0,0,0)
  TagRotation = 90
  TagSize = 10
  TagText = %tag%
FEATURE [Part::FeaturePython] PanelView195  label="View of Struct inner roof 006"  # WARN: FeaturePython — macro-defined, semantics opaque (R4)
  FontFile = <userpath>/.fonts/stick/1CamBam_Stick_2.ttf
  MakeFace = false
  Placement = pos=(11400,-200,0) rot=(0,0,1;0rad)
  Source = -> Panel143
  TagPosition = (0,0,0)
  TagRotation = 90
  TagSize = 10
  TagText = %tag%
FEATURE [Part::Part2DObjectPython] DWire022  # Draft 2D object (typed FeaturePython)
  ChamferSize = 0
  Closed = true
  End = (565.999,296.942,0)
  FilletRadius = 0
  Length = 5414.88
  MakeFace = false
  Points = (202) [(560.999,296.942,0),(542.999,296.942,0),(542.999,406.942,0),(547.999,406.942,0),(547.999,416.943,0),(527.999,416.943,0),(524.999,419.943,0),+195 more]
  Start = (560.999,296.942,0)
  Subdivisions = 0
FEATURE [Part::FeaturePython] Panel118  label="Struct outer roof large 001"  # WARN: FeaturePython — macro-defined, semantics opaque (R4)
  Area = 195264
  Base = -> DWire022
  Description = struct roof
  FaceMaker = 0
  HorizontalArea = 0
  Length = 0
  MoveWithHost = false
  Normal = (0,0,1)
  PerimeterLength = 0
  Placement = pos=(0,424.341,3851.57) rot=(-1,0,0;0.655695rad)
  Role = 0
  Sheets = 1
  Tag = FRA-A/S5/EX
  Thickness = 18
  VerticalArea = 0
  WaveDirection = 0
  WaveHeight = 0
  WaveLength = 0
  WaveType = 0
  Width = 0
FEATURE [Part::FeaturePython] Panel137  label="Struct outer roof large 002"  # WARN: FeaturePython — macro-defined, semantics opaque (R4)
  Area = 195264
  CloneOf = -> Panel118
  Description = struct roof
  FaceMaker = 0
  HorizontalArea = 0
  Length = 0
  MoveWithHost = false
  Normal = (0,0,0)
  PerimeterLength = 0
  Placement = pos=(1200,-424.341,3851.57) rot=(0,-0.322006,0.946738;3.14159rad)
  Role = 0
  Sheets = 1
  Tag = FRA-A/S5/EX
  Thickness = 18
  VerticalArea = 0
  WaveDirection = 0
  WaveHeight = 0
  WaveLength = 0
  WaveType = 0
  Width = 0
FEATURE [Part::FeaturePython] Panel144  label="Struct outer roof large 003"  # WARN: FeaturePython — macro-defined, semantics opaque (R4)
  Area = 195264
  CloneOf = -> Panel118
  Description = struct roof
  FaceMaker = 0
  HorizontalArea = 0
  Length = 0
  MoveWithHost = false
  Normal = (0,0,0)
  PerimeterLength = 0
  Placement = pos=(-1200,424.341,3851.57) rot=(-1,0,0;0.655695rad)
  Role = 0
  Sheets = 1
  Tag = FRA-A/S5/EX
  Thickness = 18
  VerticalArea = 0
  WaveDirection = 0
  WaveHeight = 0
  WaveLength = 0
  WaveType = 0
  Width = 0
FEATURE [Part::FeaturePython] Panel145  label="Struct outer roof large 004"  # WARN: FeaturePython — macro-defined, semantics opaque (R4)
  Area = 195264
  CloneOf = -> Panel118
  Description = struct roof
  FaceMaker = 0
  HorizontalArea = 0
  Length = 0
  MoveWithHost = false
  Normal = (0,0,0)
  PerimeterLength = 0
  Placement = pos=(4e-09,-424.341,3851.57) rot=(0,-0.322006,0.946738;3.14159rad)
  Role = 0
  Sheets = 1
  Tag = FRA-A/S5/EX
  Thickness = 18
  VerticalArea = 0
  WaveDirection = 0
  WaveHeight = 0
  WaveLength = 0
  WaveType = 0
  Width = 0
FEATURE [App::DocumentObjectGroupPython] VisGroup002  label="level3 structure (1 originals)"  # scripted group (container) (typed FeaturePython)
  Group = -> [Panel091,Panel092,Panel093,Panel098,Panel099,Panel102,Panel103,Panel106,Panel107,Panel123,Panel124,Panel125,Panel126,Panel129,Panel130,Panel131,Panel132,Panel133,Panel134,Panel135,Panel136,Panel140,Panel141,Panel142,Panel143,Panel144,Panel145,Panel090]
FEATURE [App::DocumentObjectGroupPython] VisGroup011  label="Endcap structure (11 originals)"  # scripted group (container) (typed FeaturePython)
  Group = -> [Panel138,Panel137,Panel139,Panel119,Panel117,Panel118,Panel112,Panel113,Panel111,Panel110,Panel122,Panel121,Panel128,Panel127,Panel094,Panel095,Panel105,Panel104,Panel109,Panel108,Panel096,Panel097,Panel114,Panel120,Panel116,Panel115,Panel101,Panel100]
FEATURE [App::DocumentObjectGroup] Group001  label="Endcap - 52 peças"
  Group = -> [VisGroup009,VisGroup010,VisGroup011,VisGroup012]
FEATURE [Part::FeaturePython] PanelView041  label="View of Struct outer roof large 001"  # WARN: FeaturePython — macro-defined, semantics opaque (R4)
  FontFile = <userpath>/.fonts/stick/1CamBam_Stick_2.ttf
  MakeFace = true
  Placement = pos=(-900,0,0) rot=(0,0,1;0rad)
  Source = -> Panel118
  TagPosition = (0,0,0)
  TagRotation = 90
  TagSize = 10
  TagText = %tag%
FEATURE [Part::FeaturePython] PanelView048  label="View of Struct outer roof large 002"  # WARN: FeaturePython — macro-defined, semantics opaque (R4)
  FontFile = <userpath>/.fonts/stick/1CamBam_Stick_2.ttf
  MakeFace = true
  Placement = pos=(-4700,0,0) rot=(0,0,1;0rad)
  Source = -> Panel137
  TagPosition = (0,0,0)
  TagRotation = 90
  TagSize = 10
  TagText = %tag%
FEATURE [App::DocumentObjectGroup] Group007  label="Views endcap - 52 peças"
  Group = -> [PanelView,PanelView001,PanelView002,PanelView003,PanelView004,PanelView005,PanelView006,PanelView007,PanelView008,PanelView009,PanelView010,PanelView011,PanelView012,PanelView013,PanelView014,PanelView015,PanelView016,PanelView017,PanelView018,PanelView019,PanelView020,PanelView021,PanelView022,PanelView023,PanelView024,PanelView025,PanelView026,PanelView027,PanelView028,PanelView029,PanelView030,+21 more]
FEATURE [Part::FeaturePython] PanelView098  label="View of Struct outer roof large 003"  # WARN: FeaturePython — macro-defined, semantics opaque (R4)
  FontFile = <userpath>/.fonts/stick/1CamBam_Stick_2.ttf
  MakeFace = false
  Placement = pos=(-5100,499.796,14.2714) rot=(0,0,1;0rad)
  Source = -> Panel144
  TagPosition = (0,0,0)
  TagRotation = 90
  TagSize = 10
  TagText = %tag%
FEATURE [Part::FeaturePython] PanelView099  label="View of Struct outer roof large 004"  # WARN: FeaturePython — macro-defined, semantics opaque (R4)
  FontFile = <userpath>/.fonts/stick/1CamBam_Stick_2.ttf
  MakeFace = false
  Placement = pos=(-6200,799.674,22.8343) rot=(0,0,1;0rad)
  Source = -> Panel145
  TagPosition = (0,0,0)
  TagRotation = 90
  TagSize = 10
  TagText = %tag%
FEATURE [Part::FeaturePython] PanelView191  label="View of Struct outer roof large 005"  # WARN: FeaturePython — macro-defined, semantics opaque (R4)
  FontFile = <userpath>/.fonts/stick/1CamBam_Stick_2.ttf
  MakeFace = false
  Placement = pos=(13800,-300,0) rot=(0,0,1;0rad)
  Source = -> Panel144
  TagPosition = (0,0,0)
  TagRotation = 90
  TagSize = 10
  TagText = %tag%
FEATURE [Part::FeaturePython] PanelView205  label="View of Struct outer roof large 006"  # WARN: FeaturePython — macro-defined, semantics opaque (R4)
  FontFile = <userpath>/.fonts/stick/1CamBam_Stick_2.ttf
  MakeFace = false
  Placement = pos=(14200,-300,0) rot=(0,0,1;0rad)
  Source = -> Panel145
  TagPosition = (0,0,0)
  TagRotation = 90
  TagSize = 10
  TagText = %tag%
FEATURE [Part::Part2DObjectPython] Circle  # Draft 2D object (typed FeaturePython)
  FirstAngle = 0
  LastAngle = 0
  MakeFace = false
  Placement = pos=(0,149.999,0) rot=(0,0,1;0rad)
  Radius = 50
FEATURE [Part::Part2DObjectPython] Clone2D007  label="Circle (2D)"  # Draft 2D object (typed FeaturePython)
  Objects = -> [Circle]
  Placement = pos=(-200,149.999,0) rot=(0,0,1;0rad)
  Scale = (1,1,1)
FEATURE [Part::Part2DObjectPython] Clone2D008  label="Circle (2D)001"  # Draft 2D object (typed FeaturePython)
  Objects = -> [Circle]
  Placement = pos=(200,149.999,0) rot=(0,0,1;0rad)
  Scale = (1,1,1)
FEATURE [Part::Compound] Compound009  label="inner roof panel profile"
  Links = -> [Shape034017,Shape034027,Shape034026,Shape034018,Shape034020,Shape034029,Shape034030,Shape034025,Shape034024,Shape034021,Shape034031,Shape034023,Shape034028,Shape034019,Shape034022,Circle,Clone2D007,Clone2D008]
FEATURE [Part::FeaturePython] Panel032  label="Inner roof panel 001"  # WARN: FeaturePython — macro-defined, semantics opaque (R4)
  Area = 2.63544e+06
  Base = -> Compound009
  Description = Inner roof panel
  FaceMaker = 0
  HorizontalArea = 0
  Length = 0
  MoveWithHost = false
  Normal = (0,0,1)
  PerimeterLength = 0
  Placement = pos=(0,-1.0109e-08,3862.58) rot=(-1,0,0;0.655695rad)
  Role = 0
  Sheets = 1
  Tag = L64
  Thickness = 18
  VerticalArea = 0
  WaveDirection = 0
  WaveHeight = 0
  WaveLength = 0
  WaveType = 0
  Width = 0
FEATURE [Part::FeaturePython] Panel033  label="Inner roof panel 002"  # WARN: FeaturePython — macro-defined, semantics opaque (R4)
  Area = 2.63544e+06
  CloneOf = -> Panel032
  Description = Inner roof panel
  FaceMaker = 0
  HorizontalArea = 0
  Length = 0
  MoveWithHost = false
  Normal = (0,0,0)
  PerimeterLength = 0
  Placement = pos=(-0.00231934,1.19e-10,3862.58) rot=(0,-0.322006,0.946738;3.14159rad)
  Role = 0
  Sheets = 1
  Tag = L64
  Thickness = 18
  VerticalArea = 0
  WaveDirection = 0
  WaveHeight = 0
  WaveLength = 0
  WaveType = 0
  Width = 0
FEATURE [Part::FeaturePython] PanelView132  label="View of Inner roof panel 001"  # WARN: FeaturePython — macro-defined, semantics opaque (R4)
  FontFile = <userpath>/.fonts/stick/1CamBam_Stick_2.ttf
  MakeFace = false
  Placement = pos=(2900,0,0) rot=(0,0,1;0rad)
  Source = -> Panel032
  TagPosition = (0,0,0)
  TagRotation = 0
  TagSize = 10
  TagText = %tag%
FEATURE [Part::FeaturePython] PanelView133  label="View of Inner roof panel 002"  # WARN: FeaturePython — macro-defined, semantics opaque (R4)
  FontFile = <userpath>/.fonts/stick/1CamBam_Stick_2.ttf
  MakeFace = false
  Placement = pos=(4200,0,0) rot=(0,0,1;0rad)
  Source = -> Panel033
  TagPosition = (0,0,0)
  TagRotation = 0
  TagSize = 10
  TagText = %tag%
FEATURE [Part::FeaturePython] PanelView146  label="View of Inner roof panel 003"  # WARN: FeaturePython — macro-defined, semantics opaque (R4)
  FontFile = <userpath>/.fonts/stick/1CamBam_Stick_2.ttf
  MakeFace = false
  Placement = pos=(4700,100,0) rot=(0,0,1;0rad)
  Source = -> Panel032
  TagPosition = (0,0,0)
  TagRotation = 0
  TagSize = 10
  TagText = %tag%
FEATURE [Part::FeaturePython] PanelView148  label="View of Inner roof panel 004"  # WARN: FeaturePython — macro-defined, semantics opaque (R4)
  FontFile = <userpath>/.fonts/stick/1CamBam_Stick_2.ttf
  MakeFace = false
  Placement = pos=(7500,100,0) rot=(0,0,1;0rad)
  Source = -> Panel033
  TagPosition = (0,0,0)
  TagRotation = 0
  TagSize = 10
  TagText = %tag%
FEATURE [Part::Part2DObjectPython] Clone2D009  label="Circle (2D)002"  # Draft 2D object (typed FeaturePython)
  Objects = -> [Circle]
  Placement = pos=(-1486.92,275.758,0) rot=(0,0,1;0rad)
  Scale = (1,1,1)
FEATURE [Part::Part2DObjectPython] Clone2D010  label="Circle (2D)002 (2D)"  # Draft 2D object (typed FeaturePython)
  Objects = -> [Clone2D009]
  Placement = pos=(-1286.92,275.758,0) rot=(0,0,1;0rad)
  Scale = (1,1,1)
FEATURE [Part::Part2DObjectPython] Clone2D011  label="Circle (2D)002 (2D)001"  # Draft 2D object (typed FeaturePython)
  Objects = -> [Clone2D009]
  Placement = pos=(-1686.92,275.758,0) rot=(0,0,1;0rad)
  Scale = (1,1,1)
FEATURE [Part::Compound] Compound027  label="Outer roof profile S"
  Links = -> [Wire125,Wire126,Wire127,Clone2D009,Clone2D010,Clone2D011]
FEATURE [Part::FeaturePython] Panel080  label="Outer roof panel small 001"  # WARN: FeaturePython — macro-defined, semantics opaque (R4)
  Area = 617923
  Base = -> Compound027
  Description = Roof panel
  FaceMaker = 0
  HorizontalArea = 0
  Length = 0
  MoveWithHost = false
  Normal = (0,0,1)
  PerimeterLength = 0
  Placement = pos=(1486.92,-421.605,3876.38) rot=(1,0,0;0.655696rad)
  Role = 0
  Sheets = 1
  Tag = L48
  Thickness = 18
  VerticalArea = 0
  WaveDirection = 0
  WaveHeight = 0
  WaveLength = 0
  WaveType = 0
  Width = 0
FEATURE [Part::FeaturePython] Panel088  label="Outer roof panel small 002"  # WARN: FeaturePython — macro-defined, semantics opaque (R4)
  Area = 617923
  CloneOf = -> Panel080
  Description = Roof panel
  FaceMaker = 0
  HorizontalArea = 0
  Length = 0
  MoveWithHost = false
  Normal = (0,0,0)
  PerimeterLength = 0
  Placement = pos=(1486.92,432.58,3890.65) rot=(1,0,0;2.4859rad)
  Role = 0
  Sheets = 1
  Tag = L48
  Thickness = 18
  VerticalArea = 0
  WaveDirection = 0
  WaveHeight = 0
  WaveLength = 0
  WaveType = 0
  Width = 0
FEATURE [App::DocumentObjectGroupPython] VisGroup004  label="level5 outer panels (8 originals)"  # scripted group (container) (typed FeaturePython)
  Group = -> [Panel073,Panel074,Panel075,Panel076,Panel079,Panel080,Panel081,Panel082,Panel083,Panel084,Panel085,Panel086,Panel087,Panel088,Panel089]
FEATURE [Part::FeaturePython] PanelView122  label="View of Outer roof panel small 001"  # WARN: FeaturePython — macro-defined, semantics opaque (R4)
  FontFile = <userpath>/.fonts/stick/1CamBam_Stick_2.ttf
  MakeFace = false
  Placement = pos=(400,2099.14,59.9399) rot=(0,0,1;0rad)
  Source = -> Panel080
  TagPosition = (0,-99.1444,-59.9399)
  TagRotation = 0
  TagSize = 10
  TagText = %tag%
FEATURE [Part::FeaturePython] PanelView128  label="View of Outer roof panel small 002"  # WARN: FeaturePython — macro-defined, semantics opaque (R4)
  FontFile = <userpath>/.fonts/stick/1CamBam_Stick_2.ttf
  MakeFace = false
  Placement = pos=(4800,2199.1,62.7942) rot=(0,0,1;0rad)
  Source = -> Panel088
  TagPosition = (0,-99.1037,-62.7942)
  TagRotation = 0
  TagSize = 10
  TagText = %tag%
FEATURE [Part::FeaturePython] PanelView152  label="View of Outer roof panel small 003"  # WARN: FeaturePython — macro-defined, semantics opaque (R4)
  FontFile = <userpath>/.fonts/stick/1CamBam_Stick_2.ttf
  MakeFace = false
  Placement = pos=(-5700,-1700,0) rot=(0,0,1;0rad)
  Source = -> Panel088
  TagPosition = (0,-100,0)
  TagRotation = 0
  TagSize = 10
  TagText = %tag%
FEATURE [Part::FeaturePython] PanelView158  label="View of Outer roof panel small 004"  # WARN: FeaturePython — macro-defined, semantics opaque (R4)
  FontFile = <userpath>/.fonts/stick/1CamBam_Stick_2.ttf
  MakeFace = false
  Placement = pos=(-5700,-4100,0) rot=(0,0,1;0rad)
  Source = -> Panel080
  TagPosition = (0,-100,0)
  TagRotation = 0
  TagSize = 10
  TagText = %tag%
FEATURE [Part::Part2DObjectPython] DWire023  # Draft 2D object (typed FeaturePython)
  ChamferSize = 0
  Closed = true
  End = (-411,-1807,857.998)
  FilletRadius = 0
  Length = 611.999
  MakeFace = false
  Placement = pos=(150,0,264.999) rot=(0,0,1;0rad)
  Points = (12) [(-561,-1807,362.999),(-566,-1807,362.999),(-566,-1807,352.999),(-520,-1807,352.999),(-520,-1807,362.999),(-525,-1807,362.999),(-525,-1807,592.999),+5 more]
  Start = (-411,-1807,627.999)
  Subdivisions = 0
FEATURE [Part::Part2DObjectPython] Clone2D012  label="DWire023 (2D)"  # Draft 2D object (typed FeaturePython)
  Objects = -> [DWire023]
  Placement = pos=(935.998,0,264.999) rot=(0,0,1;0rad)
  Scale = (1,1,1)
FEATURE [Part::Part2DObjectPython] Clone2D013  label="DWire023 (2D)001"  # Draft 2D object (typed FeaturePython)
  Objects = -> [DWire023]
  Placement = pos=(150,0,1458) rot=(0,0,1;0rad)
  Scale = (1,1,1)
FEATURE [Part::Part2DObjectPython] Clone2D014  label="DWire023 (2D) (2D)"  # Draft 2D object (typed FeaturePython)
  Objects = -> [Clone2D012]
  Placement = pos=(935.998,0,1458) rot=(0,0,1;0rad)
  Scale = (1,1,1)
FEATURE [Part::Part2DObjectPython] Clone2D015  label="DWire023 (2D)002"  # Draft 2D object (typed FeaturePython)
  Objects = -> [DWire023]
  Placement = pos=(150,0,857.999) rot=(0,0,1;0rad)
  Scale = (1,1,1)
FEATURE [Part::Part2DObjectPython] Clone2D016  label="DWire023 (2D) (2D)001"  # Draft 2D object (typed FeaturePython)
  Objects = -> [Clone2D012]
  Placement = pos=(935.998,0,857.999) rot=(0,0,1;0rad)
  Scale = (1,1,1)
FEATURE [Part::Compound] Compound007  label="inner side panel profile"
  Links = -> [Shape035,Wire051,Wire050,Wire052,Wire055,Wire045,Wire043,Wire057,Wire053,Wire054,Wire047,Wire046,Wire044,Wire056,Wire049,DWire023,Clone2D012,Clone2D016,Clone2D013,Clone2D014,Clone2D015]
FEATURE [Part::FeaturePython] Panel030  label="Inner side panel 001"  # WARN: FeaturePython — macro-defined, semantics opaque (R4)
  Area = 2.49226e+06
  Base = -> Compound007
  Description = Side panel
  FaceMaker = 0
  HorizontalArea = 0
  Length = 0
  MoveWithHost = false
  Normal = (0,-1,0)
  PerimeterLength = 0
  Role = 0
  Sheets = 1
  Tag = L63
  Thickness = 18
  VerticalArea = 0
  WaveDirection = 0
  WaveHeight = 0
  WaveLength = 0
  WaveType = 0
  Width = 0
FEATURE [Part::FeaturePython] Panel031  label="Inner side panel 002"  # WARN: FeaturePython — macro-defined, semantics opaque (R4)
  Area = 2.49226e+06
  CloneOf = -> Panel030
  Description = Side Panel
  FaceMaker = 0
  HorizontalArea = 0
  Length = 0
  MoveWithHost = false
  Normal = (0,0,0)
  PerimeterLength = 0
  Placement = pos=(0,3631.99,0) rot=(0,0,1;0rad)
  Role = 0
  Sheets = 1
  Tag = L63
  Thickness = 18
  VerticalArea = 0
  WaveDirection = 0
  WaveHeight = 0
  WaveLength = 0
  WaveType = 0
  Width = 0
FEATURE [App::DocumentObjectGroupPython] VisGroup005  label="level6 inner panels  (4 originals)"  # scripted group (container) (typed FeaturePython)
  Group = -> [Panel029,Panel031,Panel032,Panel033]
FEATURE [App::DocumentObjectGroupPython] VisGroup008  label="level8 original (4 originals)"  # scripted group (container) (typed FeaturePython)
  Group = -> [Panel028,Panel030,Panel077,Panel078]
FEATURE [App::DocumentObjectGroup] Group005  label="Base component - 90 peças"
  Group = -> [VisGroup,VisGroup001,VisGroup002,VisGroup003,VisGroup004,VisGroup005,VisGroup006,VisGroup008]
FEATURE [Part::FeaturePython] PanelView131  label="View of Inner side panel 002"  # WARN: FeaturePython — macro-defined, semantics opaque (R4)
  FontFile = <userpath>/.fonts/stick/1CamBam_Stick_2.ttf
  MakeFace = false
  Placement = pos=(5500,0,0) rot=(0,0,1;0rad)
  Source = -> Panel031
  TagPosition = (0,0,0)
  TagRotation = 0
  TagSize = 10
  TagText = %tag%
FEATURE [Part::FeaturePython] PanelView147  label="View of Inner side panel 003"  # WARN: FeaturePython — macro-defined, semantics opaque (R4)
  FontFile = <userpath>/.fonts/stick/1CamBam_Stick_2.ttf
  MakeFace = false
  Placement = pos=(6100,100,0) rot=(0,0,1;0rad)
  Source = -> Panel031
  TagPosition = (0,0,0)
  TagRotation = 0
  TagSize = 10
  TagText = %tag%
FEATURE [Part::FeaturePython] PanelView229  label="View of Floor panel small 001"  # WARN: FeaturePython — macro-defined, semantics opaque (R4)
  FontFile = <userpath>/.fonts/stick/1CamBam_Stick_2.ttf
  MakeFace = false
  Placement = pos=(-6500,3100,0) rot=(0,0,1;0rad)
  Source = -> Panel028
  TagPosition = (0,0,0)
  TagRotation = 0
  TagSize = 10
  TagText = %tag%
FEATURE [Part::FeaturePython] PanelView230  label="View of Inner side panel 001"  # WARN: FeaturePython — macro-defined, semantics opaque (R4)
  FontFile = <userpath>/.fonts/stick/1CamBam_Stick_2.ttf
  MakeFace = false
  Placement = pos=(-7800,3100,0) rot=(0,0,1;0rad)
  Source = -> Panel030
  TagPosition = (0,0,0)
  TagRotation = 0
  TagSize = 10
  TagText = %tag%
FEATURE [Part::FeaturePython] PanelView231  label="View of Outer side panel large 001"  # WARN: FeaturePython — macro-defined, semantics opaque (R4)
  FontFile = <userpath>/.fonts/stick/1CamBam_Stick_2.ttf
  MakeFace = false
  Placement = pos=(-3700,3100,0) rot=(0,0,1;0rad)
  Source = -> Panel077
  TagPosition = (0,0,0)
  TagRotation = 0
  TagSize = 10
  TagText = %tag%
FEATURE [Part::FeaturePython] PanelView232  label="View of Outer side panel small 001"  # WARN: FeaturePython — macro-defined, semantics opaque (R4)
  FontFile = <userpath>/.fonts/stick/1CamBam_Stick_2.ttf
  MakeFace = false
  Placement = pos=(-5000,3100,0) rot=(0,0,1;0rad)
  Source = -> Panel078
  TagPosition = (0,0,0)
  TagRotation = 0
  TagSize = 10
  TagText = %tag%
FEATURE [Part::Part2DObjectPython] Circle001  # Draft 2D object (typed FeaturePython)
  FirstAngle = 0
  LastAngle = 0
  MakeFace = false
  Placement = pos=(-6000,-2200,0) rot=(0,0,1;0rad)
  Radius = 50
FEATURE [Part::FeaturePython] Array  # Draft array (typed FeaturePython)
  Angle = 360
  ArrayType = 0
  Axis = (0,0,1)
  Base = -> Circle001
  Center = (0,0,0)
  Fuse = false
  IntervalAxis = (0,0,0)
  IntervalX = (200,0,0)
  IntervalY = (0,200,0)
  IntervalZ = (0,0,0)
  NumberPolar = 1
  NumberX = 6
  NumberY = 2
  NumberZ = 1
  Placement = pos=(-300,-200,0) rot=(0,0,1;0rad)
FEATURE [App::DocumentObjectGroup] Group008  label="Views module - 90 peças + 1"
  Group = -> [PanelView050,PanelView051,PanelView052,PanelView053,PanelView054,PanelView055,PanelView056,PanelView057,PanelView058,PanelView059,PanelView060,PanelView061,PanelView062,PanelView063,PanelView064,PanelView065,PanelView066,PanelView067,PanelView068,PanelView069,PanelView070,PanelView071,PanelView072,PanelView073,PanelView074,PanelView075,PanelView076,PanelView077,PanelView078,PanelView079,+61 more]
FEATURE [Part::FeaturePython] Clone093  label="Array018"  # Draft clone (typed FeaturePython)
  AttacherType = Attacher::AttachEngine3D
  Objects = -> [Array]
  Placement = pos=(-200,-1300,0) rot=(0,0,1;0rad)
  Scale = (1,1,1)
FEATURE [App::DocumentObjectGroup] Group009  label="Views window - 91 peças + 1"
  Group = -> [PanelView138,PanelView139,PanelView140,PanelView141,PanelView142,PanelView143,PanelView144,PanelView145,PanelView146,PanelView147,PanelView148,PanelView149,PanelView150,PanelView151,PanelView152,PanelView153,PanelView154,PanelView155,PanelView156,PanelView157,PanelView158,PanelView159,PanelView160,PanelView161,PanelView162,PanelView163,PanelView164,PanelView165,PanelView166,PanelView167,+62 more]
FEATURE [Part::FeaturePython] PanelSheet  # WARN: FeaturePython — macro-defined, semantics opaque (R4)
  FillRatio = 0
  FontFile = <userpath>/.fonts/stick/1CamBam_Stick_2.ttf
  GrainDirection = 0
  Height = 2440
  MakeFace = true
  Placement = pos=(7101.78,-2955.57,0) rot=(0,0,1;0rad)
  TagPosition = (0,0,0)
  TagRotation = 0
  TagSize = 10
  Width = 1220
FEATURE [Part::FeaturePython] Screw  label="M10x12-Screw"  # Fasteners workbench fastener (typed FeaturePython)
  Placement = pos=(579.211,-2095.3,2247.56) rot=(1,0,0;1.5708rad)
  diameter = 10
  invert = false
  length = 0
  matchOuter = false
  offset = 0
  thread = false
  type = 4
FEATURE [Part::FeaturePython] PressNut  label="M12-PressNut"  # WARN: FeaturePython — macro-defined, semantics opaque (R4)
  Placement = pos=(579.211,-2086.52,2247.56) rot=(1,0,0;1.5708rad)
  diameter = 10
  invert = false
  offset = 0
  tcode = 2
FEATURE [Part::Compound] Compound028
  Links = -> [Screw,PressNut]
FEATURE [Part::FeaturePython] Array001  label="Array004 - 4 parafusos"  # Draft array (typed FeaturePython)
  Angle = 360
  ArrayType = 0
  Axis = (0,0,1)
  Base = -> Compound028
  Center = (0,0,0)
  Fuse = false
  IntervalAxis = (0,0,0)
  IntervalX = (-1160,0,0)
  IntervalY = (0,1,0)
  IntervalZ = (0,0,230)
  NumberPolar = 1
  NumberX = 2
  NumberY = 1
  NumberZ = 2
FEATURE [Part::FeaturePython] Array002  label="Array005 - 8 parafusos"  # Draft array (typed FeaturePython)
  Angle = 360
  ArrayType = 0
  Axis = (0,0,1)
  Base = -> Compound028
  Center = (0,0,0)
  Fuse = false
  IntervalAxis = (0,0,0)
  IntervalX = (-1160,0,0)
  IntervalY = (0,1,0)
  IntervalZ = (0,0,600)
  NumberPolar = 1
  NumberX = 2
  NumberY = 1
  NumberZ = 4
  Placement = pos=(0,-0.000116455,-1953.79) rot=(0,0,1;0rad)
FEATURE [App::FeaturePython] Section  # WARN: FeaturePython — macro-defined, semantics opaque (R4)
  Objects = -> [Array002]
  OnlySolids = true
  Placement = pos=(0,-56.2189,1575.66) rot=(0,0,1;0rad)
FEATURE [Part::FeaturePython] Array003  label="Array008 - 4 parafusos"  # Draft array (typed FeaturePython)
  Angle = 360
  ArrayType = 0
  Axis = (0,0,1)
  Base = -> Compound028
  Center = (0,0,0)
  Fuse = false
  IntervalAxis = (0,0,0)
  IntervalX = (-1160,0,0)
  IntervalY = (0,1,0)
  IntervalZ = (0,0,600)
  NumberPolar = 1
  NumberX = 2
  NumberY = 1
  NumberZ = 2
  Placement = pos=(0,-2423.63,-281.527) rot=(-1,0,0;0.915099rad)
FEATURE [Part::FeaturePython] Array004  label="Array009 - 4 parafusos"  # Draft array (typed FeaturePython)
  Angle = 360
  ArrayType = 0
  Axis = (0,0,1)
  Base = -> Compound028
  Center = (0,0,0)
  Fuse = false
  IntervalAxis = (0,0,0)
  IntervalX = (-1160,0,0)
  IntervalY = (0,1,0)
  IntervalZ = (0,0,230)
  NumberPolar = 1
  NumberX = 2
  NumberY = 1
  NumberZ = 2
  Placement = pos=(0,-809.844,959.854) rot=(-1,0,0;0.915099rad)
FEATURE [Part::FeaturePython] Array005  label="Array010 - 4 parafusos"  # Draft array (typed FeaturePython)
  Angle = 360
  ArrayType = 0
  Axis = (0,0,1)
  Base = -> Compound028
  Center = (0,0,0)
  Fuse = false
  IntervalAxis = (0,0,0)
  IntervalX = (-1160,0,0)
  IntervalY = (0,1,0)
  IntervalZ = (0,0,600)
  NumberPolar = 1
  NumberX = 2
  NumberY = 1
  NumberZ = 2
  Placement = pos=(-0.00143433,-1662.57,303.906) rot=(-1,0,0;0.915099rad)
FEATURE [Part::FeaturePython] Array006  label="Array014 - 4 parafusos"  # Draft array (typed FeaturePython)
  Angle = 360
  ArrayType = 0
  Axis = (0,0,1)
  Base = -> Compound028
  Center = (0,0,0)
  Fuse = false
  IntervalAxis = (0,0,0)
  IntervalX = (-1160,0,0)
  IntervalY = (0,1,0)
  IntervalZ = (0,0,230)
  NumberPolar = 1
  NumberX = 2
  NumberY = 1
  NumberZ = 2
  Placement = pos=(0,0,0) rot=(0,0,1;3.14159rad)
FEATURE [Part::FeaturePython] Array007  label="Array015 - 8 parafusos"  # Draft array (typed FeaturePython)
  Angle = 360
  ArrayType = 0
  Axis = (0,0,1)
  Base = -> Compound028
  Center = (0,0,0)
  Fuse = false
  IntervalAxis = (0,0,0)
  IntervalX = (-1160,0,0)
  IntervalY = (0,1,0)
  IntervalZ = (0,0,600)
  NumberPolar = 1
  NumberX = 2
  NumberY = 1
  NumberZ = 4
  Placement = pos=(0,0.000116455,-1953.79) rot=(0,0,1;3.14159rad)
FEATURE [Part::FeaturePython] Array008  label="Array016 - 4 parafusos"  # Draft array (typed FeaturePython)
  Angle = 360
  ArrayType = 0
  Axis = (0,0,1)
  Base = -> Compound028
  Center = (0,0,0)
  Fuse = false
  IntervalAxis = (0,0,0)
  IntervalX = (-1160,0,0)
  IntervalY = (0,1,0)
  IntervalZ = (0,0,600)
  NumberPolar = 1
  NumberX = 2
  NumberY = 1
  NumberZ = 2
  Placement = pos=(0,2423.63,-281.527) rot=(0,-0.441751,0.897138;3.14159rad)
FEATURE [Part::FeaturePython] Array009  label="Array017 - 4 parafusos"  # Draft array (typed FeaturePython)
  Angle = 360
  ArrayType = 0
  Axis = (0,0,1)
  Base = -> Compound028
  Center = (0,0,0)
  Fuse = false
  IntervalAxis = (0,0,0)
  IntervalX = (-1160,0,0)
  IntervalY = (0,1,0)
  IntervalZ = (0,0,230)
  NumberPolar = 1
  NumberX = 2
  NumberY = 1
  NumberZ = 2
  Placement = pos=(0,809.844,959.854) rot=(0,-0.441751,0.897138;3.14159rad)
FEATURE [Part::FeaturePython] Array010  label="Array018 - 4 parafusos"  # Draft array (typed FeaturePython)
  Angle = 360
  ArrayType = 0
  Axis = (0,0,1)
  Base = -> Compound028
  Center = (0,0,0)
  Fuse = false
  IntervalAxis = (0,0,0)
  IntervalX = (-1160,0,0)
  IntervalY = (0,1,0)
  IntervalZ = (0,0,600)
  NumberPolar = 1
  NumberX = 2
  NumberY = 1
  NumberZ = 2
  Placement = pos=(0.00143433,1662.57,303.906) rot=(0,-0.441751,0.897138;3.14159rad)
FEATURE [Part::FeaturePython] Array011  label="Array019 - 8 parafusos"  # Draft array (typed FeaturePython)
  Angle = 360
  ArrayType = 0
  Axis = (0,0,1)
  Base = -> Compound028
  Center = (0,0,0)
  Fuse = false
  IntervalAxis = (0,0,0)
  IntervalX = (-1160,0,0)
  IntervalY = (0,1,0)
  IntervalZ = (0,0,600)
  NumberPolar = 1
  NumberX = 2
  NumberY = 1
  NumberZ = 4
  Placement = pos=(0,3899.99,-1653.79) rot=(0,0,1;0rad)
FEATURE [Part::FeaturePython] Array012  label="Array020 - 8 parafusos"  # Draft array (typed FeaturePython)
  Angle = 0
  ArrayType = 0
  Axis = (0,0,1)
  Base = -> Compound028
  Center = (0,0,0)
  Fuse = false
  IntervalAxis = (0,0,0)
  IntervalX = (-1160,0,0)
  IntervalY = (0,1,0)
  IntervalZ = (0,0,600)
  NumberPolar = 1
  NumberX = 2
  NumberY = 1
  NumberZ = 4
  Placement = pos=(0,-3899.99,-1653.79) rot=(0,0,1;3.14159rad)
FEATURE [Part::FeaturePython] Array013  label="Array021 - 4 parafusos"  # Draft array (typed FeaturePython)
  Angle = 360
  ArrayType = 0
  Axis = (0,0,1)
  Base = -> Compound028
  Center = (0,0,0)
  Fuse = false
  IntervalAxis = (0,0,0)
  IntervalX = (-1160,0,0)
  IntervalY = (0,1,0)
  IntervalZ = (0,0,600)
  NumberPolar = 1
  NumberX = 2
  NumberY = 1
  NumberZ = 2
  Placement = pos=(0,473.639,6867.51) rot=(1,0,0;2.22649rad)
FEATURE [Part::FeaturePython] Array014  label="Array022 - 4 parafusos"  # Draft array (typed FeaturePython)
  Angle = 360
  ArrayType = 0
  Axis = (0,0,1)
  Base = -> Compound028
  Center = (0,0,0)
  Fuse = false
  IntervalAxis = (0,0,0)
  IntervalX = (-1160,0,0)
  IntervalY = (0,1,0)
  IntervalZ = (0,0,600)
  NumberPolar = 1
  NumberX = 2
  NumberY = 1
  NumberZ = 2
  Placement = pos=(0,-525.21,6099.17) rot=(1,0,0;2.22649rad)
FEATURE [Part::FeaturePython] Array015  label="Array025 - 4 parafusos"  # Draft array (typed FeaturePython)
  Angle = 360
  ArrayType = 0
  Axis = (0,0,1)
  Base = -> Compound028
  Center = (0,0,0)
  Fuse = false
  IntervalAxis = (0,0,0)
  IntervalX = (-1160,0,0)
  IntervalY = (0,1,0)
  IntervalZ = (0,0,600)
  NumberPolar = 1
  NumberX = 2
  NumberY = 1
  NumberZ = 2
  Placement = pos=(0,-473.639,6867.51) rot=(0,0.897138,0.441751;3.14159rad)
FEATURE [Part::FeaturePython] Array016  label="Array026 - 4 parafusos"  # Draft array (typed FeaturePython)
  Angle = 360
  ArrayType = 0
  Axis = (0,0,1)
  Base = -> Compound028
  Center = (0,0,0)
  Fuse = false
  IntervalAxis = (0,0,0)
  IntervalX = (-1160,0,0)
  IntervalY = (0,1,0)
  IntervalZ = (0,0,600)
  NumberPolar = 1
  NumberX = 2
  NumberY = 1
  NumberZ = 2
  Placement = pos=(0,525.21,6099.17) rot=(0,0.897138,0.441751;3.14159rad)
FEATURE [Part::FeaturePython] Array017  label="Array027 - 12 parafusos"  # Draft array (typed FeaturePython)
  Angle = 360
  ArrayType = 0
  Axis = (0,0,1)
  Base = -> Compound028
  Center = (0,0,0)
  Fuse = false
  IntervalAxis = (0,0,0)
  IntervalX = (-1160,0,0)
  IntervalY = (0,1,0)
  IntervalZ = (0,0,600)
  NumberPolar = 1
  NumberX = 2
  NumberY = 1
  NumberZ = 6
  Placement = pos=(0,-3747.56,-1807) rot=(-1,0,0;1.5708rad)
FEATURE [App::DocumentObjectGroup] Group010  label="Parafusos - 92 parafusos"
  Group = -> [Array003,Array004,Array005,Array006,Array007,Array008,Array009,Array010,Array011,Array012,Array013,Array014,Array015,Array016,Array017,Array002,Array001]
FEATURE [Part::Feature] Polyline
  Placement = pos=(4000,800,0) rot=(0,0,1;3.14159rad)
  shape: bbox 75 x 2266 x 2e-07 mm, 1 faces, 0 solids (baked)
FEATURE [Part::Feature] Polyline001
  Placement = pos=(4000,800,0) rot=(0,0,1;3.14159rad)
  shape: bbox 75 x 2187 x 2e-07 mm, 1 faces, 0 solids (baked)
FEATURE [Part::Feature] Polyline003
  Placement = pos=(4000,800,0) rot=(0,0,1;3.14159rad)
  shape: bbox 75 x 2280 x 2e-07 mm, 1 faces, 0 solids (baked)
FEATURE [Part::Feature] Polyline005
  Placement = pos=(4000,800,0) rot=(0,0,1;3.14159rad)
  shape: bbox 75 x 1384 x 2e-07 mm, 1 faces, 0 solids (baked)
FEATURE [Part::FeaturePython] Panel151  label="Finição"  # WARN: FeaturePython — macro-defined, semantics opaque (R4)
  Area = 137909
  Base = -> Polyline
  FaceMaker = 0
  HorizontalArea = 0
  Length = 0
  MoveWithHost = false
  Normal = (0,0,0)
  PerimeterLength = 0
  Placement = pos=(4390,339.251,267.999) rot=(0,0,1;3.14159rad)
  Role = 0
  Sheets = 1
  Tag = CAP4
  Thickness = 18
  VerticalArea = 0
  WaveDirection = 0
  WaveHeight = 0
  WaveLength = 0
  WaveType = 0
  Width = 0
FEATURE [Part::FeaturePython] Panel152  label="Finição002"  # WARN: FeaturePython — macro-defined, semantics opaque (R4)
  Area = 126618
  Base = -> Polyline001
  FaceMaker = 0
  HorizontalArea = 0
  Length = 0
  MoveWithHost = false
  Normal = (0,0,0)
  PerimeterLength = 0
  Placement = pos=(3915,1825,1692.58) rot=(0,0.707107,0.707107;3.14159rad)
  Role = 0
  Sheets = 1
  Tag = CAP1
  Thickness = 18
  VerticalArea = 0
  WaveDirection = 0
  WaveHeight = 0
  WaveLength = 0
  WaveType = 0
  Width = 0
FEATURE [Part::FeaturePython] Panel154  label="Finição001"  # WARN: FeaturePython — macro-defined, semantics opaque (R4)
  Area = 81455.5
  Base = -> Polyline005
  FaceMaker = 0
  HorizontalArea = 0
  Length = 0
  MoveWithHost = false
  Normal = (0,0,0)
  PerimeterLength = 0
  Placement = pos=(3630,-1045,267.999) rot=(0,0,1;3.14159rad)
  Role = 0
  Sheets = 1
  Tag = CAP3
  Thickness = 18
  VerticalArea = 0
  WaveDirection = 0
  WaveHeight = 0
  WaveLength = 0
  WaveType = 0
  Width = 0
FEATURE [Part::FeaturePython] Panel156  label="Finição004"  # WARN: FeaturePython — macro-defined, semantics opaque (R4)
  Area = 133326
  Base = -> Polyline003
  FaceMaker = 0
  HorizontalArea = 0
  Length = 0
  MoveWithHost = false
  Normal = (0,0,0)
  PerimeterLength = 0
  Placement = pos=(4485,618.247,3387) rot=(0,0.322006,0.946738;3.14159rad)
  Role = 0
  Sheets = 1
  Tag = CAP2
  Thickness = 18
  VerticalArea = 0
  WaveDirection = 0
  WaveHeight = 0
  WaveLength = 0
  WaveType = 0
  Width = 0
FEATURE [Part::FeaturePython] Panel157  label="Finição006"  # WARN: FeaturePython — macro-defined, semantics opaque (R4)
  Area = 126618
  CloneOf = -> Panel152
  FaceMaker = 0
  HorizontalArea = 0
  Length = 0
  MoveWithHost = false
  Normal = (0,0,0)
  PerimeterLength = 0
  Placement = pos=(3915,-1807,1692.58) rot=(0,0.707107,0.707107;3.14159rad)
  Role = 0
  Sheets = 1
  Tag = CAP1
  Thickness = 18
  VerticalArea = 0
  WaveDirection = 0
  WaveHeight = 0
  WaveLength = 0
  WaveType = 0
  Width = 0
FEATURE [Part::FeaturePython] Panel158  label="Finição007"  # WARN: FeaturePython — macro-defined, semantics opaque (R4)
  Area = 133326
  CloneOf = -> Panel156
  FaceMaker = 0
  HorizontalArea = 0
  Length = 0
  MoveWithHost = false
  Normal = (0,0,0)
  PerimeterLength = 0
  Placement = pos=(4485,-629.222,3401.27) rot=(0,0.946738,0.322006;3.14159rad)
  Role = 0
  Sheets = 1
  Tag = CAP2
  Thickness = 18
  VerticalArea = 0
  WaveDirection = 0
  WaveHeight = 0
  WaveLength = 0
  WaveType = 0
  Width = 0
FEATURE [App::DocumentObjectGroup] Group011  label="Finição - 6 peças"
  Group = -> [Panel151,Panel152,Panel154,Panel156,Panel157,Panel158]
FEATURE [App::DocumentObjectGroup] Group  label="Wren component"
  Group = -> [Group001,Group005,Group006,Group010,Group011]
